FCSTD DOCUMENT  (FreeCAD 0.22R0.21.2)
Label: XL30AssemblyChamber01
License: All rights reserved
LicenseURL: http://en.wikipedia.org/wiki/All_rights_reserved
objects: Part::Feature×37, Part::Cylinder×30, Part::Compound×21, App::Link×18, Part::Cut×18, Part::MultiFuse×13, Part::Box×9, Part::FeaturePython×8, Spreadsheet::Sheet×1, Part::Sphere×1, App::Part×1
note: 137 computed .brp shape members not serialized (recipe doc carries the construction recipe); baked Part::Feature solids carry a one-line shape summary decoded from their .brp
EXTERNAL_REF file=XL30MainChamberModel.FCStd obj=Cut020
EXTERNAL_REF file=XL30ColumnOutline.FCStd obj=Cut001
EXTERNAL_REF file=XL30FinalAppertureHolder.FCStd obj=Cut001_solid
EXTERNAL_REF file=XL30ColumnAttachmentRing01.FCStd obj=Cut010
EXTERNAL_REF file=XL30ColumnAttachmentRing01.FCStd obj=Spreadsheet
EXTERNAL_REF file=XL30ColumnAttachmentRing_PCBKicker01.FCStd obj=Fusion001
EXTERNAL_REF file=XL30ColumnAttachmentRing_PCBKicker01.FCStd obj=Cut005
EXTERNAL_REF file=../QUAK/ESRCryoStage/Cryostage.FCStd obj=Compound001
EXTERNAL_REF file=XL30Frontdoor_Flanges01.FCStd obj=Cut005_solid
EXTERNAL_REF file=PhilippsXL30_FlangeToCF35_CF40_ZeroLengthAdapter_100.FCStd obj=Cut002
EXTERNAL_REF file=PhilippsXL30_FlangeToCF63_ZeroLengthAdapter_120.FCStd obj=Cut001
EXTERNAL_REF file=PhilipsXL30_FlangeToCF35_CF40_ZeroLengthAdapter.FCStd obj=Cut002
EXTERNAL_REF file=PhilipsXL30_Blindflange_100_TopBack.FCStd obj=Cut004
EXTERNAL_REF file=Quak_XL30_Modulator2.FCStd obj=Compound
EXTERNAL_REF file=PhilipsXL30_AligningRing.FCStd obj=Cut005_solid
EXTERNAL_REF file=PhilipsXL30_AligningRing.FCStd obj=Cut006_solid

FEATURE [App::Link] Link  label="MainChamberModel"
  LinkedObject = -> <external XL30MainChamberModel.FCStd>#Cut020
FEATURE [App::Link] Link001  label="BasicOutline_Part0and1"
  LinkPlacement = pos=(165,116,310) rot=(0,0,1;0rad)
  LinkedObject = -> <external XL30ColumnOutline.FCStd>#Cut001
  Placement = pos=(165,116,310) rot=(0,0,1;0rad)
FEATURE [App::Link] Link002  label="XL30FinalAppertureHolder"
  LinkPlacement = pos=(165,116,207.1) rot=(0,0,1;0rad)
  LinkedObject = -> <external XL30FinalAppertureHolder.FCStd>#Cut001_solid
  Placement = pos=(165,116,207.1) rot=(0,0,1;0rad)
FEATURE [App::Link] Link003  label="AttachmentRing_Column01"
  LinkPlacement = pos=(165,116,270) rot=(0,0,1;0rad)
  LinkedObject = -> <external XL30ColumnAttachmentRing01.FCStd>#Cut010
  Placement = pos=(165,116,270) rot=(0,0,1;0rad)
FEATURE [Part::FeaturePython] ScrewTap  label="M4x119.9-ScrewTap"  # Fasteners workbench fastener (typed FeaturePython)
  Placement = pos=(53.83,0,0) rot=(0,0,1;0rad)
  diameter = 6
  diameterCustom = 6
  invert = false
  leftHanded = false
  length = 119.9
  matchOuter = false
  offset = 0
  pitchCustom = 1
  thread = true
  type = 2
  expr: .Placement.Base.x = (<<XL30ColumnAttachmentRing01>>#<<AttachmentRing01>>.ring_od + <<XL30ColumnAttachmentRing01>>#<<AttachmentRing01>>.ring_id) / 4
  expr: length = <<XL30Assembly01>>.attachment_pcb_threadrod_lenmin
FEATURE [Spreadsheet::Sheet] Spreadsheet  label="XL30Assembly01"
  cells = A2='PCB Ring distance; B2(attachmentring_pcb_distance)==18 + 62.9; C2='Note: Include poleshoe height of 62.9mm; E2='Real threaded rod minimum length; F2(attachment_pcb_threadrod_lenmin)==attachmentring_pcb_distance + 2 * <<XL30ColumnAttachmentRing01>>#<<AttachmentRing01>>.ring_thickness + 7 + 22
FEATURE [Part::FeaturePython] ScrewTap001  label="M4x119.9-ScrewTap001"  # Fasteners workbench fastener (typed FeaturePython)
  Placement = pos=(53.83,0,0) rot=(0,0,1;0rad)
  diameter = 6
  diameterCustom = 6
  invert = false
  leftHanded = false
  length = 119.9
  matchOuter = false
  offset = 0
  pitchCustom = 1
  thread = true
  type = 2
  expr: .Placement.Base.x = (<<XL30ColumnAttachmentRing01>>#<<AttachmentRing01>>.ring_od + <<XL30ColumnAttachmentRing01>>#<<AttachmentRing01>>.ring_id) / 4
  expr: length = <<XL30Assembly01>>.attachment_pcb_threadrod_lenmin
FEATURE [Part::Compound] Compound
  Links = -> [ScrewTap001]
  Placement = pos=(0,0,0) rot=(0,0,1;0.785398rad)
FEATURE [Part::FeaturePython] ScrewTap002  label="M4x119.9-ScrewTap002"  # Fasteners workbench fastener (typed FeaturePython)
  Placement = pos=(53.83,0,0) rot=(0,0,1;0rad)
  diameter = 6
  diameterCustom = 6
  invert = false
  leftHanded = false
  length = 119.9
  matchOuter = false
  offset = 0
  pitchCustom = 1
  thread = true
  type = 2
  expr: .Placement.Base.x = (<<XL30ColumnAttachmentRing01>>#<<AttachmentRing01>>.ring_od + <<XL30ColumnAttachmentRing01>>#<<AttachmentRing01>>.ring_id) / 4
  expr: length = <<XL30Assembly01>>.attachment_pcb_threadrod_lenmin
FEATURE [Part::Compound] Compound001
  Links = -> [ScrewTap002]
  Placement = pos=(0,0,0) rot=(0,0,1;1.5708rad)
FEATURE [Part::FeaturePython] ScrewTap003  label="M4x119.9-ScrewTap003"  # Fasteners workbench fastener (typed FeaturePython)
  Placement = pos=(53.83,0,0) rot=(0,0,1;0rad)
  diameter = 6
  diameterCustom = 6
  invert = false
  leftHanded = false
  length = 119.9
  matchOuter = false
  offset = 0
  pitchCustom = 1
  thread = true
  type = 2
  expr: .Placement.Base.x = (<<XL30ColumnAttachmentRing01>>#<<AttachmentRing01>>.ring_od + <<XL30ColumnAttachmentRing01>>#<<AttachmentRing01>>.ring_id) / 4
  expr: length = <<XL30Assembly01>>.attachment_pcb_threadrod_lenmin
FEATURE [Part::Compound] Compound002
  Links = -> [ScrewTap003]
  Placement = pos=(0,0,0) rot=(0,0,1;2.35619rad)
FEATURE [Part::FeaturePython] ScrewTap004  label="M4x119.9-ScrewTap004"  # Fasteners workbench fastener (typed FeaturePython)
  Placement = pos=(53.83,0,0) rot=(0,0,1;0rad)
  diameter = 6
  diameterCustom = 6
  invert = false
  leftHanded = false
  length = 119.9
  matchOuter = false
  offset = 0
  pitchCustom = 1
  thread = true
  type = 2
  expr: .Placement.Base.x = (<<XL30ColumnAttachmentRing01>>#<<AttachmentRing01>>.ring_od + <<XL30ColumnAttachmentRing01>>#<<AttachmentRing01>>.ring_id) / 4
  expr: length = <<XL30Assembly01>>.attachment_pcb_threadrod_lenmin
FEATURE [Part::Compound] Compound003
  Links = -> [ScrewTap004]
  Placement = pos=(0,0,0) rot=(0,0,1;3.14159rad)
FEATURE [Part::FeaturePython] ScrewTap005  label="M4x119.9-ScrewTap005"  # Fasteners workbench fastener (typed FeaturePython)
  Placement = pos=(53.83,0,0) rot=(0,0,1;0rad)
  diameter = 6
  diameterCustom = 6
  invert = false
  leftHanded = false
  length = 119.9
  matchOuter = false
  offset = 0
  pitchCustom = 1
  thread = true
  type = 2
  expr: .Placement.Base.x = (<<XL30ColumnAttachmentRing01>>#<<AttachmentRing01>>.ring_od + <<XL30ColumnAttachmentRing01>>#<<AttachmentRing01>>.ring_id) / 4
  expr: length = <<XL30Assembly01>>.attachment_pcb_threadrod_lenmin
FEATURE [Part::Compound] Compound004
  Links = -> [ScrewTap005]
  Placement = pos=(0,0,0) rot=(0,0,1;3.92699rad)
FEATURE [Part::FeaturePython] ScrewTap006  label="M4x119.9-ScrewTap006"  # Fasteners workbench fastener (typed FeaturePython)
  Placement = pos=(53.83,0,0) rot=(0,0,1;0rad)
  diameter = 6
  diameterCustom = 6
  invert = false
  leftHanded = false
  length = 119.9
  matchOuter = false
  offset = 0
  pitchCustom = 1
  thread = true
  type = 2
  expr: .Placement.Base.x = (<<XL30ColumnAttachmentRing01>>#<<AttachmentRing01>>.ring_od + <<XL30ColumnAttachmentRing01>>#<<AttachmentRing01>>.ring_id) / 4
  expr: length = <<XL30Assembly01>>.attachment_pcb_threadrod_lenmin
FEATURE [Part::Compound] Compound005
  Links = -> [ScrewTap006]
  Placement = pos=(0,0,0) rot=(0,0,-1;1.5708rad)
FEATURE [Part::FeaturePython] ScrewTap007  label="M4x119.9-ScrewTap007"  # Fasteners workbench fastener (typed FeaturePython)
  Placement = pos=(53.83,0,0) rot=(0,0,1;0rad)
  diameter = 6
  diameterCustom = 6
  invert = false
  leftHanded = false
  length = 119.9
  matchOuter = false
  offset = 0
  pitchCustom = 1
  thread = true
  type = 2
  expr: .Placement.Base.x = (<<XL30ColumnAttachmentRing01>>#<<AttachmentRing01>>.ring_od + <<XL30ColumnAttachmentRing01>>#<<AttachmentRing01>>.ring_id) / 4
  expr: length = <<XL30Assembly01>>.attachment_pcb_threadrod_lenmin
FEATURE [Part::Compound] Compound006
  Links = -> [ScrewTap007]
  Placement = pos=(0,0,0) rot=(0,0,-1;0.785398rad)
FEATURE [Part::Compound] Compound007  label="ThreadedRodsAttachmentRing"
  Links = -> [Compound006,Compound,Compound001,Compound002,Compound003,Compound004,Compound005,ScrewTap]
  Placement = pos=(165,116,275) rot=(0,0,1;0rad)
  expr: .Placement.Base.z = 270 + <<XL30ColumnAttachmentRing01>>#<<AttachmentRing01>>.ring_thickness
FEATURE [App::Link] Link005  label="Stackmountring01"
  LinkPlacement = pos=(165,116,158) rot=(0,0,1;0rad)
  LinkedObject = -> <external XL30ColumnAttachmentRing_PCBKicker01.FCStd>#Fusion001
  Placement = pos=(165,116,158) rot=(0,0,1;0rad)
FEATURE [App::Link] Link006  label="PCBStackTemplate"
  LinkPlacement = pos=(155,95,185) rot=(0,0,1;0rad)
  LinkedObject = -> <external XL30ColumnAttachmentRing_PCBKicker01.FCStd>#Cut005
  Placement = pos=(155,95,185) rot=(0,0,1;0rad)
FEATURE [Part::Cylinder] Cylinder
  Angle = 360
  AttacherType = Attacher::AttachEngine3D
  FirstAngle = 0
  Height = 296.4
  Placement = pos=(0,0,-83.4) rot=(0,1,0;0rad)
  Radius = 21
  SecondAngle = 0
FEATURE [Part::Sphere] Sphere
  Angle1 = -90
  Angle2 = 90
  Angle3 = 360
  AttacherType = Attacher::AttachEngine3D
  Placement = pos=(0,0,-83.4) rot=(0,0,1;0rad)
  Radius = 21
FEATURE [Part::Compound] Compound008  label="SEDetectorTemplate"
  Links = -> [Cylinder,Sphere]
  Placement = pos=(18,116,275) rot=(0,-1,0;1.23046rad)
FEATURE [App::Link] Link007  label="StageAssembly"
  LinkPlacement = pos=(113.5,99,107) rot=(0,0,1;0rad)
  LinkedObject = -> <external ../QUAK/ESRCryoStage/Cryostage.FCStd>#Compound001
  Placement = pos=(113.5,99,107) rot=(0,0,1;0rad)
FEATURE [App::Link] Link008  label="XL30FrontdoorCF64Flanges (Solid)"
  LinkPlacement = pos=(0,-35,0) rot=(0,0,1;0rad)
  LinkedObject = -> <external XL30Frontdoor_Flanges01.FCStd>#Cut005_solid
  Placement = pos=(0,-35,0) rot=(0,0,1;0rad)
FEATURE [Part::Cylinder] Cylinder001
  Angle = 360
  AttacherType = Attacher::AttachEngine3D
  FirstAngle = 0
  Height = 112
  Placement = pos=(0,116,121.5) rot=(0,1,0;1.5708rad)
  Radius = 5
  SecondAngle = 0
FEATURE [Part::Cylinder] Cylinder002
  Angle = 360
  AttacherType = Attacher::AttachEngine3D
  FirstAngle = 0
  Height = 112
  Placement = pos=(0,116,142.5) rot=(0,1,0;1.5708rad)
  Radius = 5
  SecondAngle = 0
FEATURE [Part::MultiFuse] Fusion  label="NitrogenPipes10mm"
  Shapes = -> [Cylinder001,Cylinder002]
FEATURE [App::Link] Link009  label="StageAssembly001"
  LinkPlacement = pos=(181.5,64.5,88.5) rot=(0,0,1;1.5708rad)
  LinkedObject = -> <external ../QUAK/ESRCryoStage/Cryostage.FCStd>#Compound001
  Placement = pos=(181.5,64.5,88.5) rot=(0,0,1;1.5708rad)
FEATURE [Part::Cylinder] Cylinder003
  Angle = 360
  AttacherType = Attacher::AttachEngine3D
  FirstAngle = 0
  Height = 99.5
  Placement = pos=(0,0,121.5) rot=(0,1,0;1.5708rad)
  Radius = 5
  SecondAngle = 0
FEATURE [Part::Cylinder] Cylinder004
  Angle = 360
  AttacherType = Attacher::AttachEngine3D
  FirstAngle = 0
  Height = 99.5
  Placement = pos=(0,0,142.5) rot=(0,1,0;1.5708rad)
  Radius = 5
  SecondAngle = 0
FEATURE [Part::MultiFuse] Fusion001  label="NitrogenPipes10mm001"
  Shapes = -> [Cylinder003,Cylinder004]
FEATURE [Part::Compound] Compound009  label="NitrogenPipesConfig2"
  Links = -> [Fusion001]
  Placement = pos=(164.5,-35,-18.5) rot=(0,0,1;1.5708rad)
FEATURE [Part::Compound] Compound010  label="StageFromFrontdoor"
  Links = -> [Link009,Compound009]
FEATURE [Part::Compound] Compound011  label="StageFromSide"
  Links = -> [Link007,Fusion]
FEATURE [Part::Box] Box  label="Cube"
  AttacherType = Attacher::AttachEngine3D
  Height = 43
  Length = 50
  Width = 34
FEATURE [Part::Box] Box001  label="Cube001"
  AttacherType = Attacher::AttachEngine3D
  Height = 50
  Length = 100
  Placement = pos=(41,0,43) rot=(0,1,0;0.785398rad)
  Width = 34
FEATURE [Part::Box] Box002  label="Cube002"
  AttacherType = Attacher::AttachEngine3D
  Height = 50
  Length = 72
  Placement = pos=(0,34,34) rot=(1,0,0;0.925025rad)
  Width = 20
FEATURE [Part::Box] Box003  label="Cube003"
  AttacherType = Attacher::AttachEngine3D
  Height = 50
  Length = 72
  Placement = pos=(0,34,34) rot=(1,0,0;0.925025rad)
  Width = 20
FEATURE [Part::Box] Box004  label="Cube004"
  AttacherType = Attacher::AttachEngine3D
  Height = 26
  Length = 1.6
  Placement = pos=(49.9,7,0) rot=(0,0,1;0rad)
  Width = 20
FEATURE [Part::Box] Box005  label="Cube005"
  AttacherType = Attacher::AttachEngine3D
  Height = 2
  Length = 15
  Placement = pos=(15,0,0) rot=(0,0,1;0rad)
  Width = 34
FEATURE [Part::Box] Box006  label="Cube006"
  AttacherType = Attacher::AttachEngine3D
  Height = 2
  Length = 15
  Placement = pos=(15,0,0) rot=(0,0,1;0rad)
  Width = 34
FEATURE [Part::Box] Box007  label="Cube007"
  AttacherType = Attacher::AttachEngine3D
  Height = 26
  Length = 30
  Placement = pos=(53,16,0) rot=(0,0,1;0rad)
  Width = 2
FEATURE [Part::Box] Box008  label="Cube008"
  AttacherType = Attacher::AttachEngine3D
  Height = 10
  Length = 10
  Placement = pos=(-7,0,0) rot=(0,1,0;0.785398rad)
  Width = 34
FEATURE [Part::Compound] Compound012
  Links = -> [Box003]
  Placement = pos=(72,34,0) rot=(0,0,1;3.14159rad)
FEATURE [Part::Cylinder] Cylinder005
  Angle = 360
  AttacherType = Attacher::AttachEngine3D
  FirstAngle = 0
  Height = 26
  Radius = 30.5
  SecondAngle = 0
FEATURE [Part::Cylinder] Cylinder006
  Angle = 360
  AttacherType = Attacher::AttachEngine3D
  FirstAngle = 0
  Height = 26
  Radius = 9
  SecondAngle = 0
FEATURE [Part::Cut] Cut001
  Base = -> Cylinder005
  Placement = pos=(51.5,17,0) rot=(0,0,1;0rad)
  Tool = -> Cylinder006
FEATURE [Part::Cylinder] Cylinder007
  Angle = 360
  AttacherType = Attacher::AttachEngine3D
  FirstAngle = 0
  Height = 26
  Radius = 30.5
  SecondAngle = 0
FEATURE [Part::Cylinder] Cylinder008
  Angle = 360
  AttacherType = Attacher::AttachEngine3D
  FirstAngle = 0
  Height = 26
  Radius = 9
  SecondAngle = 0
FEATURE [Part::Cut] Cut002  label="CoilHolderBlank"
  Base = -> Cylinder007
  Placement = pos=(51.5,17,0) rot=(0,0,1;0rad)
  Tool = -> Cylinder008
FEATURE [Part::Cylinder] Cylinder009
  Angle = 360
  AttacherType = Attacher::AttachEngine3D
  FirstAngle = 0
  Height = 22
  Radius = 30.5
  SecondAngle = 0
FEATURE [Part::Cylinder] Cylinder010
  Angle = 360
  AttacherType = Attacher::AttachEngine3D
  FirstAngle = 0
  Height = 22
  Radius = 11
  SecondAngle = 0
FEATURE [Part::Cut] Cut004  label="CoilArea"
  Base = -> Cylinder009
  Placement = pos=(51.5,17,2) rot=(0,0,1;0rad)
  Tool = -> Cylinder010
FEATURE [Part::Cut] Cut005
  Base = -> Cut002
  Tool = -> Cut004
FEATURE [Part::Cut] Cut007
  Base = -> Cut005
  Tool = -> Box004
FEATURE [Part::Cylinder] Cylinder011
  Angle = 360
  AttacherType = Attacher::AttachEngine3D
  FirstAngle = 0
  Height = 34
  Placement = pos=(35,34,30) rot=(1,0,0;1.5708rad)
  Radius = 1.65
  SecondAngle = 0
FEATURE [Part::Cylinder] Cylinder012
  Angle = 360
  AttacherType = Attacher::AttachEngine3D
  FirstAngle = 0
  Height = 34
  Placement = pos=(35,20,27) rot=(1,0,0;0rad)
  Radius = 1.65
  SecondAngle = 0
FEATURE [Part::Cylinder] Cylinder013
  Angle = 360
  AttacherType = Attacher::AttachEngine3D
  FirstAngle = 0
  Height = 34
  Placement = pos=(35,14,27) rot=(1,0,0;0rad)
  Radius = 1.65
  SecondAngle = 0
FEATURE [Part::Cylinder] Cylinder014
  Angle = 360
  AttacherType = Attacher::AttachEngine3D
  FirstAngle = 0
  Height = 10
  Placement = pos=(20,5,0) rot=(0,0,1;0rad)
  Radius = 2.5
  SecondAngle = 0
FEATURE [Part::Cylinder] Cylinder015
  Angle = 360
  AttacherType = Attacher::AttachEngine3D
  FirstAngle = 0
  Height = 10
  Placement = pos=(20,29,0) rot=(0,0,1;0rad)
  Radius = 2.5
  SecondAngle = 0
FEATURE [Part::Cylinder] Cylinder016
  Angle = 360
  AttacherType = Attacher::AttachEngine3D
  FirstAngle = 0
  Height = 10
  Placement = pos=(20,5,0) rot=(0,0,1;0rad)
  Radius = 2.5
  SecondAngle = 0
FEATURE [Part::Cylinder] Cylinder017
  Angle = 360
  AttacherType = Attacher::AttachEngine3D
  FirstAngle = 0
  Height = 10
  Placement = pos=(20,29,0) rot=(0,0,1;0rad)
  Radius = 2.5
  SecondAngle = 0
FEATURE [Part::Cylinder] Cylinder018
  Angle = 360
  AttacherType = Attacher::AttachEngine3D
  FirstAngle = 0
  Height = 26
  Placement = pos=(39.5,17,0) rot=(0,0,1;0rad)
  Radius = 1
  SecondAngle = 0
FEATURE [Part::Cylinder] Cylinder019
  Angle = 360
  AttacherType = Attacher::AttachEngine3D
  FirstAngle = 0
  Height = 26
  Placement = pos=(23,17,0) rot=(0,0,1;0rad)
  Radius = 1
  SecondAngle = 0
FEATURE [Part::Cylinder] Cylinder020  label="NitrogenChamber01"
  Angle = 360
  AttacherType = Attacher::AttachEngine3D
  FirstAngle = 0
  Height = 38
  Placement = pos=(13,17,0) rot=(0,0,1;1.5708rad)
  Radius = 5
  SecondAngle = 0
FEATURE [Part::Cylinder] Cylinder021  label="NitrogenChamber002"
  Angle = 360
  AttacherType = Attacher::AttachEngine3D
  FirstAngle = 0
  Height = 20
  Placement = pos=(0,17,14.5) rot=(0,1,0;1.5708rad)
  Radius = 5
  SecondAngle = 0
FEATURE [Part::Cylinder] Cylinder022  label="NitrogenChamber003"
  Angle = 360
  AttacherType = Attacher::AttachEngine3D
  FirstAngle = 0
  Height = 20
  Placement = pos=(0,17,35.5) rot=(0,1,0;1.5708rad)
  Radius = 5
  SecondAngle = 0
FEATURE [Part::Cylinder] Cylinder023
  Angle = 360
  AttacherType = Attacher::AttachEngine3D
  FirstAngle = 0
  Height = 20
  Placement = pos=(0,4.5,0) rot=(0,1,0;0.785398rad)
  Radius = 1.65
  SecondAngle = 0
FEATURE [Part::Cylinder] Cylinder024
  Angle = 360
  AttacherType = Attacher::AttachEngine3D
  FirstAngle = 0
  Height = 20
  Placement = pos=(0,29.5,0) rot=(0,1,0;0.785398rad)
  Radius = 1.65
  SecondAngle = 0
FEATURE [Part::Cylinder] Cylinder025
  Angle = 360
  AttacherType = Attacher::AttachEngine3D
  FirstAngle = 0
  Height = 48
  Placement = pos=(0,5,26) rot=(0,1,0;1.5708rad)
  Radius = 1.5
  SecondAngle = 0
FEATURE [Part::Cylinder] Cylinder026
  Angle = 360
  AttacherType = Attacher::AttachEngine3D
  FirstAngle = 0
  Height = 48
  Placement = pos=(0,29,26) rot=(0,1,0;1.5708rad)
  Radius = 1.5
  SecondAngle = 0
FEATURE [Part::MultiFuse] Fusion002
  Shapes = -> [Box001,Box002,Compound012]
FEATURE [Part::Cut] Cut
  Base = -> Box
  Tool = -> Fusion002
FEATURE [Part::Cut] Cut003
  Base = -> Cut
  Tool = -> Cut001
FEATURE [Part::MultiFuse] Fusion003  label="M4Mountscrews01_Corehole"
  Shapes = -> [Cylinder011,Cylinder012,Cylinder013]
FEATURE [Part::Cut] Cut008
  Base = -> Cut003
  Tool = -> Fusion003
FEATURE [Part::MultiFuse] Fusion004  label="BoreholeM6Screws01"
  Shapes = -> [Cylinder015,Cylinder014]
FEATURE [Part::Cut] Cut009
  Base = -> Cut008
  Tool = -> Fusion004
FEATURE [Part::Cut] Cut011
  Base = -> Cut009
  Tool = -> Box006
FEATURE [Part::MultiFuse] Fusion005  label="BoreholeM6Screws002"
  Shapes = -> [Cylinder017,Cylinder016]
FEATURE [Part::Cut] Cut010
  Base = -> Box005
  Tool = -> Fusion005
FEATURE [Part::MultiFuse] Fusion006
  Shapes = -> [Cut007,Cut010]
FEATURE [Part::Cut] Cut012
  Base = -> Fusion006
  Tool = -> Box007
FEATURE [Part::MultiFuse] Fusion007  label="WireHoles"
  Shapes = -> [Cylinder019,Cylinder018]
FEATURE [Part::Cut] Cut013  label="Coilholder"
  Base = -> Cut012
  Tool = -> Fusion007
FEATURE [Part::MultiFuse] Fusion008  label="NitrogenChamber"
  Shapes = -> [Cylinder020,Cylinder021,Cylinder022]
FEATURE [Part::Cut] Cut014
  Base = -> Cut011
  Tool = -> Fusion008
FEATURE [Part::Cut] Cut015
  Base = -> Cut014
  Tool = -> Box008
FEATURE [Part::MultiFuse] Fusion009  label="M4Screws"
  Shapes = -> [Cylinder023,Cylinder024]
FEATURE [Part::Cut] Cut016
  Base = -> Cut015
  Tool = -> Fusion009
FEATURE [Part::MultiFuse] Fusion010  label="CableDrillHole"
  Shapes = -> [Cylinder025,Cylinder026]
FEATURE [Part::Cut] Cut017  label="Cryostage"
  Base = -> Cut016
  Tool = -> Fusion010
FEATURE [Part::Compound] Compound013  label="StageAssembly002"
  Links = -> [Cut013,Cut017]
  Placement = pos=(-51.5,-17,0) rot=(0,0,1;0rad)
FEATURE [Part::Cylinder] Cylinder027
  Angle = 360
  AttacherType = Attacher::AttachEngine3D
  FirstAngle = 0
  Height = 99.5
  Placement = pos=(0,0,121.5) rot=(0,1,0;1.5708rad)
  Radius = 5
  SecondAngle = 0
FEATURE [Part::Cylinder] Cylinder028
  Angle = 360
  AttacherType = Attacher::AttachEngine3D
  FirstAngle = 0
  Height = 99.5
  Placement = pos=(0,0,142.5) rot=(0,1,0;1.5708rad)
  Radius = 5
  SecondAngle = 0
FEATURE [Part::MultiFuse] Fusion011  label="NitrogenPipes10mm002"
  Shapes = -> [Cylinder027,Cylinder028]
FEATURE [Part::Compound] Compound014  label="NitrogenPipesConfig003"
  Links = -> [Fusion011]
  Placement = pos=(164.5,-35,-18.5) rot=(0,0,1;1.5708rad)
FEATURE [App::Link] Link010  label="StageAssembly003"
  LinkPlacement = pos=(181.5,64.5,88.5) rot=(0,0,1;1.5708rad)
  LinkedObject = -> Compound013
  Placement = pos=(181.5,64.5,88.5) rot=(0,0,1;1.5708rad)
FEATURE [Part::Compound] Compound015  label="StageFromFrontdoor_LowestPossiblePosition"
  Links = -> [Link010,Compound014]
  Placement = pos=(0,0,-55) rot=(0,0,1;0rad)
FEATURE [App::Link] Link011  label="Flange100mmToCF40_Right"
  LinkPlacement = pos=(330,107.5,199) rot=(0,1,0;1.5708rad)
  LinkedObject = -> <external PhilippsXL30_FlangeToCF35_CF40_ZeroLengthAdapter_100.FCStd>#Cut002
  Placement = pos=(330,107.5,199) rot=(0,1,0;1.5708rad)
FEATURE [App::Link] Link012  label="Cut017"
  LinkPlacement = pos=(0,0,0) rot=(0,1,0;-1.5708rad)
  LinkedObject = -> <external PhilippsXL30_FlangeToCF63_ZeroLengthAdapter_120.FCStd>#Cut001
  Placement = pos=(0,0,0) rot=(0,1,0;-1.5708rad)
FEATURE [Part::Compound] Compound016  label="Flange120mmToCF64_Left"
  Links = -> [Link012]
  Placement = pos=(0,115.5,140) rot=(1,0,0;1.0472rad)
FEATURE [App::Link] Link013  label="Flange85mmToCF40_BackBottom_001"
  LinkPlacement = pos=(0,0,0) rot=(0,1,0;-1.5708rad)
  LinkedObject = -> <external PhilipsXL30_FlangeToCF35_CF40_ZeroLengthAdapter.FCStd>#Cut002
  Placement = pos=(0,0,0) rot=(0,1,0;-1.5708rad)
FEATURE [App::Link] Link015  label="Flange85mmToCF40_BackBottom_002"
  LinkPlacement = pos=(0,0,0) rot=(0,1,0;-1.5708rad)
  Placement = pos=(0,0,0) rot=(0,1,0;-1.5708rad)
FEATURE [Part::Compound] Compound017
  Links = -> [Link013]
  Placement = pos=(0,0,0) rot=(1,0,0;1.0472rad)
FEATURE [Part::Compound] Compound018  label="Flange85mmToCF40_BackBottom"
  Links = -> [Compound017]
  Placement = pos=(45,240,97.5) rot=(0,0,-1;0.785398rad)
FEATURE [Part::Feature] Solid  label="CF35 Flange"
  Placement = pos=(0,0,4) rot=(-1,0,0;1.5708rad)
  shape: bbox 70 x 70 x 12.7 mm, 58 faces (baked)
FEATURE [App::Link] Link016  label="XL30TopBackFlange100"
  LinkedObject = -> <external PhilipsXL30_Blindflange_100_TopBack.FCStd>#Cut004
FEATURE [Part::MultiFuse] Fusion012
  Shapes = -> [Solid,Link016]
FEATURE [Part::Cylinder] Cylinder029
  Angle = 360
  AttacherType = Attacher::AttachEngine3D
  FirstAngle = 0
  Height = 30
  Placement = pos=(0,0,-10) rot=(0,0,1;0rad)
  Radius = 20
  SecondAngle = 0
FEATURE [Part::Cut] Cut018  label="PhilipsXL30_Flange_100_TopLeft_ToCF35_CF40"
  Base = -> Fusion012
  Placement = pos=(-12,0,0) rot=(0,1,0;1.5708rad)
  Tool = -> Cylinder029
FEATURE [Part::Compound] Compound019
  Links = -> [Cut018]
  Placement = pos=(0,0,0) rot=(1,0,0;1.5708rad)
FEATURE [Part::Compound] Compound020
  Links = -> [Compound019]
  Placement = pos=(45,240,286) rot=(0,0,-1;0.785398rad)
FEATURE [Part::Feature] Part__Feature  label="Bellow-AA-All_Bellow63-35025-1.3"
  shape: bbox 88.9 x 69.2 x 88.9 mm, 28 faces (baked)
FEATURE [Part::Feature] Part__Feature001  label="NW63CF-weld_Tube70"
  Placement = pos=(0,78.7,0) rot=(0,0,1;0rad)
  shape: bbox 113.5 x 17.5 x 113.5 mm, 80 faces (baked)
FEATURE [Part::Feature] Part__Feature002  label="NW63CF-weld_Tube071"
  Placement = pos=(0,-9.5,0) rot=(0.382683,0,0.92388;3.14159rad)
  shape: bbox 113.5 x 17.5 x 113.5 mm, 80 faces (baked)
FEATURE [Part::Feature] Part__Feature003  label="Bracket SEWB_CF63-D113.5"
  Placement = pos=(-63.0548,67.7,26.1181) rot=(0,1,0;0.392699rad)
  shape: bbox 26.73 x 6 x 25.71 mm, 14 faces (baked)
FEATURE [Part::Feature] Part__Feature004  label="Bracket SEWB_CF63-D113.006"
  Placement = pos=(8.90841,67.7,-67.6661) rot=(0,-1,0;1.7017rad)
  shape: bbox 22.29 x 6 x 23.92 mm, 14 faces (baked)
FEATURE [Part::Feature] Part__Feature005  label="Bracket SEWB_CF63-D113.007"
  Placement = pos=(54.1464,67.7,41.548) rot=(0,1,0;2.48709rad)
  shape: bbox 27.71 x 6 x 27.37 mm, 14 faces (baked)
FEATURE [Part::Feature] Part__Feature006  label="Bracket SEWB_CF63-D113.008"
  Placement = pos=(8.90841,-4.5,-67.6661) rot=(0,-1,0;1.7017rad)
  shape: bbox 22.29 x 6 x 23.92 mm, 14 faces (baked)
FEATURE [Part::Feature] Part__Feature007  label="Bracket SEWB_CF63-D113.009"
  Placement = pos=(54.1464,-4.5,41.548) rot=(0,1,0;2.48709rad)
  shape: bbox 27.71 x 6 x 27.37 mm, 14 faces (baked)
FEATURE [Part::Feature] Part__Feature008  label="Bracket SEWB_CF63-D113.010"
  Placement = pos=(-63.0548,-4.5,26.1181) rot=(0,1,0;0.392699rad)
  shape: bbox 26.73 x 6 x 25.71 mm, 14 faces (baked)
FEATURE [Part::Feature] Part__Feature009  label="StudM8-L130"
  Placement = pos=(-63.05,16.6,26.12) rot=(-0.427908,0.427908,-0.796109;1.79333rad)
  shape: bbox 8.701 x 131.4 x 9.485 mm, 203 faces (baked)
FEATURE [Part::Feature] Part__Feature010  label="StudM8-L131"
  Placement = pos=(8.91,16.6,-67.67) rot=(0,0,-1;1.5708rad)
  shape: bbox 8.06 x 131.5 x 9.307 mm, 203 faces (baked)
FEATURE [Part::Feature] Part__Feature011  label="StudM8-L132"
  Placement = pos=(54.15,16.6,41.55) rot=(0,0,-1;1.5708rad)
  shape: bbox 8.06 x 131.5 x 9.307 mm, 203 faces (baked)
FEATURE [Part::Feature] Part__Feature012  label="plain washer normal grade a_iso_Washer ISO 7089 - 8"
  Placement = pos=(54.1464,73.7,41.548) rot=(0,0,-1;1.5708rad)
  shape: bbox 16 x 1.6 x 16 mm, 6 faces (baked)
FEATURE [Part::Feature] Part__Feature013  label="plain washer normal grade a_iso_Washer ISO 7089 - 009"
  Placement = pos=(-63.0548,73.7,26.1181) rot=(0,0,-1;1.5708rad)
  shape: bbox 16 x 1.6 x 16 mm, 6 faces (baked)
FEATURE [Part::Feature] Part__Feature014  label="plain washer normal grade a_iso_Washer ISO 7089 - 010"
  Placement = pos=(8.90841,73.7,-67.6661) rot=(0,0,-1;1.5708rad)
  shape: bbox 16 x 1.6 x 16 mm, 6 faces (baked)
FEATURE [Part::Feature] Part__Feature015  label="plain washer normal grade a_iso_Washer ISO 7089 - 011"
  Placement = pos=(8.90841,67.7,-67.6661) rot=(0,0,1;1.5708rad)
  shape: bbox 16 x 1.6 x 16 mm, 6 faces (baked)
FEATURE [Part::Feature] Part__Feature016  label="plain washer normal grade a_iso_Washer ISO 7089 - 012"
  Placement = pos=(8.90841,-4.5,-67.6661) rot=(0,0,1;1.5708rad)
  shape: bbox 16 x 1.6 x 16 mm, 6 faces (baked)
FEATURE [Part::Feature] Part__Feature017  label="plain washer normal grade a_iso_Washer ISO 7089 - 013"
  Placement = pos=(54.1464,-4.5,41.548) rot=(0,0,1;1.5708rad)
  shape: bbox 16 x 1.6 x 16 mm, 6 faces (baked)
FEATURE [Part::Feature] Part__Feature018  label="plain washer normal grade a_iso_Washer ISO 7089 - 014"
  Placement = pos=(-63.0548,-4.5,26.1181) rot=(0,0,1;1.5708rad)
  shape: bbox 16 x 1.6 x 16 mm, 6 faces (baked)
FEATURE [Part::Feature] Part__Feature019  label="plain washer normal grade a_iso_Washer ISO 7089 - 015"
  Placement = pos=(-63.0548,67.7,26.1181) rot=(0,0,1;1.5708rad)
  shape: bbox 16 x 1.6 x 16 mm, 6 faces (baked)
FEATURE [Part::Feature] Part__Feature020  label="plain washer normal grade a_iso_Washer ISO 7089 - 016"
  Placement = pos=(54.1464,67.7,41.548) rot=(0,0,1;1.5708rad)
  shape: bbox 16 x 1.6 x 16 mm, 6 faces (baked)
FEATURE [Part::Feature] Part__Feature021  label="plain washer normal grade a_iso_Washer ISO 7089 - 017"
  Placement = pos=(54.1464,1.5,41.548) rot=(0,0,-1;1.5708rad)
  shape: bbox 16 x 1.6 x 16 mm, 6 faces (baked)
FEATURE [Part::Feature] Part__Feature022  label="plain washer normal grade a_iso_Washer ISO 7089 - 018"
  Placement = pos=(-63.0548,1.5,26.1181) rot=(0,0,-1;1.5708rad)
  shape: bbox 16 x 1.6 x 16 mm, 6 faces (baked)
FEATURE [Part::Feature] Part__Feature023  label="plain washer normal grade a_iso_Washer ISO 7089 - 019"
  Placement = pos=(8.90841,1.5,-67.6661) rot=(0,0,-1;1.5708rad)
  shape: bbox 16 x 1.6 x 16 mm, 6 faces (baked)
FEATURE [Part::Feature] Part__Feature024  label="hex nut style 1 gradeab_iso_ISO - 4032 - M8 - W - N"
  Placement = pos=(8.90841,-12.9,-67.6661) rot=(1,0,0;1.5708rad)
  shape: bbox 15.01 x 6.801 x 15.01 mm, 30 faces (baked)
FEATURE [Part::Feature] Part__Feature025  label="hex nut style 1 gradeab_iso_ISO - 4032 - M8 - W - N001"
  Placement = pos=(-63.0548,-12.9,26.1181) rot=(1,0,0;1.5708rad)
  shape: bbox 15.01 x 6.801 x 15.01 mm, 30 faces (baked)
FEATURE [Part::Feature] Part__Feature026  label="hex nut style 1 gradeab_iso_ISO - 4032 - M8 - W - N002"
  Placement = pos=(54.1464,-12.9,41.548) rot=(1,0,0;1.5708rad)
  shape: bbox 15.01 x 6.801 x 15.01 mm, 30 faces (baked)
FEATURE [Part::Feature] Part__Feature027  label="hex nut style 1 gradeab_iso_ISO - 4032 - M8 - W - N003"
  Placement = pos=(-63.0548,59.3,26.1181) rot=(1,0,0;1.5708rad)
  shape: bbox 15.01 x 6.801 x 15.01 mm, 30 faces (baked)
FEATURE [Part::Feature] Part__Feature028  label="hex nut style 1 gradeab_iso_ISO - 4032 - M8 - W - N004"
  Placement = pos=(8.90841,59.3,-67.6661) rot=(1,0,0;1.5708rad)
  shape: bbox 15.01 x 6.801 x 15.01 mm, 30 faces (baked)
FEATURE [Part::Feature] Part__Feature029  label="hex nut style 1 gradeab_iso_ISO - 4032 - M8 - W - N005"
  Placement = pos=(54.1464,59.3,41.548) rot=(1,0,0;1.5708rad)
  shape: bbox 15.01 x 6.801 x 15.01 mm, 30 faces (baked)
FEATURE [Part::Feature] Part__Feature030  label="hex nut style 1 gradeab_iso_ISO - 4032 - M8 - W - N006"
  Placement = pos=(-63.0548,82.1,26.1181) rot=(-1,0,0;1.5708rad)
  shape: bbox 15.01 x 6.801 x 15.01 mm, 30 faces (baked)
FEATURE [Part::Feature] Part__Feature031  label="hex nut style 1 gradeab_iso_ISO - 4032 - M8 - W - N007"
  Placement = pos=(8.90841,82.1,-67.6661) rot=(-1,0,0;1.5708rad)
  shape: bbox 15.01 x 6.801 x 15.01 mm, 30 faces (baked)
FEATURE [Part::Feature] Part__Feature032  label="hex nut style 1 gradeab_iso_ISO - 4032 - M8 - W - N008"
  Placement = pos=(54.1464,82.1,41.548) rot=(-1,0,0;1.5708rad)
  shape: bbox 15.01 x 6.801 x 15.01 mm, 30 faces (baked)
FEATURE [Part::Feature] Part__Feature033  label="hex nut style 1 gradeab_iso_ISO - 4032 - M8 - W - N009"
  Placement = pos=(54.1464,9.9,41.548) rot=(-1,0,0;1.5708rad)
  shape: bbox 15.01 x 6.801 x 15.01 mm, 30 faces (baked)
FEATURE [Part::Feature] Part__Feature034  label="hex nut style 1 gradeab_iso_ISO - 4032 - M8 - W - N010"
  Placement = pos=(8.90841,9.9,-67.6661) rot=(-1,0,0;1.5708rad)
  shape: bbox 15.01 x 6.801 x 15.01 mm, 30 faces (baked)
FEATURE [Part::Feature] Part__Feature035  label="hex nut style 1 gradeab_iso_ISO - 4032 - M8 - W - N011"
  Placement = pos=(-63.0548,9.9,26.1181) rot=(-1,0,0;1.5708rad)
  shape: bbox 15.01 x 6.801 x 15.01 mm, 30 faces (baked)
FEATURE [App::Part] Hositrad_CF63_SEWB  label="PortAligner_BoughtExternally"
  Group = -> [Part__Feature,Part__Feature001,Part__Feature002,Part__Feature003,Part__Feature004,Part__Feature005,Part__Feature006,Part__Feature007,Part__Feature008,Part__Feature009,Part__Feature010,Part__Feature011,Part__Feature012,Part__Feature013,Part__Feature014,Part__Feature015,Part__Feature016,Part__Feature017,Part__Feature018,Part__Feature019,Part__Feature020,Part__Feature021,Part__Feature022,+13 more]
  Origin = -> Origin
  Placement = pos=(167.95,-114,112.7) rot=(0,1,0;1.48353rad)
FEATURE [App::Link] Link017  label="KickerAssembly"
  LinkPlacement = pos=(165,116,158) rot=(0,0,1;0rad)
  LinkedObject = -> <external Quak_XL30_Modulator2.FCStd>#Compound
  Placement = pos=(165,116,158) rot=(0,0,1;0rad)
FEATURE [App::Link] Link018  label="AligningRing (Solid)"
  LinkPlacement = pos=(165,116,213) rot=(0,0,1;3.14159rad)
  LinkedObject = -> <external PhilipsXL30_AligningRing.FCStd>#Cut005_solid
  Placement = pos=(165,116,213) rot=(0,0,1;3.14159rad)
FEATURE [App::Link] Link021  label="Kickeraligner (Solid)"
  LinkPlacement = pos=(165,116,213) rot=(0,0,1;3.14159rad)
  LinkedObject = -> <external PhilipsXL30_AligningRing.FCStd>#Cut006_solid
  Placement = pos=(165,116,213) rot=(0,0,1;3.14159rad)

RESOLVED EXTERNAL PARTS (link-assembly join: the EXTERNAL_REF files above that resolve inside this repo's crawl, each included once):
---- part ../QUAK/ESRCryoStage/Cryostage.FCStd = doc fcstd_cd4b80d5eeee ----
FCSTD DOCUMENT  (FreeCAD 0.20R)
Label: Cryostage
License: All rights reserved
LicenseURL: http://en.wikipedia.org/wiki/All_rights_reserved
objects: Part::Cylinder×24, Part::Cut×18, Part::Box×9, Part::MultiFuse×9, Part::Compound×2
note: 62 computed .brp shape members not serialized (recipe doc carries the construction recipe); baked Part::Feature solids carry a one-line shape summary decoded from their .brp

FEATURE [Part::Box] Box  label="Cube"
  AttacherType = Attacher::AttachEngine3D
  Height = 43
  Length = 50
  Width = 34
FEATURE [Part::Box] Box001  label="Cube001"
  AttacherType = Attacher::AttachEngine3D
  Height = 50
  Length = 100
  Placement = pos=(41,0,43) rot=(0,1,0;0.785398rad)
  Width = 34
FEATURE [Part::Box] Box002  label="Cube002"
  AttacherType = Attacher::AttachEngine3D
  Height = 50
  Length = 72
  Placement = pos=(0,34,34) rot=(1,0,0;0.925025rad)
  Width = 20
FEATURE [Part::Box] Box003  label="Cube003"
  AttacherType = Attacher::AttachEngine3D
  Height = 50
  Length = 72
  Placement = pos=(0,34,34) rot=(1,0,0;0.925025rad)
  Width = 20
FEATURE [Part::Compound] Compound
  Links = -> [Box003]
  Placement = pos=(72,34,0) rot=(0,0,1;3.14159rad)
FEATURE [Part::MultiFuse] Fusion
  Shapes = -> [Box001,Box002,Compound]
FEATURE [Part::Cut] Cut
  Base = -> Box
  Tool = -> Fusion
FEATURE [Part::Cylinder] Cylinder
  Angle = 360
  AttacherType = Attacher::AttachEngine3D
  FirstAngle = 0
  Height = 26
  Radius = 30.5
  SecondAngle = 0
FEATURE [Part::Cylinder] Cylinder001
  Angle = 360
  AttacherType = Attacher::AttachEngine3D
  FirstAngle = 0
  Height = 26
  Radius = 9
  SecondAngle = 0
FEATURE [Part::Cut] Cut001
  Base = -> Cylinder
  Placement = pos=(51.5,17,0) rot=(0,0,1;0rad)
  Tool = -> Cylinder001
FEATURE [Part::Cylinder] Cylinder002
  Angle = 360
  AttacherType = Attacher::AttachEngine3D
  FirstAngle = 0
  Height = 26
  Radius = 30.5
  SecondAngle = 0
FEATURE [Part::Cylinder] Cylinder003
  Angle = 360
  AttacherType = Attacher::AttachEngine3D
  FirstAngle = 0
  Height = 26
  Radius = 9
  SecondAngle = 0
FEATURE [Part::Cut] Cut002  label="CoilHolderBlank"
  Base = -> Cylinder002
  Placement = pos=(51.5,17,0) rot=(0,0,1;0rad)
  Tool = -> Cylinder003
FEATURE [Part::Cut] Cut003
  Base = -> Cut
  Tool = -> Cut001
FEATURE [Part::Cylinder] Cylinder004
  Angle = 360
  AttacherType = Attacher::AttachEngine3D
  FirstAngle = 0
  Height = 22
  Radius = 30.5
  SecondAngle = 0
FEATURE [Part::Cylinder] Cylinder005
  Angle = 360
  AttacherType = Attacher::AttachEngine3D
  FirstAngle = 0
  Height = 22
  Radius = 11
  SecondAngle = 0
FEATURE [Part::Cut] Cut004  label="CoilArea"
  Base = -> Cylinder004
  Placement = pos=(51.5,17,2) rot=(0,0,1;0rad)
  Tool = -> Cylinder005
FEATURE [Part::Cut] Cut005
  Base = -> Cut002
  Tool = -> Cut004
FEATURE [Part::Cylinder] Cylinder006
  Angle = 360
  AttacherType = Attacher::AttachEngine3D
  FirstAngle = 0
  Height = 22
  Radius = 30.5
  SecondAngle = 0
FEATURE [Part::Cylinder] Cylinder007
  Angle = 360
  AttacherType = Attacher::AttachEngine3D
  FirstAngle = 0
  Height = 22
  Radius = 11
  SecondAngle = 0
FEATURE [Part::Cut] Cut006  label="CoilArea001Copper"
  Base = -> Cylinder006
  Placement = pos=(51.5,17,2) rot=(0,0,1;0rad)
  Tool = -> Cylinder007
FEATURE [Part::Box] Box004  label="Cube004"
  AttacherType = Attacher::AttachEngine3D
  Height = 26
  Length = 1.6
  Placement = pos=(49.9,7,0) rot=(0,0,1;0rad)
  Width = 20
FEATURE [Part::Cut] Cut007
  Base = -> Cut005
  Tool = -> Box004
FEATURE [Part::Cylinder] Cylinder008
  Angle = 360
  AttacherType = Attacher::AttachEngine3D
  FirstAngle = 0
  Height = 34
  Placement = pos=(35,34,30) rot=(1,0,0;1.5708rad)
  Radius = 1.65
  SecondAngle = 0
FEATURE [Part::Cylinder] Cylinder009
  Angle = 360
  AttacherType = Attacher::AttachEngine3D
  FirstAngle = 0
  Height = 34
  Placement = pos=(35,20,27) rot=(1,0,0;0rad)
  Radius = 1.65
  SecondAngle = 0
FEATURE [Part::Cylinder] Cylinder010
  Angle = 360
  AttacherType = Attacher::AttachEngine3D
  FirstAngle = 0
  Height = 34
  Placement = pos=(35,14,27) rot=(1,0,0;0rad)
  Radius = 1.65
  SecondAngle = 0
FEATURE [Part::MultiFuse] Fusion001  label="M4Mountscrews01_Corehole"
  Shapes = -> [Cylinder008,Cylinder009,Cylinder010]
FEATURE [Part::Cut] Cut008
  Base = -> Cut003
  Tool = -> Fusion001
FEATURE [Part::Cylinder] Cylinder011
  Angle = 360
  AttacherType = Attacher::AttachEngine3D
  FirstAngle = 0
  Height = 10
  Placement = pos=(20,5,0) rot=(0,0,1;0rad)
  Radius = 2.5
  SecondAngle = 0
FEATURE [Part::Cylinder] Cylinder012
  Angle = 360
  AttacherType = Attacher::AttachEngine3D
  FirstAngle = 0
  Height = 10
  Placement = pos=(20,29,0) rot=(0,0,1;0rad)
  Radius = 2.5
  SecondAngle = 0
FEATURE [Part::MultiFuse] Fusion002  label="BoreholeM6Screws01"
  Shapes = -> [Cylinder012,Cylinder011]
FEATURE [Part::Cut] Cut009
  Base = -> Cut008
  Tool = -> Fusion002
FEATURE [Part::Box] Box005  label="Cube005"
  AttacherType = Attacher::AttachEngine3D
  Height = 2
  Length = 15
  Placement = pos=(15,0,0) rot=(0,0,1;0rad)
  Width = 34
FEATURE [Part::Cylinder] Cylinder013
  Angle = 360
  AttacherType = Attacher::AttachEngine3D
  FirstAngle = 0
  Height = 10
  Placement = pos=(20,5,0) rot=(0,0,1;0rad)
  Radius = 2.5
  SecondAngle = 0
FEATURE [Part::Cylinder] Cylinder014
  Angle = 360
  AttacherType = Attacher::AttachEngine3D
  FirstAngle = 0
  Height = 10
  Placement = pos=(20,29,0) rot=(0,0,1;0rad)
  Radius = 2.5
  SecondAngle = 0
FEATURE [Part::MultiFuse] Fusion003  label="BoreholeM6Screws002"
  Shapes = -> [Cylinder014,Cylinder013]
FEATURE [Part::Cut] Cut010
  Base = -> Box005
  Tool = -> Fusion003
FEATURE [Part::MultiFuse] Fusion004
  Shapes = -> [Cut007,Cut010]
FEATURE [Part::Box] Box006  label="Cube006"
  AttacherType = Attacher::AttachEngine3D
  Height = 2
  Length = 15
  Placement = pos=(15,0,0) rot=(0,0,1;0rad)
  Width = 34
FEATURE [Part::Cut] Cut011
  Base = -> Cut009
  Tool = -> Box006
FEATURE [Part::Box] Box007  label="Cube007"
  AttacherType = Attacher::AttachEngine3D
  Height = 26
  Length = 30
  Placement = pos=(53,16,0) rot=(0,0,1;0rad)
  Width = 2
FEATURE [Part::Cut] Cut012
  Base = -> Fusion004
  Tool = -> Box007
FEATURE [Part::Cylinder] Cylinder015
  Angle = 360
  AttacherType = Attacher::AttachEngine3D
  FirstAngle = 0
  Height = 26
  Placement = pos=(39.5,17,0) rot=(0,0,1;0rad)
  Radius = 1
  SecondAngle = 0
FEATURE [Part::Cylinder] Cylinder016
  Angle = 360
  AttacherType = Attacher::AttachEngine3D
  FirstAngle = 0
  Height = 26
  Placement = pos=(23,17,0) rot=(0,0,1;0rad)
  Radius = 1
  SecondAngle = 0
FEATURE [Part::MultiFuse] Fusion005  label="WireHoles"
  Shapes = -> [Cylinder016,Cylinder015]
FEATURE [Part::Cut] Cut013  label="Coilholder"
  Base = -> Cut012
  Tool = -> Fusion005
FEATURE [Part::Cylinder] Cylinder017  label="NitrogenChamber01"
  Angle = 360
  AttacherType = Attacher::AttachEngine3D
  FirstAngle = 0
  Height = 38
  Placement = pos=(13,17,0) rot=(0,0,1;1.5708rad)
  Radius = 5
  SecondAngle = 0
FEATURE [Part::Cylinder] Cylinder018  label="NitrogenChamber002"
  Angle = 360
  AttacherType = Attacher::AttachEngine3D
  FirstAngle = 0
  Height = 20
  Placement = pos=(0,17,14.5) rot=(0,1,0;1.5708rad)
  Radius = 5
  SecondAngle = 0
FEATURE [Part::Cylinder] Cylinder019  label="NitrogenChamber003"
  Angle = 360
  AttacherType = Attacher::AttachEngine3D
  FirstAngle = 0
  Height = 20
  Placement = pos=(0,17,35.5) rot=(0,1,0;1.5708rad)
  Radius = 5
  SecondAngle = 0
FEATURE [Part::MultiFuse] Fusion006  label="NitrogenChamber"
  Shapes = -> [Cylinder017,Cylinder018,Cylinder019]
FEATURE [Part::Cut] Cut014
  Base = -> Cut011
  Tool = -> Fusion006
FEATURE [Part::Box] Box008  label="Cube008"
  AttacherType = Attacher::AttachEngine3D
  Height = 10
  Length = 10
  Placement = pos=(-7,0,0) rot=(0,1,0;0.785398rad)
  Width = 34
FEATURE [Part::Cut] Cut015
  Base = -> Cut014
  Tool = -> Box008
FEATURE [Part::Cylinder] Cylinder020
  Angle = 360
  AttacherType = Attacher::AttachEngine3D
  FirstAngle = 0
  Height = 20
  Placement = pos=(0,4.5,0) rot=(0,1,0;0.785398rad)
  Radius = 1.65
  SecondAngle = 0
FEATURE [Part::Cylinder] Cylinder021
  Angle = 360
  AttacherType = Attacher::AttachEngine3D
  FirstAngle = 0
  Height = 20
  Placement = pos=(0,29.5,0) rot=(0,1,0;0.785398rad)
  Radius = 1.65
  SecondAngle = 0
FEATURE [Part::MultiFuse] Fusion007  label="M4Screws"
  Shapes = -> [Cylinder020,Cylinder021]
FEATURE [Part::Cut] Cut016
  Base = -> Cut015
  Tool = -> Fusion007
FEATURE [Part::Cylinder] Cylinder022
  Angle = 360
  AttacherType = Attacher::AttachEngine3D
  FirstAngle = 0
  Height = 48
  Placement = pos=(0,5,26) rot=(0,1,0;1.5708rad)
  Radius = 1.5
  SecondAngle = 0
FEATURE [Part::Cylinder] Cylinder023
  Angle = 360
  AttacherType = Attacher::AttachEngine3D
  FirstAngle = 0
  Height = 48
  Placement = pos=(0,29,26) rot=(0,1,0;1.5708rad)
  Radius = 1.5
  SecondAngle = 0
FEATURE [Part::MultiFuse] Fusion008  label="CableDrillHole"
  Shapes = -> [Cylinder022,Cylinder023]
FEATURE [Part::Cut] Cut017  label="Cryostage"
  Base = -> Cut016
  Tool = -> Fusion008
FEATURE [Part::Compound] Compound001  label="StageAssembly"
  Links = -> [Cut013,Cut017]
  Placement = pos=(-51.5,-17,0) rot=(0,0,1;0rad)
---- part PhilippsXL30_FlangeToCF35_CF40_ZeroLengthAdapter_100.FCStd = doc fcstd_4c3f1db17545 ----
FCSTD DOCUMENT  (FreeCAD 0.20R29603 (Git))
Label: PhilippsXL30_FlangeToCF35_CF40_ZeroLengthAdapter_100
License: All rights reserved
LicenseURL: http://en.wikipedia.org/wiki/All_rights_reserved
objects: TechDraw::DrawViewDimension×26, Part::Cylinder×5, TechDraw::DrawProjGroupItem×4, Part::Compound×3, Part::Cut×3, TechDraw::DrawSVGTemplate×2, TechDraw::DrawProjGroup×2, TechDraw::DrawPage×2, Part::Feature×1, App::Link×1, Part::MultiFuse×1, TechDraw::DrawViewSection×1
note: 13 computed .brp shape members not serialized (recipe doc carries the construction recipe); baked Part::Feature solids carry a one-line shape summary decoded from their .brp
EXTERNAL_REF file=PhilippsXL30_Blindflange_100.FCStd obj=Cut001_solid001

FEATURE [Part::Feature] Solid  label="CF35 Flange"
  Placement = pos=(0,0,4.6) rot=(1,0,0;1.5708rad)
  shape: bbox 70 x 70 x 12.7 mm, 58 faces (baked)
FEATURE [Part::Cylinder] Cylinder004  label="Zylinder004"
  Angle = 360
  AttacherType = Attacher::AttachEngine3D
  FirstAngle = 0
  Height = 12
  Placement = pos=(42.5,0,7) rot=(0,0,1;0rad)
  Radius = 5
  SecondAngle = 0
FEATURE [Part::Cylinder] Cylinder005  label="Zylinder005"
  Angle = 360
  AttacherType = Attacher::AttachEngine3D
  FirstAngle = 0
  Height = 12
  Placement = pos=(42.5,0,7) rot=(0,0,1;0rad)
  Radius = 5
  SecondAngle = 0
FEATURE [Part::Compound] Compound
  Links = -> [Cylinder005]
  Placement = pos=(0,0,0) rot=(0,0,1;2.0944rad)
FEATURE [Part::Cylinder] Cylinder006  label="Zylinder006"
  Angle = 360
  AttacherType = Attacher::AttachEngine3D
  FirstAngle = 0
  Height = 12
  Placement = pos=(42.5,0,7) rot=(0,0,1;0rad)
  Radius = 5
  SecondAngle = 0
FEATURE [Part::Compound] Compound001
  Links = -> [Cylinder006]
  Placement = pos=(0,0,0) rot=(0,0,1;4.18879rad)
FEATURE [Part::Compound] Compound002
  Links = -> [Compound001,Cylinder004,Compound]
FEATURE [Part::Cut] Cut
  Base = -> Solid
  Tool = -> Compound002
FEATURE [Part::Cylinder] Cylinder  label="Zylinder"
  Angle = 360
  AttacherType = Attacher::AttachEngine3D
  FirstAngle = 0
  Height = 50
  Placement = pos=(0,0,-1) rot=(0,0,1;0rad)
  Radius = 20
  SecondAngle = 0
FEATURE [App::Link] Link001  label="Cut001 (Solid)001"
  LinkedObject = -> <external PhilippsXL30_Blindflange_100.FCStd>#Cut001_solid001
FEATURE [Part::Cylinder] Cylinder008  label="Zylinder008"
  Angle = 360
  AttacherType = Attacher::AttachEngine3D
  FirstAngle = 0
  Height = 12.5
  Placement = pos=(0,0,5) rot=(0,0,1;0rad)
  Radius = 34.95
  SecondAngle = 0
FEATURE [Part::Cut] Cut003
  Base = -> Link001
  Tool = -> Cylinder008
FEATURE [Part::MultiFuse] Fusion
  Shapes = -> [Cut,Cut003]
FEATURE [Part::Cut] Cut002
  Base = -> Fusion
  Tool = -> Cylinder
FEATURE [TechDraw::DrawSVGTemplate] Template
  EditableTexts = Designed_by_Name=Thomas Spielauer; FC-Date=2023-07-05; FC-SC=mm; FC-SH=01; FC-Title=Philips XL30 CF40 Adapter; Subtitle=100mm flange variant
  Height = 210
  Orientation = 1
  Width = 297
FEATURE [TechDraw::DrawProjGroupItem] ProjItem  label="Front"
  CoarseView = false
  Direction = (0,0,1)
  Focus = 100
  HardHidden = false
  IsoCount = 0
  IsoHidden = false
  IsoVisible = false
  LockPosition = true
  Perspective = false
  Rotation = 0
  RotationVector = (0,1,0)
  ScaleType = 2
  SeamHidden = false
  SeamVisible = true
  SmoothHidden = false
  SmoothVisible = true
  Source = -> [Cut002]
  Type = 0
  X = 0
  XDirection = (0,1,0)
  Y = 0
FEATURE [TechDraw::DrawProjGroupItem] ProjItem003  label="Top"
  CoarseView = false
  Direction = (-1,0,0)
  Focus = 100
  HardHidden = false
  IsoCount = 0
  IsoHidden = false
  IsoVisible = false
  LockPosition = false
  Perspective = false
  Rotation = 0
  RotationVector = (1,0,0)
  ScaleType = 2
  SeamHidden = false
  SeamVisible = true
  SmoothHidden = false
  SmoothVisible = true
  Source = -> [Cut002]
  Type = 4
  X = 0
  XDirection = (0,1,0)
  Y = -115
FEATURE [TechDraw::DrawViewDimension] Dimension007
  AngleOverride = false
  Arbitrary = false
  ArbitraryTolerances = false
  EqualTolerance = true
  ExtensionAngle = 0
  FormatSpec = R%.2w
  FormatSpecOverTolerance = %+.2w
  FormatSpecUnderTolerance = %+.2w
  Inverted = false
  LineAngle = 0
  LockPosition = false
  MeasureType = 1
  OverTolerance = 0
  References2D = -> [ProjItem]
  Rotation = 0
  ScaleType = 0
  TheoreticalExact = false
  Type = 4
  UnderTolerance = 0
  X = -1.26969
  Y = 60.8859
FEATURE [TechDraw::DrawViewDimension] Dimension012
  AngleOverride = false
  Arbitrary = false
  ArbitraryTolerances = false
  EqualTolerance = true
  ExtensionAngle = 0
  FormatSpec = ⌀%.2w
  FormatSpecOverTolerance = %+.2w
  FormatSpecUnderTolerance = %+.2w
  Inverted = false
  LineAngle = 0
  LockPosition = false
  MeasureType = 1
  OverTolerance = 0
  References2D = -> [ProjItem]
  Rotation = 0
  ScaleType = 0
  TheoreticalExact = false
  Type = 5
  UnderTolerance = 0
  X = 40.6138
  Y = 54.0598
FEATURE [TechDraw::DrawViewDimension] Dimension015
  AngleOverride = false
  Arbitrary = false
  ArbitraryTolerances = false
  EqualTolerance = true
  ExtensionAngle = 0
  FormatSpec = %.2w
  FormatSpecOverTolerance = %+.2w
  FormatSpecUnderTolerance = %+.2w
  Inverted = false
  LineAngle = 0
  LockPosition = false
  MeasureType = 1
  OverTolerance = 0
  References2D = -> [ProjItem]
  Rotation = 0
  ScaleType = 0
  TheoreticalExact = false
  Type = 0
  UnderTolerance = 0
  X = 58.2576
  Y = 40.308
FEATURE [TechDraw::DrawViewDimension] Dimension016
  AngleOverride = false
  Arbitrary = false
  ArbitraryTolerances = false
  EqualTolerance = true
  ExtensionAngle = 0
  FormatSpec = ⌀%.2w
  FormatSpecOverTolerance = %+.2w
  FormatSpecUnderTolerance = %+.2w
  Inverted = false
  LineAngle = 0
  LockPosition = false
  MeasureType = 1
  OverTolerance = 0
  References2D = -> [ProjItem]
  Rotation = 0
  ScaleType = 0
  TheoreticalExact = false
  Type = 5
  UnderTolerance = 0
  X = -52.3492
  Y = 45.3065
FEATURE [TechDraw::DrawViewDimension] Dimension017
  AngleOverride = false
  Arbitrary = false
  ArbitraryTolerances = false
  EqualTolerance = true
  ExtensionAngle = 0
  FormatSpec = ⌀%.2w (6x M6)
  FormatSpecOverTolerance = %+.2w
  FormatSpecUnderTolerance = %+.2w
  Inverted = false
  LineAngle = 0
  LockPosition = false
  MeasureType = 1
  OverTolerance = 0
  References2D = -> [ProjItem]
  Rotation = 0
  ScaleType = 0
  TheoreticalExact = false
  Type = 5
  UnderTolerance = 0
  X = -40.9728
  Y = 56.0349
FEATURE [TechDraw::DrawViewDimension] Dimension018
  AngleOverride = false
  Arbitrary = false
  ArbitraryTolerances = false
  EqualTolerance = true
  ExtensionAngle = 0
  FormatSpec = %.2w
  FormatSpecOverTolerance = %+.2w
  FormatSpecUnderTolerance = %+.2w
  Inverted = false
  LineAngle = 0
  LockPosition = false
  MeasureType = 1
  OverTolerance = 0
  References2D = -> [ProjItem003]
  Rotation = 0
  ScaleType = 0
  TheoreticalExact = false
  Type = 0
  UnderTolerance = 0
  X = -0.313919
  Y = -18.7458
FEATURE [TechDraw::DrawViewDimension] Dimension019
  AngleOverride = false
  Arbitrary = false
  ArbitraryTolerances = false
  EqualTolerance = true
  ExtensionAngle = 0
  FormatSpec = %.2w
  FormatSpecOverTolerance = %+.2w
  FormatSpecUnderTolerance = %+.2w
  Inverted = false
  LineAngle = 0
  LockPosition = false
  MeasureType = 1
  OverTolerance = 0
  References2D = -> [ProjItem003]
  Rotation = 0
  ScaleType = 0
  TheoreticalExact = false
  Type = 0
  UnderTolerance = 0
  X = 52.4225
  Y = -14.6035
FEATURE [TechDraw::DrawSVGTemplate] Template001
  EditableTexts = Designed_by_Name=Thomas Spielauer; FC-Date=2023-07-05; FC-SC=mm; FC-SH=02; FC-Title=Philips XL30 CF40 Adapter; Subtitle=100mm flange variant
  Height = 210
  Orientation = 1
  Width = 297
FEATURE [TechDraw::DrawProjGroupItem] ProjItem004  label="Front001"
  CoarseView = false
  Direction = (0,0,1)
  Focus = 100
  HardHidden = false
  IsoCount = 0
  IsoHidden = false
  IsoVisible = false
  LockPosition = true
  Perspective = false
  Rotation = 0
  RotationVector = (0,1,0)
  ScaleType = 2
  SeamHidden = false
  SeamVisible = true
  SmoothHidden = false
  SmoothVisible = true
  Source = -> [Cut002]
  Type = 0
  X = 0
  XDirection = (0,1,0)
  Y = 0
FEATURE [TechDraw::DrawProjGroup] ProjGroup001
  Anchor = -> ProjItem004
  AutoDistribute = true
  LockPosition = false
  ProjectionType = 0
  Rotation = 0
  ScaleType = 0
  Source = -> [Cut002]
  Views = -> [ProjItem004]
  X = 80.4015
  Y = 138.514
  spacingX = 15
  spacingY = 15
FEATURE [TechDraw::DrawViewSection] SectionView  label="Section  - "
  BaseView = -> ProjItem004
  CoarseView = false
  CutSurfaceDisplay = 2
  Direction = (0,-1,0)
  FileGeomPattern = <path>
  FileHatchPattern = <path>
  Focus = 100
  FuseBeforeCut = false
  HardHidden = false
  HatchScale = 1
  IsoCount = 0
  IsoHidden = false
  IsoVisible = false
  LockPosition = false
  NameGeomPattern = Diamond
  Perspective = false
  Rotation = 0
  ScaleType = 2
  SeamHidden = false
  SeamVisible = true
  SectionDirection = 0
  SectionNormal = (0,-1,0)
  SectionOrigin = (0,0,8.65)
  SmoothHidden = false
  SmoothVisible = true
  Source = -> [Cut002]
  X = 193.115
  XDirection = (0,0,1)
  Y = 128.608
FEATURE [TechDraw::DrawViewDimension] Dimension020
  AngleOverride = false
  Arbitrary = false
  ArbitraryTolerances = false
  EqualTolerance = true
  ExtensionAngle = 0
  FormatSpec = %.2w
  FormatSpecOverTolerance = %+.2w
  FormatSpecUnderTolerance = %+.2w
  Inverted = false
  LineAngle = 0
  LockPosition = false
  MeasureType = 1
  OverTolerance = 0
  References2D = -> [SectionView]
  Rotation = 0
  ScaleType = 0
  TheoreticalExact = false
  Type = 0
  UnderTolerance = 0
  X = -3.19245
  Y = 66.0613
FEATURE [TechDraw::DrawViewDimension] Dimension021
  AngleOverride = false
  Arbitrary = false
  ArbitraryTolerances = false
  EqualTolerance = true
  ExtensionAngle = 0
  FormatSpec = %.2w
  FormatSpecOverTolerance = %+.2w
  FormatSpecUnderTolerance = %+.2w
  Inverted = false
  LineAngle = 0
  LockPosition = false
  MeasureType = 1
  OverTolerance = 0
  References2D = -> [SectionView]
  Rotation = 0
  ScaleType = 0
  TheoreticalExact = false
  Type = 0
  UnderTolerance = 0
  X = 14.208
  Y = 60.5542
FEATURE [TechDraw::DrawViewDimension] Dimension022
  AngleOverride = false
  Arbitrary = false
  ArbitraryTolerances = false
  EqualTolerance = true
  ExtensionAngle = 0
  FormatSpec = %.2w
  FormatSpecOverTolerance = %+.2w
  FormatSpecUnderTolerance = %+.2w
  Inverted = false
  LineAngle = 0
  LockPosition = false
  MeasureType = 1
  OverTolerance = 0
  References2D = -> [SectionView]
  Rotation = 0
  ScaleType = 0
  TheoreticalExact = false
  Type = 0
  UnderTolerance = 0
  X = -20.8291
  Y = 47.7164
FEATURE [TechDraw::DrawViewDimension] Dimension023
  AngleOverride = false
  Arbitrary = false
  ArbitraryTolerances = false
  EqualTolerance = true
  ExtensionAngle = 0
  FormatSpec = %.2w
  FormatSpecOverTolerance = %+.2w
  FormatSpecUnderTolerance = %+.2w
  Inverted = false
  LineAngle = 0
  LockPosition = false
  MeasureType = 1
  OverTolerance = 0
  References2D = -> [SectionView]
  Rotation = 0
  ScaleType = 0
  TheoreticalExact = false
  Type = 0
  UnderTolerance = 0
  X = -36.0172
  Y = 38.6403
FEATURE [TechDraw::DrawViewDimension] Dimension024
  AngleOverride = false
  Arbitrary = false
  ArbitraryTolerances = false
  EqualTolerance = true
  ExtensionAngle = 0
  FormatSpec = %.2w
  FormatSpecOverTolerance = %+.2w
  FormatSpecUnderTolerance = %+.2w
  Inverted = false
  LineAngle = 0
  LockPosition = false
  MeasureType = 1
  OverTolerance = 0
  References2D = -> [SectionView]
  Rotation = 0
  ScaleType = 0
  TheoreticalExact = false
  Type = 0
  UnderTolerance = 0
  X = -21.915
  Y = 18.1567
FEATURE [TechDraw::DrawViewDimension] Dimension025
  AngleOverride = false
  Arbitrary = false
  ArbitraryTolerances = false
  EqualTolerance = true
  ExtensionAngle = 0
  FormatSpec = %.2w
  FormatSpecOverTolerance = %+.2w
  FormatSpecUnderTolerance = %+.2w
  Inverted = false
  LineAngle = 0
  LockPosition = false
  MeasureType = 1
  OverTolerance = 0
  References2D = -> [SectionView]
  Rotation = 0
  ScaleType = 0
  TheoreticalExact = false
  Type = 0
  UnderTolerance = 0
  X = -13.979
  Y = -60.471
FEATURE [TechDraw::DrawViewDimension] Dimension026
  AngleOverride = false
  Arbitrary = false
  ArbitraryTolerances = false
  EqualTolerance = true
  ExtensionAngle = 0
  FormatSpec = %.2w
  FormatSpecOverTolerance = %+.2w
  FormatSpecUnderTolerance = %+.2w
  Inverted = false
  LineAngle = 0
  LockPosition = false
  MeasureType = 1
  OverTolerance = 0
  References2D = -> [SectionView]
  Rotation = 0
  ScaleType = 0
  TheoreticalExact = false
  Type = 0
  UnderTolerance = 0
  X = 14.3909
  Y = -57.6165
FEATURE [TechDraw::DrawViewDimension] Dimension027
  AngleOverride = false
  Arbitrary = false
  ArbitraryTolerances = false
  EqualTolerance = true
  ExtensionAngle = 0
  FormatSpec = %.2w (CF40 knife edge)
  FormatSpecOverTolerance = %+.2w
  FormatSpecUnderTolerance = %+.2w
  Inverted = false
  LineAngle = 0
  LockPosition = false
  MeasureType = 1
  OverTolerance = 0
  References2D = -> [SectionView]
  Rotation = 0
  ScaleType = 0
  TheoreticalExact = false
  Type = 0
  UnderTolerance = 0
  X = 51.4939
  Y = 1.25347
FEATURE [TechDraw::DrawViewDimension] Dimension028
  AngleOverride = false
  Arbitrary = false
  ArbitraryTolerances = false
  EqualTolerance = true
  ExtensionAngle = 0
  FormatSpec = %.2w
  FormatSpecOverTolerance = %+.2w
  FormatSpecUnderTolerance = %+.2w
  Inverted = false
  LineAngle = 0
  LockPosition = false
  MeasureType = 1
  OverTolerance = 0
  References2D = -> [SectionView]
  Rotation = 0
  ScaleType = 0
  TheoreticalExact = false
  Type = 0
  UnderTolerance = 0
  X = 35.1516
  Y = 5.12687
FEATURE [TechDraw::DrawPage] Page001
  KeepUpdated = true
  NextBalloonIndex = 1
  ProjectionType = 0
  Template = -> Template001
  Views = -> [ProjGroup001,SectionView,Dimension020,Dimension021,Dimension022,Dimension023,Dimension024,Dimension025,Dimension026,Dimension027,Dimension028]
FEATURE [TechDraw::DrawViewDimension] Dimension031
  AngleOverride = false
  Arbitrary = false
  ArbitraryTolerances = false
  EqualTolerance = true
  ExtensionAngle = 0
  FormatSpec = R%.2w
  FormatSpecOverTolerance = %+.2w
  FormatSpecUnderTolerance = %+.2w
  Inverted = false
  LineAngle = 0
  LockPosition = false
  MeasureType = 1
  OverTolerance = 0
  References2D = -> [ProjItem]
  Rotation = 0
  ScaleType = 0
  TheoreticalExact = false
  Type = 4
  UnderTolerance = 0
  X = -57.2589
  Y = -22.9275
FEATURE [TechDraw::DrawViewDimension] Dimension
  AngleOverride = false
  Arbitrary = false
  ArbitraryTolerances = false
  EqualTolerance = true
  ExtensionAngle = 0
  FormatSpec = %.2w
  FormatSpecOverTolerance = %+.2w
  FormatSpecUnderTolerance = %+.2w
  Inverted = false
  LineAngle = 0
  LockPosition = false
  MeasureType = 1
  OverTolerance = 0
  References2D = -> [ProjItem003]
  Rotation = 0
  ScaleType = 0
  TheoreticalExact = false
  Type = 0
  UnderTolerance = 0
  X = -0.678066
  Y = 30.3595
FEATURE [TechDraw::DrawViewDimension] Dimension032
  AngleOverride = false
  Arbitrary = false
  ArbitraryTolerances = false
  EqualTolerance = true
  ExtensionAngle = 0
  FormatSpec = %.2w
  FormatSpecOverTolerance = %+.2w
  FormatSpecUnderTolerance = %+.2w
  Inverted = false
  LineAngle = 0
  LockPosition = false
  MeasureType = 1
  OverTolerance = 0
  References2D = -> [ProjItem003]
  Rotation = 0
  ScaleType = 0
  TheoreticalExact = false
  Type = 0
  UnderTolerance = 0
  X = -61.7531
  Y = 5.37362
FEATURE [TechDraw::DrawProjGroupItem] ProjItem001  label="Rear"
  CoarseView = false
  Direction = (0,0,-1)
  Focus = 100
  HardHidden = false
  IsoCount = 0
  IsoHidden = false
  IsoVisible = false
  LockPosition = false
  Perspective = false
  Rotation = 0
  RotationVector = (1,0,0)
  ScaleType = 2
  SeamHidden = false
  SeamVisible = true
  SmoothHidden = false
  SmoothVisible = true
  Source = -> [Cut002]
  Type = 3
  X = 115
  XDirection = (0,-1,0)
  Y = 0
FEATURE [TechDraw::DrawProjGroup] ProjGroup
  Anchor = -> ProjItem
  AutoDistribute = true
  LockPosition = false
  ProjectionType = 0
  Rotation = 0
  ScaleType = 0
  Source = -> [Cut002]
  Views = -> [ProjItem,ProjItem001,ProjItem003]
  X = 76.1231
  Y = 135.662
  spacingX = 15
  spacingY = 15
FEATURE [TechDraw::DrawViewDimension] Dimension003
  AngleOverride = false
  Arbitrary = false
  ArbitraryTolerances = false
  EqualTolerance = true
  ExtensionAngle = 0
  FormatSpec = ⌀%.2w
  FormatSpecOverTolerance = %+.2w
  FormatSpecUnderTolerance = %+.2w
  Inverted = false
  LineAngle = 0
  LockPosition = false
  MeasureType = 1
  OverTolerance = 0
  References2D = -> [ProjItem001]
  Rotation = 0
  ScaleType = 0
  TheoreticalExact = false
  Type = 5
  UnderTolerance = 0
  X = 37.3868
  Y = 50.5334
FEATURE [TechDraw::DrawViewDimension] Dimension004
  AngleOverride = false
  Arbitrary = false
  ArbitraryTolerances = false
  EqualTolerance = true
  ExtensionAngle = 0
  FormatSpec = ⌀%.2w
  FormatSpecOverTolerance = %+.2w
  FormatSpecUnderTolerance = %+.2w
  Inverted = false
  LineAngle = 0
  LockPosition = false
  MeasureType = 1
  OverTolerance = 0
  References2D = -> [ProjItem001]
  Rotation = 0
  ScaleType = 0
  TheoreticalExact = false
  Type = 5
  UnderTolerance = 0
  X = 44.0719
  Y = 46.338
FEATURE [TechDraw::DrawViewDimension] Dimension005
  AngleOverride = false
  Arbitrary = false
  ArbitraryTolerances = false
  EqualTolerance = true
  ExtensionAngle = 0
  FormatSpec = ⌀%.2w
  FormatSpecOverTolerance = %+.2w
  FormatSpecUnderTolerance = %+.2w
  Inverted = false
  LineAngle = 0
  LockPosition = false
  MeasureType = 1
  OverTolerance = 0
  References2D = -> [ProjItem001]
  Rotation = 0
  ScaleType = 0
  TheoreticalExact = false
  Type = 5
  UnderTolerance = 0
  X = 48.9256
  Y = 41.6983
FEATURE [TechDraw::DrawViewDimension] Dimension008
  AngleOverride = false
  Arbitrary = false
  ArbitraryTolerances = false
  EqualTolerance = true
  ExtensionAngle = 0
  FormatSpec = %.2w
  FormatSpecOverTolerance = %+.2w
  FormatSpecUnderTolerance = %+.2w
  Inverted = false
  LineAngle = 0
  LockPosition = false
  MeasureType = 1
  OverTolerance = 0
  References2D = -> [ProjItem001]
  Rotation = 0
  ScaleType = 0
  TheoreticalExact = false
  Type = 6
  UnderTolerance = 0
  X = 57.7233
  Y = -33.2236
FEATURE [TechDraw::DrawViewDimension] Dimension010
  AngleOverride = false
  Arbitrary = false
  ArbitraryTolerances = false
  EqualTolerance = true
  ExtensionAngle = 0
  FormatSpec = ⌀%.2w (3x)
  FormatSpecOverTolerance = %+.2w
  FormatSpecUnderTolerance = %+.2w
  Inverted = false
  LineAngle = 0
  LockPosition = false
  MeasureType = 1
  OverTolerance = 0
  References2D = -> [ProjItem001]
  Rotation = 0
  ScaleType = 0
  TheoreticalExact = false
  Type = 5
  UnderTolerance = 0
  X = -39.5129
  Y = 51.575
FEATURE [TechDraw::DrawViewDimension] Dimension011
  AngleOverride = false
  Arbitrary = false
  ArbitraryTolerances = false
  EqualTolerance = true
  ExtensionAngle = 0
  FormatSpec = ⌀%.2w
  FormatSpecOverTolerance = %+.2w
  FormatSpecUnderTolerance = %+.2w
  Inverted = false
  LineAngle = 0
  LockPosition = false
  MeasureType = 1
  OverTolerance = 0
  References2D = -> [ProjItem001]
  Rotation = 0
  ScaleType = 0
  TheoreticalExact = false
  Type = 5
  UnderTolerance = 0
  X = -20.9799
  Y = -22.9677
FEATURE [TechDraw::DrawViewDimension] Dimension033
  AngleOverride = false
  Arbitrary = false
  ArbitraryTolerances = false
  EqualTolerance = true
  ExtensionAngle = 0
  FormatSpec = R%.2w
  FormatSpecOverTolerance = %+.2w
  FormatSpecUnderTolerance = %+.2w
  Inverted = false
  LineAngle = 0
  LockPosition = false
  MeasureType = 1
  OverTolerance = 0
  References2D = -> [ProjItem001]
  Rotation = 0
  ScaleType = 0
  TheoreticalExact = false
  Type = 4
  UnderTolerance = 0
  X = 19.2921
  Y = -12.3401
FEATURE [TechDraw::DrawPage] Page
  KeepUpdated = true
  NextBalloonIndex = 1
  ProjectionType = 0
  Template = -> Template
  Views = -> [ProjGroup,Dimension003,Dimension004,Dimension005,Dimension007,Dimension008,Dimension010,Dimension011,Dimension012,Dimension015,Dimension016,Dimension017,Dimension018,Dimension019,Dimension031,Dimension,Dimension032,Dimension033]
note: 2 file-system paths scrubbed to <path> (originals preserved in the JSON sidecar)
---- part PhilippsXL30_FlangeToCF63_ZeroLengthAdapter_120.FCStd = doc fcstd_f7e8bb032a80 ----
FCSTD DOCUMENT  (FreeCAD 0.21R33675 (Git))
Label: PhilippsXL30_FlangeToCF63_ZeroLengthAdapter_100
License: All rights reserved
LicenseURL: http://en.wikipedia.org/wiki/All_rights_reserved
objects: TechDraw::DrawViewDimension×32, Part::Cylinder×5, Part::MultiFuse×5, Part::Box×3, Part::Feature×3, Part::Compound×3, TechDraw::DrawProjGroupItem×3, TechDraw::DrawSVGTemplate×2, Part::Cut×2, TechDraw::DrawPage×2, App::Link×1, TechDraw::DrawProjGroup×1, TechDraw::DrawViewPart×1, TechDraw::DrawViewSection×1
note: 65 computed .brp shape members not serialized (recipe doc carries the construction recipe); baked Part::Feature solids carry a one-line shape summary decoded from their .brp
EXTERNAL_REF file=PhilippsXL30_Blindflange_120.FCStd obj=Cut003

FEATURE [App::Link] Link  label="Cut003"
  LinkedObject = -> <external PhilippsXL30_Blindflange_120.FCStd>#Cut003
FEATURE [Part::Box] Box  label="Würfel"
  AttacherType = Attacher::AttachEngine3D
  Height = 24
  Length = 10
  Placement = pos=(54.5,-6,5) rot=(0,0,1;0rad)
  Width = 12
FEATURE [Part::Cylinder] Cylinder  label="Zylinder"
  Angle = 360
  AttacherType = Attacher::AttachEngine3D
  FirstAngle = 0
  Height = 24
  Placement = pos=(54.5,0,5) rot=(0,0,1;0rad)
  Radius = 6
  SecondAngle = 0
FEATURE [Part::Box] Box001  label="Würfel001"
  AttacherType = Attacher::AttachEngine3D
  Height = 24
  Length = 10
  Placement = pos=(54.5,-6,5) rot=(0,0,1;0rad)
  Width = 12
FEATURE [Part::Cylinder] Cylinder001  label="Zylinder001"
  Angle = 360
  AttacherType = Attacher::AttachEngine3D
  FirstAngle = 0
  Height = 24
  Placement = pos=(54.5,0,5) rot=(0,0,1;0rad)
  Radius = 6
  SecondAngle = 0
FEATURE [Part::Box] Box002  label="Würfel002"
  AttacherType = Attacher::AttachEngine3D
  Height = 24
  Length = 10
  Placement = pos=(54.5,-6,5) rot=(0,0,1;0rad)
  Width = 12
FEATURE [Part::Cylinder] Cylinder002  label="Zylinder002"
  Angle = 360
  AttacherType = Attacher::AttachEngine3D
  FirstAngle = 0
  Height = 24
  Placement = pos=(54.5,0,5) rot=(0,0,1;0rad)
  Radius = 6
  SecondAngle = 0
FEATURE [Part::Feature] Link_solid  label="Cut003 (Solid)"
  shape: bbox 120 x 120 x 11 mm, 31 faces (baked)
FEATURE [Part::MultiFuse] Fusion001
  Shapes = -> [Box,Cylinder]
FEATURE [Part::MultiFuse] Fusion002
  Placement = pos=(0,0,0) rot=(0,0,1;2.0944rad)
  Shapes = -> [Box001,Cylinder001]
FEATURE [Part::MultiFuse] Fusion003
  Placement = pos=(0,0,0) rot=(0,0,1;4.18879rad)
  Shapes = -> [Box002,Cylinder002]
FEATURE [Part::Compound] Compound001
  Links = -> [Fusion001,Fusion002,Fusion003]
FEATURE [Part::Cylinder] Cylinder003  label="Zylinder003"
  Angle = 360
  AttacherType = Attacher::AttachEngine3D
  FirstAngle = 0
  Height = 23.5
  Placement = pos=(46.1,0,5) rot=(0,0,1;0rad)
  Radius = 4.8
  SecondAngle = 0
FEATURE [Part::Compound] Compound002
  Links = -> [Cylinder003]
  Placement = pos=(0,0,0) rot=(0,0,1;4.18879rad)
FEATURE [Part::Cylinder] Cylinder004  label="Zylinder004"
  Angle = 360
  AttacherType = Attacher::AttachEngine3D
  FirstAngle = 0
  Height = 50
  Radius = 35
  SecondAngle = 0
FEATURE [TechDraw::DrawSVGTemplate] Template
  EditableTexts = Designed_by_Name=Thomas Spielauer; FC-Date=2023-11-08; FC-SC=mm; FC-SH=1/2; FC-Title=120mm to CF63 adapter; Subtitle=XL30 ESEM compatible
  Height = 210
  Orientation = 1
  Template = <path>
  Width = 297
FEATURE [Part::Feature] Part__Feature001  label="Hositrad_CF63-BT"
  Placement = pos=(0,0,28.5) rot=(1,0,0;1.5708rad)
  shape: bbox 113.5 x 113.5 x 17.5 mm, 71 faces (baked)
FEATURE [Part::Compound] Compound
  Links = -> [Part__Feature001]
  Placement = pos=(0,0,0) rot=(0,0,1;0.261799rad)
FEATURE [Part::MultiFuse] Fusion
  Shapes = -> [Link_solid,Compound]
FEATURE [Part::Feature] Fusion_solid001  label="Fusion (Solid)001"
  shape: bbox 120 x 120 x 28.5 mm, 114 faces (baked)
FEATURE [Part::MultiFuse] Fusion004
  Shapes = -> [Compound002,Fusion_solid001]
FEATURE [Part::Cut] Cut
  Base = -> Fusion004
  Tool = -> Compound001
FEATURE [Part::Cut] Cut001
  Base = -> Cut
  Tool = -> Cylinder004
FEATURE [TechDraw::DrawProjGroupItem] ProjItem  label="Front"
  CoarseView = false
  Direction = (0,0,-1)
  Focus = 100
  HardHidden = false
  IsoCount = 0
  IsoHidden = false
  IsoVisible = false
  LockPosition = true
  Perspective = false
  Rotation = 0
  RotationVector = (0,1,0)
  Scale = 0.666667
  ScaleType = 2
  ScrubCount = 0
  SeamHidden = false
  SeamVisible = false
  SmoothHidden = false
  SmoothVisible = true
  Source = -> [Cut001]
  Type = 0
  X = 0
  XDirection = (0,1,0)
  Y = 0
FEATURE [TechDraw::DrawProjGroupItem] ProjItem001  label="Rear"
  CoarseView = false
  Direction = (0,0,1)
  Focus = 100
  HardHidden = false
  IsoCount = 0
  IsoHidden = false
  IsoVisible = false
  LockPosition = false
  Perspective = false
  Rotation = 0
  RotationVector = (1,0,0)
  Scale = 0.666667
  ScaleType = 2
  ScrubCount = 0
  SeamHidden = false
  SeamVisible = false
  SmoothHidden = false
  SmoothVisible = true
  Source = -> [Cut001]
  Type = 3
  X = 103.585
  XDirection = (0,-1,0)
  Y = 0
FEATURE [TechDraw::DrawProjGroupItem] ProjItem002  label="Top"
  CoarseView = false
  Direction = (1,0,0)
  Focus = 100
  HardHidden = false
  IsoCount = 0
  IsoHidden = false
  IsoVisible = false
  LockPosition = false
  Perspective = false
  Rotation = 0
  RotationVector = (1,0,0)
  Scale = 0.666667
  ScaleType = 2
  ScrubCount = 0
  SeamHidden = false
  SeamVisible = false
  SmoothHidden = false
  SmoothVisible = true
  Source = -> [Cut001]
  Type = 4
  X = 0
  XDirection = (0,1,0)
  Y = -91.1591
FEATURE [TechDraw::DrawProjGroup] ProjGroup
  Anchor = -> ProjItem
  AutoDistribute = false
  LockPosition = false
  ProjectionType = 0
  Rotation = 0
  Scale = 0.666667
  ScaleType = 2
  Source = -> [Cut001]
  Views = -> [ProjItem,ProjItem001,ProjItem002]
  X = 86.4871
  Y = 141.809
  spacingX = 15
  spacingY = 15
FEATURE [TechDraw::DrawViewDimension] Dimension
  AngleOverride = false
  Arbitrary = false
  ArbitraryTolerances = false
  EqualTolerance = true
  ExtensionAngle = 0
  FormatSpec = ⌀%.2w
  FormatSpecOverTolerance = %+.2w
  FormatSpecUnderTolerance = %+.2w
  Inverted = false
  LineAngle = 0
  LockPosition = false
  MeasureType = 1
  OverTolerance = 0
  References2D = -> [ProjItem]
  Rotation = 0
  ScaleType = 0
  TheoreticalExact = false
  Type = 5
  UnderTolerance = 0
  X = 13.273
  Y = 49.9319
FEATURE [TechDraw::DrawViewDimension] Dimension001
  AngleOverride = false
  Arbitrary = false
  ArbitraryTolerances = false
  EqualTolerance = true
  ExtensionAngle = 0
  FormatSpec = ⌀%.2w
  FormatSpecOverTolerance = %+.2w
  FormatSpecUnderTolerance = %+.2w
  Inverted = false
  LineAngle = 0
  LockPosition = false
  MeasureType = 1
  OverTolerance = 0
  References2D = -> [ProjItem]
  Rotation = 0
  ScaleType = 0
  TheoreticalExact = false
  Type = 5
  UnderTolerance = 0
  X = 24.0179
  Y = 47.193
FEATURE [TechDraw::DrawViewDimension] Dimension002
  AngleOverride = false
  Arbitrary = false
  ArbitraryTolerances = false
  EqualTolerance = true
  ExtensionAngle = 0
  FormatSpec = ⌀%.2w
  FormatSpecOverTolerance = %+.2w
  FormatSpecUnderTolerance = %+.2w
  Inverted = false
  LineAngle = 0
  LockPosition = false
  MeasureType = 1
  OverTolerance = 0
  References2D = -> [ProjItem]
  Rotation = 0
  ScaleType = 0
  TheoreticalExact = false
  Type = 5
  UnderTolerance = 0
  X = 30.1277
  Y = 42.7687
FEATURE [TechDraw::DrawViewDimension] Dimension003
  AngleOverride = false
  Arbitrary = false
  ArbitraryTolerances = false
  EqualTolerance = true
  ExtensionAngle = 0
  FormatSpec = ⌀%.2w
  FormatSpecOverTolerance = %+.2w
  FormatSpecUnderTolerance = %+.2w
  Inverted = false
  LineAngle = 0
  LockPosition = false
  MeasureType = 1
  OverTolerance = 0
  References2D = -> [ProjItem]
  Rotation = 0
  ScaleType = 0
  TheoreticalExact = false
  Type = 5
  UnderTolerance = 0
  X = 35.1841
  Y = 34.552
FEATURE [TechDraw::DrawViewDimension] Dimension004
  AngleOverride = false
  Arbitrary = false
  ArbitraryTolerances = false
  EqualTolerance = true
  ExtensionAngle = 0
  FormatSpec = ⌀%.2w
  FormatSpecOverTolerance = %+.2w
  FormatSpecUnderTolerance = %+.2w
  Inverted = false
  LineAngle = 0
  LockPosition = false
  MeasureType = 1
  OverTolerance = 0
  References2D = -> [ProjItem]
  Rotation = 0
  ScaleType = 0
  TheoreticalExact = false
  Type = 5
  UnderTolerance = 0
  X = 47.761
  Y = 10.7853
FEATURE [TechDraw::DrawViewDimension] Dimension005
  AngleOverride = false
  Arbitrary = false
  ArbitraryTolerances = false
  EqualTolerance = true
  ExtensionAngle = 0
  FormatSpec = %.2w
  FormatSpecOverTolerance = %+.2w
  FormatSpecUnderTolerance = %+.2w
  Inverted = false
  LineAngle = 0
  LockPosition = false
  MeasureType = 1
  OverTolerance = 0
  References2D = -> [ProjItem]
  Rotation = 0
  ScaleType = 0
  TheoreticalExact = false
  Type = 6
  UnderTolerance = 0
  X = 30.5032
  Y = -36.3658
FEATURE [TechDraw::DrawViewDimension] Dimension006
  AngleOverride = false
  Arbitrary = false
  ArbitraryTolerances = false
  EqualTolerance = true
  ExtensionAngle = 0
  FormatSpec = ⌀%.2w (3x)
  FormatSpecOverTolerance = %+.2w
  FormatSpecUnderTolerance = %+.2w
  Inverted = false
  LineAngle = 0
  LockPosition = false
  MeasureType = 1
  OverTolerance = 0
  References2D = -> [ProjItem]
  Rotation = 0
  ScaleType = 0
  TheoreticalExact = false
  Type = 5
  UnderTolerance = 0
  X = -27.3798
  Y = 53.7456
FEATURE [TechDraw::DrawViewDimension] Dimension007
  AngleOverride = false
  Arbitrary = false
  ArbitraryTolerances = false
  EqualTolerance = true
  ExtensionAngle = 0
  FormatSpec = ⌀%.2w
  FormatSpecOverTolerance = %+.2w
  FormatSpecUnderTolerance = %+.2w
  Inverted = false
  LineAngle = 0
  LockPosition = false
  MeasureType = 1
  OverTolerance = 0
  References2D = -> [ProjItem001]
  Rotation = 0
  ScaleType = 0
  TheoreticalExact = false
  Type = 5
  UnderTolerance = 0
  X = 51.25
  Y = 21.5576
FEATURE [TechDraw::DrawViewDimension] Dimension008
  AngleOverride = false
  Arbitrary = false
  ArbitraryTolerances = false
  EqualTolerance = true
  ExtensionAngle = 0
  FormatSpec = ⌀%.2w (CF63 knife)
  FormatSpecOverTolerance = %+.2w
  FormatSpecUnderTolerance = %+.2w
  Inverted = false
  LineAngle = 0
  LockPosition = false
  MeasureType = 1
  OverTolerance = 0
  References2D = -> [ProjItem001]
  Rotation = 0
  ScaleType = 0
  TheoreticalExact = false
  Type = 5
  UnderTolerance = 0
  X = 68.2486
  Y = 15.1076
FEATURE [TechDraw::DrawViewDimension] Dimension010
  AngleOverride = false
  Arbitrary = false
  ArbitraryTolerances = false
  EqualTolerance = true
  ExtensionAngle = 0
  FormatSpec = ⌀%.2w
  FormatSpecOverTolerance = %+.2w
  FormatSpecUnderTolerance = %+.2w
  Inverted = false
  LineAngle = 0
  LockPosition = false
  MeasureType = 1
  OverTolerance = 0
  References2D = -> [ProjItem001]
  Rotation = 0
  ScaleType = 0
  TheoreticalExact = false
  Type = 5
  UnderTolerance = 0
  X = 50.7383
  Y = -4.01857
FEATURE [TechDraw::DrawViewDimension] Dimension011
  AngleOverride = false
  Arbitrary = false
  ArbitraryTolerances = false
  EqualTolerance = true
  ExtensionAngle = 0
  FormatSpec = ⌀%+2w (7x M8)
  FormatSpecOverTolerance = %+.2w
  FormatSpecUnderTolerance = %+.2w
  Inverted = false
  LineAngle = 0
  LockPosition = false
  MeasureType = 1
  OverTolerance = 0
  References2D = -> [ProjItem001]
  Rotation = 0
  ScaleType = 0
  TheoreticalExact = false
  Type = 5
  UnderTolerance = 0
  X = 44.1386
  Y = 45.7398
FEATURE [TechDraw::DrawViewDimension] Dimension012
  AngleOverride = false
  Arbitrary = false
  ArbitraryTolerances = false
  EqualTolerance = true
  ExtensionAngle = 0
  FormatSpec = ⌀%.2w (ignore)
  FormatSpecOverTolerance = %+.2w
  FormatSpecUnderTolerance = %+.2w
  Inverted = false
  LineAngle = 0
  LockPosition = false
  MeasureType = 1
  OverTolerance = 0
  References2D = -> [ProjItem001]
  Rotation = 0
  ScaleType = 0
  TheoreticalExact = false
  Type = 5
  UnderTolerance = 0
  X = 56.2438
  Y = -18.0288
FEATURE [TechDraw::DrawViewDimension] Dimension013
  AngleOverride = false
  Arbitrary = false
  ArbitraryTolerances = false
  EqualTolerance = true
  ExtensionAngle = 0
  FormatSpec = ⌀%.2w (CF63 knife)
  FormatSpecOverTolerance = %+.2w
  FormatSpecUnderTolerance = %+.2w
  Inverted = false
  LineAngle = 0
  LockPosition = false
  MeasureType = 1
  OverTolerance = 0
  References2D = -> [ProjItem001]
  Rotation = 0
  ScaleType = 0
  TheoreticalExact = false
  Type = 5
  UnderTolerance = 0
  X = 69.1563
  Y = 3.81479
FEATURE [TechDraw::DrawViewDimension] Dimension014
  AngleOverride = false
  Arbitrary = false
  ArbitraryTolerances = false
  EqualTolerance = true
  ExtensionAngle = 0
  FormatSpec = ⌀%.2w
  FormatSpecOverTolerance = %+.2w
  FormatSpecUnderTolerance = %+.2w
  Inverted = false
  LineAngle = 0
  LockPosition = false
  MeasureType = 1
  OverTolerance = 0
  References2D = -> [ProjItem001]
  Rotation = 0
  ScaleType = 0
  TheoreticalExact = false
  Type = 5
  UnderTolerance = 0
  X = -46.1176
  Y = -23.6426
FEATURE [TechDraw::DrawViewDimension] Dimension015
  AngleOverride = false
  Arbitrary = false
  ArbitraryTolerances = false
  EqualTolerance = true
  ExtensionAngle = 0
  FormatSpec = ⌀%.2w
  FormatSpecOverTolerance = %+.2w
  FormatSpecUnderTolerance = %+.2w
  Inverted = false
  LineAngle = 0
  LockPosition = false
  MeasureType = 1
  OverTolerance = 0
  References2D = -> [ProjItem001]
  Rotation = 0
  ScaleType = 0
  TheoreticalExact = false
  Type = 5
  UnderTolerance = 0
  X = 58.2576
  Y = 40.308
FEATURE [TechDraw::DrawViewDimension] Dimension016
  AngleOverride = false
  Arbitrary = false
  ArbitraryTolerances = false
  EqualTolerance = true
  ExtensionAngle = 0
  FormatSpec = %.2w
  FormatSpecOverTolerance = %+.2w
  FormatSpecUnderTolerance = %+.2w
  Inverted = false
  LineAngle = 0
  LockPosition = false
  MeasureType = 1
  OverTolerance = 0
  References2D = -> [ProjItem001]
  Rotation = 0
  ScaleType = 0
  TheoreticalExact = false
  Type = 1
  UnderTolerance = 0
  X = 8.90961
  Y = 48.6597
FEATURE [TechDraw::DrawViewDimension] Dimension017
  AngleOverride = false
  Arbitrary = false
  ArbitraryTolerances = false
  EqualTolerance = true
  ExtensionAngle = 0
  FormatSpec = %.2w
  FormatSpecOverTolerance = %+.2w
  FormatSpecUnderTolerance = %+.2w
  Inverted = false
  LineAngle = 0
  LockPosition = false
  MeasureType = 1
  OverTolerance = 0
  References2D = -> [ProjItem002]
  Rotation = 0
  ScaleType = 0
  TheoreticalExact = false
  Type = 2
  UnderTolerance = 0
  X = -47.0367
  Y = -10.6679
FEATURE [TechDraw::DrawViewDimension] Dimension018
  AngleOverride = false
  Arbitrary = false
  ArbitraryTolerances = false
  EqualTolerance = true
  ExtensionAngle = 0
  FormatSpec = %.2w
  FormatSpecOverTolerance = %+.2w
  FormatSpecUnderTolerance = %+.2w
  Inverted = false
  LineAngle = 0
  LockPosition = false
  MeasureType = 1
  OverTolerance = 0
  References2D = -> [ProjItem002]
  Rotation = 0
  ScaleType = 0
  TheoreticalExact = false
  Type = 2
  UnderTolerance = 0
  X = -56.6562
  Y = 19.2142
FEATURE [TechDraw::DrawViewDimension] Dimension019
  AngleOverride = false
  Arbitrary = false
  ArbitraryTolerances = false
  EqualTolerance = true
  ExtensionAngle = 0
  FormatSpec = %.2w
  FormatSpecOverTolerance = %+.2w
  FormatSpecUnderTolerance = %+.2w
  Inverted = false
  LineAngle = 0
  LockPosition = false
  MeasureType = 1
  OverTolerance = 0
  References2D = -> [ProjItem002]
  Rotation = 0
  ScaleType = 0
  TheoreticalExact = false
  Type = 1
  UnderTolerance = 0
  X = 52.4225
  Y = -14.6035
FEATURE [TechDraw::DrawViewDimension] Dimension020
  AngleOverride = false
  Arbitrary = false
  ArbitraryTolerances = false
  EqualTolerance = true
  ExtensionAngle = 0
  FormatSpec = %.2w
  FormatSpecOverTolerance = %+.2w
  FormatSpecUnderTolerance = %+.2w
  Inverted = false
  LineAngle = 0
  LockPosition = false
  MeasureType = 1
  OverTolerance = 0
  References2D = -> [ProjItem002]
  Rotation = 0
  ScaleType = 0
  TheoreticalExact = false
  Type = 1
  UnderTolerance = 0
  X = 52.1421
  Y = 23.3431
FEATURE [TechDraw::DrawSVGTemplate] Template001
  EditableTexts = Designed_by_Name=Thomas Spielauer; FC-Date=2023-11-08; FC-SC=mm; FC-SH=2/2; FC-Title=120mm to CF63 adapter; Subtitle=XL30 ESEM compatible
  Height = 210
  Orientation = 1
  Template = <path>
  Width = 297
FEATURE [TechDraw::DrawViewPart] View
  CoarseView = false
  Direction = (0,0,1)
  Focus = 100
  HardHidden = false
  IsoCount = 0
  IsoHidden = false
  IsoVisible = false
  LockPosition = false
  Perspective = false
  Rotation = 90
  Scale = 0.5
  ScaleType = 2
  ScrubCount = 0
  SeamHidden = false
  SeamVisible = false
  SmoothHidden = false
  SmoothVisible = true
  Source = -> [Cut001]
  X = 66.9566
  XDirection = (0,1,0)
  Y = 53.8152
FEATURE [TechDraw::DrawViewSection] SectionView  label="Section  - "
  BaseView = -> View
  CoarseView = false
  CutSurfaceDisplay = 2
  Direction = (1e-16,-1,0)
  FileGeomPattern = <path>
  FileHatchPattern = <path>
  Focus = 100
  FuseBeforeCut = false
  HardHidden = false
  HatchOffset = (0,0,0)
  HatchRotation = 0
  HatchScale = 1
  IsoCount = 0
  IsoHidden = false
  IsoVisible = false
  LockPosition = false
  NameGeomPattern = Diamant
  Perspective = false
  Rotation = 0
  Scale = 1.8
  ScaleType = 2
  ScrubCount = 0
  SeamHidden = false
  SeamVisible = false
  SectionDirection = 4
  SectionNormal = (1e-16,-1,0)
  SectionOrigin = (0,0,14.25)
  SmoothHidden = false
  SmoothVisible = true
  Source = -> [Cut001]
  TrimAfterCut = false
  X = 151.069
  XDirection = (1,1e-16,0)
  Y = 145.819
FEATURE [TechDraw::DrawViewDimension] Dimension021
  AngleOverride = false
  Arbitrary = false
  ArbitraryTolerances = false
  EqualTolerance = true
  ExtensionAngle = 0
  FormatSpec = %.2w
  FormatSpecOverTolerance = %+.2w
  FormatSpecUnderTolerance = %+.2w
  Inverted = false
  LineAngle = 0
  LockPosition = false
  MeasureType = 1
  OverTolerance = 0
  References2D = -> [SectionView]
  Rotation = 0
  ScaleType = 0
  TheoreticalExact = false
  Type = 2
  UnderTolerance = 0
  X = -125.279
  Y = -30.3858
FEATURE [TechDraw::DrawViewDimension] Dimension022
  AngleOverride = false
  Arbitrary = false
  ArbitraryTolerances = false
  EqualTolerance = true
  ExtensionAngle = 0
  FormatSpec = %.2w
  FormatSpecOverTolerance = %+.2w
  FormatSpecUnderTolerance = %+.2w
  Inverted = false
  LineAngle = 0
  LockPosition = false
  MeasureType = 1
  OverTolerance = 0
  References2D = -> [SectionView]
  Rotation = 0
  ScaleType = 0
  TheoreticalExact = false
  Type = 1
  UnderTolerance = 0
  X = -77.5041
  Y = -37.296
FEATURE [TechDraw::DrawViewDimension] Dimension023
  AngleOverride = false
  Arbitrary = false
  ArbitraryTolerances = false
  EqualTolerance = true
  ExtensionAngle = 0
  FormatSpec = %.2w
  FormatSpecOverTolerance = %+.2w
  FormatSpecUnderTolerance = %+.2w
  Inverted = false
  LineAngle = 0
  LockPosition = false
  MeasureType = 1
  OverTolerance = 0
  References2D = -> [SectionView]
  Rotation = 0
  ScaleType = 0
  TheoreticalExact = false
  Type = 1
  UnderTolerance = 0
  X = -2.28943
  Y = 2.72866
FEATURE [TechDraw::DrawViewDimension] Dimension024
  AngleOverride = false
  Arbitrary = false
  ArbitraryTolerances = false
  EqualTolerance = true
  ExtensionAngle = 0
  FormatSpec = %.2w
  FormatSpecOverTolerance = %+.2w
  FormatSpecUnderTolerance = %+.2w
  Inverted = false
  LineAngle = 0
  LockPosition = false
  MeasureType = 1
  OverTolerance = 0
  References2D = -> [SectionView]
  Rotation = 0
  ScaleType = 0
  TheoreticalExact = false
  Type = 2
  UnderTolerance = 0
  X = 118.505
  Y = -8.38277
FEATURE [TechDraw::DrawViewDimension] Dimension025
  AngleOverride = false
  Arbitrary = false
  ArbitraryTolerances = false
  EqualTolerance = true
  ExtensionAngle = 0
  FormatSpec = %.2w
  FormatSpecOverTolerance = %+.2w
  FormatSpecUnderTolerance = %+.2w
  Inverted = false
  LineAngle = 0
  LockPosition = false
  MeasureType = 1
  OverTolerance = 0
  References2D = -> [SectionView]
  Rotation = 0
  ScaleType = 0
  TheoreticalExact = false
  Type = 1
  UnderTolerance = 0
  X = 122.168
  Y = -36.6638
FEATURE [TechDraw::DrawViewDimension] Dimension026
  AngleOverride = false
  Arbitrary = false
  ArbitraryTolerances = false
  EqualTolerance = true
  ExtensionAngle = 0
  FormatSpec = %.2w
  FormatSpecOverTolerance = %+.2w
  FormatSpecUnderTolerance = %+.2w
  Inverted = false
  LineAngle = 0
  LockPosition = false
  MeasureType = 1
  OverTolerance = 0
  References2D = -> [SectionView]
  Rotation = 0
  ScaleType = 0
  TheoreticalExact = false
  Type = 1
  UnderTolerance = 0
  X = 72.6138
  Y = -29.6388
FEATURE [TechDraw::DrawViewDimension] Dimension027
  AngleOverride = false
  Arbitrary = false
  ArbitraryTolerances = false
  EqualTolerance = true
  ExtensionAngle = 0
  FormatSpec = %.2w
  FormatSpecOverTolerance = %+.2w
  FormatSpecUnderTolerance = %+.2w
  Inverted = false
  LineAngle = 0
  LockPosition = false
  MeasureType = 1
  OverTolerance = 0
  References2D = -> [SectionView]
  Rotation = 0
  ScaleType = 0
  TheoreticalExact = false
  Type = 2
  UnderTolerance = 0
  X = -128.741
  Y = 38.2747
FEATURE [TechDraw::DrawViewDimension] Dimension028
  AngleOverride = false
  Arbitrary = false
  ArbitraryTolerances = false
  EqualTolerance = true
  ExtensionAngle = 0
  FormatSpec = %.2w
  FormatSpecOverTolerance = %+.2w
  FormatSpecUnderTolerance = %+.2w
  Inverted = false
  LineAngle = 0
  LockPosition = false
  MeasureType = 1
  OverTolerance = 0
  References2D = -> [SectionView]
  Rotation = 0
  ScaleType = 0
  TheoreticalExact = false
  Type = 2
  UnderTolerance = 0
  X = 0
  Y = 2.5
FEATURE [TechDraw::DrawViewDimension] Dimension029
  AngleOverride = false
  Arbitrary = false
  ArbitraryTolerances = false
  EqualTolerance = true
  ExtensionAngle = 0
  FormatSpec = %.2w
  FormatSpecOverTolerance = %+.2w
  FormatSpecUnderTolerance = %+.2w
  Inverted = false
  LineAngle = 0
  LockPosition = false
  MeasureType = 1
  OverTolerance = 0
  References2D = -> [SectionView]
  Rotation = 0
  ScaleType = 0
  TheoreticalExact = false
  Type = 2
  UnderTolerance = 0
  X = -120.766
  Y = 38.8741
FEATURE [TechDraw::DrawViewDimension] Dimension030
  AngleOverride = false
  Arbitrary = false
  ArbitraryTolerances = false
  EqualTolerance = true
  ExtensionAngle = 0
  FormatSpec = %.2w
  FormatSpecOverTolerance = %+.2w
  FormatSpecUnderTolerance = %+.2w
  Inverted = false
  LineAngle = 0
  LockPosition = false
  MeasureType = 1
  OverTolerance = 0
  References2D = -> [SectionView]
  Rotation = 0
  ScaleType = 0
  TheoreticalExact = false
  Type = 2
  UnderTolerance = 0
  X = -112.47
  Y = 38.1217
FEATURE [TechDraw::DrawViewDimension] Dimension031
  AngleOverride = false
  Arbitrary = false
  ArbitraryTolerances = false
  EqualTolerance = true
  ExtensionAngle = 0
  FormatSpec = %.2w (1mm deep leak checking groove)
  FormatSpecOverTolerance = %+.2w
  FormatSpecUnderTolerance = %+.2w
  Inverted = false
  LineAngle = 0
  LockPosition = false
  MeasureType = 1
  OverTolerance = 0
  References2D = -> [View]
  Rotation = 0
  ScaleType = 0
  TheoreticalExact = false
  Type = 0
  UnderTolerance = 0
  X = 63.3767
  Y = 6.5867
FEATURE [TechDraw::DrawPage] Page001
  KeepUpdated = true
  NextBalloonIndex = 1
  ProjectionType = 0
  Template = -> Template001
  Views = -> [View,SectionView,Dimension021,Dimension022,Dimension023,Dimension024,Dimension025,Dimension026,Dimension027,Dimension028,Dimension029,Dimension030,Dimension031]
FEATURE [TechDraw::DrawViewDimension] Dimension032
  AngleOverride = false
  Arbitrary = false
  ArbitraryTolerances = false
  EqualTolerance = true
  ExtensionAngle = 0
  FormatSpec = ⌀%.2w
  FormatSpecOverTolerance = %+.2w
  FormatSpecUnderTolerance = %+.2w
  Inverted = false
  LineAngle = 0
  LockPosition = false
  MeasureType = 1
  OverTolerance = 0
  References2D = -> [ProjItem001]
  Rotation = 0
  ScaleType = 0
  TheoreticalExact = false
  Type = 5
  UnderTolerance = 0
  X = 37.5059
  Y = -33.9713
FEATURE [TechDraw::DrawPage] Page
  KeepUpdated = true
  NextBalloonIndex = 1
  ProjectionType = 0
  Template = -> Template
  Views = -> [ProjGroup,Dimension,Dimension001,Dimension002,Dimension003,Dimension004,Dimension005,Dimension006,Dimension007,Dimension008,Dimension010,Dimension011,Dimension012,Dimension013,Dimension014,Dimension015,Dimension016,Dimension017,Dimension018,Dimension019,Dimension020,Dimension032]
note: 4 file-system paths scrubbed to <path> (originals preserved in the JSON sidecar)
---- part PhilipsXL30_AligningRing.FCStd = doc fcstd_97deb94a6a46 ----
FCSTD DOCUMENT  (FreeCAD 0.22R0.21.2)
Label: PhilipsXL30_AligningRing
License: All rights reserved
LicenseURL: http://en.wikipedia.org/wiki/All_rights_reserved
objects: TechDraw::DrawViewDimension×43, Part::Cylinder×18, Part::MultiFuse×9, TechDraw::DrawProjGroupItem×8, Part::Cut×7, Part::Box×5, Part::FeaturePython×3, TechDraw::DrawSVGTemplate×3, TechDraw::DrawViewSection×3, TechDraw::DrawPage×3, Part::Feature×2, TechDraw::DrawProjGroup×2, TechDraw::DrawViewPart×2, Part::Cone×1
note: 107 computed .brp shape members not serialized (recipe doc carries the construction recipe); baked Part::Feature solids carry a one-line shape summary decoded from their .brp

FEATURE [Part::Cone] Cone001
  Angle = 360
  AttacherType = Attacher::AttachEngine3D
  Height = 20
  Placement = pos=(0,0,-5) rot=(0,0,1;0rad)
  Radius1 = 6.5
  Radius2 = 26.5
FEATURE [Part::Cylinder] Cylinder
  Angle = 360
  AttacherType = Attacher::AttachEngine3D
  FirstAngle = 0
  Height = 5
  Radius = 24
  SecondAngle = 0
FEATURE [Part::Cut] Cut
  Base = -> Cylinder
  Tool = -> Cone001
FEATURE [Part::Box] Box  label="Cube"
  AttacherType = Attacher::AttachEngine3D
  Height = 25
  Length = 5
  Placement = pos=(3.5,-22,-25) rot=(0,0,1;0rad)
  Width = 44
FEATURE [Part::Cylinder] Cylinder001
  Angle = 360
  AttacherType = Attacher::AttachEngine3D
  FirstAngle = 0
  Height = 10
  Radius = 1.2
  SecondAngle = 0
FEATURE [Part::Cylinder] Cylinder002
  Angle = 360
  AttacherType = Attacher::AttachEngine3D
  FirstAngle = 0
  Height = 10
  Placement = pos=(12.6,0,0) rot=(0,0,1;0rad)
  Radius = 1.2
  SecondAngle = 0
FEATURE [Part::Box] Box001  label="Cube001"
  AttacherType = Attacher::AttachEngine3D
  Height = 10
  Length = 12.5
  Placement = pos=(0,-1.2,0) rot=(0,0,1;0rad)
  Width = 2.4
FEATURE [Part::MultiFuse] Fusion  label="Langloch"
  Placement = pos=(0,5.75,-7.7) rot=(0,1,0;1.5708rad)
  Shapes = -> [Box001,Cylinder001,Cylinder002]
FEATURE [Part::Box] Box002  label="Cube002"
  AttacherType = Attacher::AttachEngine3D
  Height = 10
  Length = 12.5
  Placement = pos=(0,-1.2,0) rot=(0,0,1;0rad)
  Width = 2.4
FEATURE [Part::Cylinder] Cylinder003
  Angle = 360
  AttacherType = Attacher::AttachEngine3D
  FirstAngle = 0
  Height = 10
  Radius = 1.2
  SecondAngle = 0
FEATURE [Part::Cylinder] Cylinder004
  Angle = 360
  AttacherType = Attacher::AttachEngine3D
  FirstAngle = 0
  Height = 10
  Placement = pos=(12.6,0,0) rot=(0,0,1;0rad)
  Radius = 1.2
  SecondAngle = 0
FEATURE [Part::MultiFuse] Fusion001  label="Langloch001"
  Placement = pos=(0,-5.75,-7.7) rot=(0,1,0;1.5708rad)
  Shapes = -> [Box002,Cylinder003,Cylinder004]
FEATURE [Part::MultiFuse] Fusion002
  Shapes = -> [Fusion001,Fusion]
FEATURE [Part::Cut] Cut001
  Base = -> Box
  Tool = -> Fusion002
FEATURE [Part::Cylinder] Cylinder005
  Angle = 360
  AttacherType = Attacher::AttachEngine3D
  FirstAngle = 0
  Height = 17
  Placement = pos=(0,0,-6) rot=(0,0,1;0rad)
  Radius = 12
  SecondAngle = 0
FEATURE [Part::Cut] Cut002
  Base = -> Cut001
  Tool = -> Cylinder005
FEATURE [Part::FeaturePython] Screw  label="M3x8-Screw"  # Fasteners workbench fastener (typed FeaturePython)
  Placement = pos=(6,19,3) rot=(0,0,1;0rad)
  diameter = 4
  invert = false
  leftHanded = false
  length = 2
  lengthCustom = 8
  matchOuter = false
  offset = 0
  thread = false
  type = 48
FEATURE [Part::FeaturePython] Screw001  label="M3x8-Screw001"  # Fasteners workbench fastener (typed FeaturePython)
  Placement = pos=(6,-19,3) rot=(0,0,1;0rad)
  diameter = 4
  invert = false
  leftHanded = false
  length = 2
  lengthCustom = 8
  matchOuter = false
  offset = 0
  thread = false
  type = 48
FEATURE [Part::Cylinder] Cylinder006
  Angle = 360
  AttacherType = Attacher::AttachEngine3D
  FirstAngle = 0
  Height = 10
  Placement = pos=(6,19,-8) rot=(0,0,1;0rad)
  Radius = 1.195
  SecondAngle = 0
FEATURE [Part::Cylinder] Cylinder007
  Angle = 360
  AttacherType = Attacher::AttachEngine3D
  FirstAngle = 0
  Height = 10
  Placement = pos=(6,-19,-8) rot=(0,0,1;0rad)
  Radius = 1.195
  SecondAngle = 0
FEATURE [Part::MultiFuse] Fusion003
  Shapes = -> [Cylinder006,Cylinder007]
FEATURE [Part::Cut] Cut003  label="Kickeraligner_01"
  Base = -> Cut002
  Tool = -> Fusion003
FEATURE [Part::Cylinder] Cylinder008
  Angle = 360
  AttacherType = Attacher::AttachEngine3D
  FirstAngle = 0
  Height = 10
  Placement = pos=(6,19,0) rot=(0,0,1;0rad)
  Radius = 1.7
  SecondAngle = 0
FEATURE [Part::Cylinder] Cylinder009
  Angle = 360
  AttacherType = Attacher::AttachEngine3D
  FirstAngle = 0
  Height = 10
  Placement = pos=(6,-19,0) rot=(0,0,1;0rad)
  Radius = 1.7
  SecondAngle = 0
FEATURE [Part::Cylinder] Cylinder010
  Angle = 360
  AttacherType = Attacher::AttachEngine3D
  FirstAngle = 0
  Height = 2
  Placement = pos=(6,19,3) rot=(0,0,1;0rad)
  Radius = 2.8
  SecondAngle = 0
FEATURE [Part::Cylinder] Cylinder011
  Angle = 360
  AttacherType = Attacher::AttachEngine3D
  FirstAngle = 0
  Height = 2
  Placement = pos=(6,-19,3) rot=(0,0,1;0rad)
  Radius = 2.8
  SecondAngle = 0
FEATURE [Part::MultiFuse] Fusion004
  Shapes = -> [Cylinder008,Cylinder009,Cylinder010,Cylinder011]
FEATURE [Part::Cut] Cut004
  Base = -> Cut
  Tool = -> Fusion004
FEATURE [Part::Cylinder] Cylinder012
  Angle = 360
  AttacherType = Attacher::AttachEngine3D
  FirstAngle = 0
  Height = 2
  Placement = pos=(0,0,3) rot=(0,0,1;0rad)
  Radius = 2.8
  SecondAngle = 0
FEATURE [Part::Cylinder] Cylinder013
  Angle = 360
  AttacherType = Attacher::AttachEngine3D
  FirstAngle = 0
  Height = 10
  Radius = 1.7
  SecondAngle = 0
FEATURE [Part::MultiFuse] Fusion005
  Shapes = -> [Cylinder013,Cylinder012]
FEATURE [Part::FeaturePython] Array  # Draft array (typed FeaturePython)
  AlwaysSyncPlacement = false
  Angle = 360
  ArrayType = 2
  Axis = (0,0,1)
  Base = -> Fusion005
  Center = (0,0,0)
  Count = 9
  ExpandArray = false
  Fuse = false
  IntervalAxis = (0,0,0)
  IntervalX = (100,0,0)
  IntervalY = (0,100,0)
  IntervalZ = (0,0,100)
  NumberCircles = 2
  NumberPolar = 5
  NumberX = 2
  NumberY = 2
  NumberZ = 1
  PlacementList = 9 placements: [(0,0,0),(-20,0,0),(-14.1421,-14.1421,0),(-4.44089e-15,-20,0),(14.1421,-14.1421,0),(20,-2.44929e-15,0),(14.1421,14.1421,0),(4.44089e-15,20,0),(-14.1421,14.1421,0)]
  RadialDistance = 20
  ScaleList = (9) [(1,1,1),(1,1,1),(1,1,1),(1,1,1),(1,1,1),(1,1,1),(1,1,1),(1,1,1),(1,1,1)]
  Symmetry = 1
  TangentialDistance = 15
FEATURE [Part::Cut] Cut005  label="AligningRing"
  Base = -> Cut004
  Tool = -> Array
FEATURE [Part::Feature] Cut005_solid  label="AligningRing (Solid)"
  shape: bbox 48 x 48 x 5 mm, 34 faces (baked)
FEATURE [TechDraw::DrawSVGTemplate] Template
  EditableTexts = Designed_by_Name=Thomas Spielauer; FC-Date=2024-06-04; FC-SC=mm; FC-Title=XL30 Column Alignment Ring; Subtitle=Subtitle
  Height = 210
  Orientation = 1
  Template = <path>
  Width = 297
FEATURE [TechDraw::DrawProjGroupItem] ProjItem  label="Front"
  CoarseView = false
  Direction = (0,0,1)
  Focus = 100
  HardHidden = false
  IsoCount = 0
  IsoHidden = false
  IsoVisible = false
  LockPosition = true
  Perspective = false
  Rotation = 0
  RotationVector = (0,1,0)
  Scale = 2
  ScaleType = 2
  ScrubCount = 0
  SeamHidden = false
  SeamVisible = false
  SmoothHidden = false
  SmoothVisible = true
  Source = -> [Cut005]
  Type = 0
  X = 0
  XDirection = (0,1,0)
  Y = 0
FEATURE [TechDraw::DrawProjGroupItem] ProjItem001  label="Rear"
  CoarseView = false
  Direction = (0,0,-1)
  Focus = 100
  HardHidden = false
  IsoCount = 0
  IsoHidden = false
  IsoVisible = false
  LockPosition = false
  Perspective = false
  Rotation = 0
  RotationVector = (1,0,0)
  Scale = 2
  ScaleType = 2
  ScrubCount = 0
  SeamHidden = false
  SeamVisible = false
  SmoothHidden = false
  SmoothVisible = true
  Source = -> [Cut005]
  Type = 3
  X = 136
  XDirection = (0,-1,0)
  Y = 0
FEATURE [TechDraw::DrawProjGroupItem] ProjItem002  label="Left"
  CoarseView = false
  Direction = (0,-1,1e-16)
  Focus = 100
  HardHidden = false
  IsoCount = 0
  IsoHidden = false
  IsoVisible = false
  LockPosition = false
  Perspective = false
  Rotation = 0
  RotationVector = (1,0,0)
  Scale = 2
  ScaleType = 2
  ScrubCount = 0
  SeamHidden = false
  SeamVisible = false
  SmoothHidden = false
  SmoothVisible = true
  Source = -> [Cut005]
  Type = 1
  X = 68
  XDirection = (0,1e-16,1)
  Y = 0
FEATURE [TechDraw::DrawProjGroup] ProjGroup
  Anchor = -> ProjItem
  AutoDistribute = true
  LockPosition = false
  ProjectionType = 0
  Rotation = 0
  Scale = 2
  ScaleType = 1
  Source = -> [Cut005]
  Views = -> [ProjItem,ProjItem001,ProjItem002]
  X = 75.1959
  Y = 130.904
  spacingX = 15
  spacingY = 15
FEATURE [TechDraw::DrawViewDimension] Dimension
  AngleOverride = false
  Arbitrary = false
  ArbitraryTolerances = false
  EqualTolerance = true
  ExtensionAngle = 0
  FormatSpec = %.2w
  FormatSpecOverTolerance = %+.2w
  FormatSpecUnderTolerance = %+.2w
  Inverted = false
  LineAngle = 0
  LockPosition = false
  MeasureType = 1
  OverTolerance = 0
  References2D = -> [ProjItem002]
  Rotation = 0
  ScaleType = 0
  TheoreticalExact = false
  Type = 1
  UnderTolerance = 0
  X = 14.6766
  Y = 64.1241
FEATURE [TechDraw::DrawViewDimension] Dimension001
  AngleOverride = false
  Arbitrary = false
  ArbitraryTolerances = false
  EqualTolerance = true
  ExtensionAngle = 0
  FormatSpec = ⌀%.2w
  FormatSpecOverTolerance = %+.2w
  FormatSpecUnderTolerance = %+.2w
  Inverted = false
  LineAngle = 0
  LockPosition = false
  MeasureType = 1
  OverTolerance = 0
  References2D = -> [ProjItem001]
  Rotation = 0
  ScaleType = 0
  TheoreticalExact = false
  Type = 5
  UnderTolerance = 0
  X = 14.4966
  Y = 59.5959
FEATURE [TechDraw::DrawViewDimension] Dimension002
  AngleOverride = false
  Arbitrary = false
  ArbitraryTolerances = false
  EqualTolerance = true
  ExtensionAngle = 0
  FormatSpec = ⌀%.2w
  FormatSpecOverTolerance = %+.2w
  FormatSpecUnderTolerance = %+.2w
  Inverted = false
  LineAngle = 0
  LockPosition = false
  MeasureType = 1
  OverTolerance = 0
  References2D = -> [ProjItem001]
  Rotation = 0
  ScaleType = 0
  TheoreticalExact = false
  Type = 5
  UnderTolerance = 0
  X = 30.1939
  Y = 53.0714
FEATURE [TechDraw::DrawViewDimension] Dimension003
  AngleOverride = false
  Arbitrary = false
  ArbitraryTolerances = false
  EqualTolerance = true
  ExtensionAngle = 0
  FormatSpec = ⌀%.2w (10x)
  FormatSpecOverTolerance = %+.2w
  FormatSpecUnderTolerance = %+.2w
  Inverted = false
  LineAngle = 0
  LockPosition = false
  MeasureType = 1
  OverTolerance = 0
  References2D = -> [ProjItem001]
  Rotation = 0
  ScaleType = 0
  TheoreticalExact = false
  Type = 5
  UnderTolerance = 0
  X = 49.7609
  Y = 51.7571
FEATURE [TechDraw::DrawViewDimension] Dimension004
  AngleOverride = false
  Arbitrary = false
  ArbitraryTolerances = false
  EqualTolerance = true
  ExtensionAngle = 0
  FormatSpec = ⌀%.2w
  FormatSpecOverTolerance = %+.2w
  FormatSpecUnderTolerance = %+.2w
  Inverted = false
  LineAngle = 0
  LockPosition = false
  MeasureType = 1
  OverTolerance = 0
  References2D = -> [ProjItem]
  Rotation = 0
  ScaleType = 0
  TheoreticalExact = false
  Type = 5
  UnderTolerance = 0
  X = 33.9204
  Y = 57.7895
FEATURE [TechDraw::DrawViewDimension] Dimension005
  AngleOverride = false
  Arbitrary = false
  ArbitraryTolerances = false
  EqualTolerance = true
  ExtensionAngle = 0
  FormatSpec = ⌀%.2w
  FormatSpecOverTolerance = %+.2w
  FormatSpecUnderTolerance = %+.2w
  Inverted = false
  LineAngle = 0
  LockPosition = false
  MeasureType = 1
  OverTolerance = 0
  References2D = -> [ProjItem]
  Rotation = 0
  ScaleType = 0
  TheoreticalExact = false
  Type = 5
  UnderTolerance = 0
  X = 26.899
  Y = 61.6719
FEATURE [TechDraw::DrawViewDimension] Dimension006
  AngleOverride = false
  Arbitrary = false
  ArbitraryTolerances = false
  EqualTolerance = true
  ExtensionAngle = 0
  FormatSpec = ⌀%.2w
  FormatSpecOverTolerance = %+.2w
  FormatSpecUnderTolerance = %+.2w
  Inverted = false
  LineAngle = 0
  LockPosition = false
  MeasureType = 1
  OverTolerance = 0
  References2D = -> [ProjItem]
  Rotation = 0
  ScaleType = 0
  TheoreticalExact = false
  Type = 5
  UnderTolerance = 0
  X = 17.5465
  Y = 63.697
FEATURE [TechDraw::DrawViewDimension] Dimension007
  AngleOverride = false
  Arbitrary = false
  ArbitraryTolerances = false
  EqualTolerance = true
  ExtensionAngle = 0
  FormatSpec = ⌀%.2w (10x)
  FormatSpecOverTolerance = %+.2w
  FormatSpecUnderTolerance = %+.2w
  Inverted = false
  LineAngle = 0
  LockPosition = false
  MeasureType = 1
  OverTolerance = 0
  References2D = -> [ProjItem]
  Rotation = 0
  ScaleType = 0
  TheoreticalExact = false
  Type = 5
  UnderTolerance = 0
  X = 45.3319
  Y = 51.7849
FEATURE [TechDraw::DrawViewDimension] Dimension008
  AngleOverride = false
  Arbitrary = false
  ArbitraryTolerances = false
  EqualTolerance = true
  ExtensionAngle = 0
  FormatSpec = ⌀%.2w
  FormatSpecOverTolerance = %+.2w
  FormatSpecUnderTolerance = %+.2w
  Inverted = false
  LineAngle = 0
  LockPosition = false
  MeasureType = 1
  OverTolerance = 0
  References2D = -> [ProjItem]
  Rotation = 0
  ScaleType = 0
  TheoreticalExact = false
  Type = 5
  UnderTolerance = 0
  X = -16.0753
  Y = 61.592
FEATURE [TechDraw::DrawViewDimension] Dimension009
  AngleOverride = false
  Arbitrary = false
  ArbitraryTolerances = false
  EqualTolerance = true
  ExtensionAngle = 0
  FormatSpec = %.2w (8x)
  FormatSpecOverTolerance = %+.2w
  FormatSpecUnderTolerance = %+.2w
  Inverted = false
  LineAngle = 0
  LockPosition = false
  MeasureType = 1
  OverTolerance = 0
  References2D = -> [ProjItem]
  Rotation = 0
  ScaleType = 0
  TheoreticalExact = false
  Type = 6
  UnderTolerance = 0
  X = -52.7672
  Y = 29.4701
FEATURE [TechDraw::DrawViewDimension] Dimension010
  AngleOverride = false
  Arbitrary = false
  ArbitraryTolerances = false
  EqualTolerance = true
  ExtensionAngle = 0
  FormatSpec = %.2w (2x)
  FormatSpecOverTolerance = %+.2w
  FormatSpecUnderTolerance = %+.2w
  Inverted = false
  LineAngle = 0
  LockPosition = false
  MeasureType = 1
  OverTolerance = 0
  References2D = -> [ProjItem]
  Rotation = 0
  ScaleType = 0
  TheoreticalExact = false
  Type = 6
  UnderTolerance = 0
  X = -41.0402
  Y = -30.1439
FEATURE [TechDraw::DrawViewSection] SectionView  label="Section  - "
  BaseView = -> ProjItem
  CoarseView = false
  CutSurfaceDisplay = 2
  Direction = (1e-16,-1,0)
  FileGeomPattern = <path>
  FileHatchPattern = <path>
  Focus = 100
  FuseBeforeCut = false
  HardHidden = false
  HatchOffset = (0,0,0)
  HatchRotation = 0
  HatchScale = 1
  IsoCount = 0
  IsoHidden = false
  IsoVisible = false
  LockPosition = false
  NameGeomPattern = Diamond
  Perspective = false
  Rotation = 0
  Scale = 2
  ScaleType = 2
  ScrubCount = 0
  SeamHidden = false
  SeamVisible = false
  SectionDirection = 4
  SectionLineStretch = 1
  SectionNormal = (1e-16,-1,0)
  SectionOrigin = (0,0,2.5)
  SmoothHidden = false
  SmoothVisible = true
  Source = -> [Cut005]
  TrimAfterCut = false
  UsePreviousCut = false
  X = 78.0601
  XDirection = (1,1e-16,0)
  Y = 34.3268
FEATURE [TechDraw::DrawViewDimension] Dimension011
  AngleOverride = false
  Arbitrary = false
  ArbitraryTolerances = false
  EqualTolerance = true
  ExtensionAngle = 0
  FormatSpec = %.2w
  FormatSpecOverTolerance = %+.2w
  FormatSpecUnderTolerance = %+.2w
  Inverted = false
  LineAngle = 0
  LockPosition = false
  MeasureType = 1
  OverTolerance = 0
  References2D = -> [SectionView]
  Rotation = 0
  ScaleType = 0
  TheoreticalExact = false
  Type = 2
  UnderTolerance = 0
  X = -56.9152
  Y = 17.9756
FEATURE [TechDraw::DrawViewDimension] Dimension012
  AngleOverride = false
  Arbitrary = false
  ArbitraryTolerances = false
  EqualTolerance = true
  ExtensionAngle = 0
  FormatSpec = %.2w
  FormatSpecOverTolerance = %+.2w
  FormatSpecUnderTolerance = %+.2w
  Inverted = false
  LineAngle = 0
  LockPosition = false
  MeasureType = 1
  OverTolerance = 0
  References2D = -> [SectionView]
  Rotation = 0
  ScaleType = 0
  TheoreticalExact = false
  Type = 2
  UnderTolerance = 0
  X = 51.4914
  Y = 16.9401
FEATURE [TechDraw::DrawViewDimension] Dimension013
  AngleOverride = false
  Arbitrary = false
  ArbitraryTolerances = false
  EqualTolerance = true
  ExtensionAngle = 0
  FormatSpec = %.2w
  FormatSpecOverTolerance = %+.2w
  FormatSpecUnderTolerance = %+.2w
  Inverted = false
  LineAngle = 0
  LockPosition = false
  MeasureType = 1
  OverTolerance = 0
  References2D = -> [SectionView]
  Rotation = 0
  ScaleType = 0
  TheoreticalExact = false
  Type = 1
  UnderTolerance = 0
  X = -1.79985
  Y = 16.369
FEATURE [TechDraw::DrawViewDimension] Dimension014
  AngleOverride = false
  Arbitrary = false
  ArbitraryTolerances = false
  EqualTolerance = true
  ExtensionAngle = 0
  FormatSpec = %.2w
  FormatSpecOverTolerance = %+.2w
  FormatSpecUnderTolerance = %+.2w
  Inverted = false
  LineAngle = 0
  LockPosition = false
  MeasureType = 1
  OverTolerance = 0
  References2D = -> [SectionView]
  Rotation = 0
  ScaleType = 0
  TheoreticalExact = false
  Type = 1
  UnderTolerance = 0
  X = -1.61231
  Y = -11.4713
FEATURE [TechDraw::DrawViewDimension] Dimension016
  AngleOverride = false
  Arbitrary = false
  ArbitraryTolerances = false
  EqualTolerance = true
  ExtensionAngle = 0
  FormatSpec = %.2w
  FormatSpecOverTolerance = %+.2w
  FormatSpecUnderTolerance = %+.2w
  Inverted = false
  LineAngle = 0
  LockPosition = false
  MeasureType = 1
  OverTolerance = 0
  References2D = -> [SectionView]
  Rotation = 0
  ScaleType = 0
  TheoreticalExact = false
  Type = 1
  UnderTolerance = 0
  X = -50.6255
  Y = -9.92308
FEATURE [TechDraw::DrawViewDimension] Dimension017
  AngleOverride = false
  Arbitrary = false
  ArbitraryTolerances = false
  EqualTolerance = true
  ExtensionAngle = 0
  FormatSpec = %.2w
  FormatSpecOverTolerance = %+.2w
  FormatSpecUnderTolerance = %+.2w
  Inverted = false
  LineAngle = 0
  LockPosition = false
  MeasureType = 1
  OverTolerance = 0
  References2D = -> [SectionView]
  Rotation = 0
  ScaleType = 0
  TheoreticalExact = false
  Type = 1
  UnderTolerance = 0
  X = -39.3802
  Y = 21.6146
FEATURE [TechDraw::DrawViewDimension] Dimension018
  AngleOverride = false
  Arbitrary = false
  ArbitraryTolerances = false
  EqualTolerance = true
  ExtensionAngle = 0
  FormatSpec = %.2w
  FormatSpecOverTolerance = %+.2w
  FormatSpecUnderTolerance = %+.2w
  Inverted = false
  LineAngle = 0
  LockPosition = false
  MeasureType = 1
  OverTolerance = 0
  References2D = -> [SectionView]
  Rotation = 0
  ScaleType = 0
  TheoreticalExact = false
  Type = 6
  UnderTolerance = 0
  X = 23.2977
  Y = -7.15191
FEATURE [TechDraw::DrawPage] Page
  KeepUpdated = true
  NextBalloonIndex = 1
  ProjectionType = 0
  Template = -> Template
  Views = -> [ProjGroup,Dimension,Dimension001,Dimension002,Dimension003,Dimension004,Dimension005,Dimension006,Dimension007,Dimension008,Dimension009,Dimension010,SectionView,Dimension011,Dimension012,Dimension013,Dimension014,Dimension016,Dimension017,Dimension018]
FEATURE [TechDraw::DrawSVGTemplate] Template001
  EditableTexts = Designed_by_Name=Thomas Spielauer; FC-Date=2024-06-04; FC-SC=mm; FC-Title=XL30 Kicker v3 Aligner; Subtitle=for Column aligning ring
  Height = 210
  Orientation = 1
  Template = <path>
  Width = 297
FEATURE [Part::Box] Box003  label="Cube003"
  AttacherType = Attacher::AttachEngine3D
  Height = 1.6
  Length = 12.5
  Placement = pos=(0,-2,0) rot=(0,0,1;0rad)
  Width = 4
FEATURE [Part::Cylinder] Cylinder014
  Angle = 360
  AttacherType = Attacher::AttachEngine3D
  FirstAngle = 0
  Height = 1.6
  Radius = 2
  SecondAngle = 0
FEATURE [Part::Cylinder] Cylinder015
  Angle = 360
  AttacherType = Attacher::AttachEngine3D
  FirstAngle = 0
  Height = 1.6
  Placement = pos=(12.6,0,0) rot=(0,0,1;0rad)
  Radius = 2
  SecondAngle = 0
FEATURE [Part::MultiFuse] Fusion006  label="Langloch002"
  Placement = pos=(7,-5.75,-7.7) rot=(0,1,0;1.5708rad)
  Shapes = -> [Box003,Cylinder014,Cylinder015]
FEATURE [Part::Box] Box004  label="Cube004"
  AttacherType = Attacher::AttachEngine3D
  Height = 1.6
  Length = 12.5
  Placement = pos=(0,-2,0) rot=(0,0,1;0rad)
  Width = 4
FEATURE [Part::Cylinder] Cylinder016
  Angle = 360
  AttacherType = Attacher::AttachEngine3D
  FirstAngle = 0
  Height = 1.6
  Radius = 2
  SecondAngle = 0
FEATURE [Part::Cylinder] Cylinder017
  Angle = 360
  AttacherType = Attacher::AttachEngine3D
  FirstAngle = 0
  Height = 1.6
  Placement = pos=(12.6,0,0) rot=(0,0,1;0rad)
  Radius = 2
  SecondAngle = 0
FEATURE [Part::MultiFuse] Fusion007  label="Langloch003"
  Placement = pos=(7,5.75,-7.7) rot=(0,1,0;1.5708rad)
  Shapes = -> [Box004,Cylinder016,Cylinder017]
FEATURE [Part::MultiFuse] Fusion008
  Shapes = -> [Fusion007,Fusion006]
FEATURE [Part::Cut] Cut006  label="Kickeraligner"
  Base = -> Cut003
  Tool = -> Fusion008
FEATURE [Part::Feature] Cut006_solid  label="Kickeraligner (Solid)"
  shape: bbox 5 x 44 x 25 mm, 60 faces (baked)
FEATURE [TechDraw::DrawProjGroupItem] ProjItem003  label="Front001"
  CoarseView = false
  Direction = (1,0,0)
  Focus = 100
  HardHidden = false
  IsoCount = 0
  IsoHidden = false
  IsoVisible = false
  LockPosition = true
  Perspective = false
  Rotation = 0
  RotationVector = (0,-1,0)
  Scale = 1.5
  ScaleType = 2
  ScrubCount = 0
  SeamHidden = false
  SeamVisible = false
  SmoothHidden = false
  SmoothVisible = true
  Source = -> [Cut006_solid]
  Type = 0
  X = 0
  XDirection = (0,-1,0)
  Y = 0
FEATURE [TechDraw::DrawProjGroupItem] ProjItem004  label="Bottom"
  CoarseView = false
  Direction = (0,0,1)
  Focus = 100
  HardHidden = false
  IsoCount = 0
  IsoHidden = false
  IsoVisible = false
  LockPosition = false
  Perspective = false
  Rotation = 0
  RotationVector = (1,0,0)
  Scale = 1.5
  ScaleType = 2
  ScrubCount = 0
  SeamHidden = false
  SeamVisible = false
  SmoothHidden = false
  SmoothVisible = true
  Source = -> [Cut006_solid]
  Type = 5
  X = 0
  XDirection = (0,-1,0)
  Y = 59.7197
FEATURE [TechDraw::DrawProjGroupItem] ProjItem005  label="Top"
  CoarseView = false
  Direction = (0,0,-1)
  Focus = 100
  HardHidden = false
  IsoCount = 0
  IsoHidden = false
  IsoVisible = false
  LockPosition = false
  Perspective = false
  Rotation = 0
  RotationVector = (1,0,0)
  Scale = 1.5
  ScaleType = 2
  ScrubCount = 0
  SeamHidden = false
  SeamVisible = false
  SmoothHidden = false
  SmoothVisible = true
  Source = -> [Cut006_solid]
  Type = 4
  X = 0
  XDirection = (0,-1,0)
  Y = -66.6557
FEATURE [TechDraw::DrawProjGroupItem] ProjItem006  label="Left001"
  CoarseView = false
  Direction = (1e-16,1,0)
  Focus = 100
  HardHidden = false
  IsoCount = 0
  IsoHidden = false
  IsoVisible = false
  LockPosition = false
  Perspective = false
  Rotation = 0
  RotationVector = (1,0,0)
  Scale = 1.5
  ScaleType = 2
  ScrubCount = 0
  SeamHidden = false
  SeamVisible = false
  SmoothHidden = false
  SmoothVisible = true
  Source = -> [Cut006_solid]
  Type = 1
  X = 84.3121
  XDirection = (1,-1e-16,0)
  Y = 0
FEATURE [TechDraw::DrawProjGroupItem] ProjItem007  label="Rear001"
  CoarseView = false
  Direction = (-1,0,0)
  Focus = 100
  HardHidden = false
  IsoCount = 0
  IsoHidden = false
  IsoVisible = false
  LockPosition = false
  Perspective = false
  Rotation = 0
  RotationVector = (1,0,0)
  Scale = 1.5
  ScaleType = 2
  ScrubCount = 0
  SeamHidden = false
  SeamVisible = false
  SmoothHidden = false
  SmoothVisible = true
  Source = -> [Cut006_solid]
  Type = 3
  X = 151.913
  XDirection = (0,1,0)
  Y = 0
FEATURE [TechDraw::DrawProjGroup] ProjGroup001
  Anchor = -> ProjItem003
  AutoDistribute = false
  LockPosition = false
  ProjectionType = 0
  Rotation = 0
  Scale = 1.5
  ScaleType = 1
  Source = -> [Cut006_solid]
  Views = -> [ProjItem003,ProjItem004,ProjItem005,ProjItem006,ProjItem007]
  X = 71.7176
  Y = 109.819
  spacingX = 15
  spacingY = 15
FEATURE [TechDraw::DrawViewDimension] Dimension019
  AngleOverride = false
  Arbitrary = false
  ArbitraryTolerances = false
  EqualTolerance = true
  ExtensionAngle = 0
  FormatSpec = %.2w
  FormatSpecOverTolerance = %+.2w
  FormatSpecUnderTolerance = %+.2w
  Inverted = false
  LineAngle = 0
  LockPosition = false
  MeasureType = 1
  OverTolerance = 0
  References2D = -> [ProjItem005]
  Rotation = 0
  ScaleType = 0
  TheoreticalExact = false
  Type = 0
  UnderTolerance = 0
  X = -2.74227
  Y = 17.7496
FEATURE [TechDraw::DrawViewDimension] Dimension020
  AngleOverride = false
  Arbitrary = false
  ArbitraryTolerances = false
  EqualTolerance = true
  ExtensionAngle = 0
  FormatSpec = %.2w
  FormatSpecOverTolerance = %+.2w
  FormatSpecUnderTolerance = %+.2w
  Inverted = false
  LineAngle = 0
  LockPosition = false
  MeasureType = 1
  OverTolerance = 0
  References2D = -> [ProjItem005]
  Rotation = 0
  ScaleType = 0
  TheoreticalExact = false
  Type = 0
  UnderTolerance = 0
  X = -42.4052
  Y = 17.6073
FEATURE [TechDraw::DrawViewDimension] Dimension021
  AngleOverride = false
  Arbitrary = false
  ArbitraryTolerances = false
  EqualTolerance = true
  ExtensionAngle = 0
  FormatSpec = %.2w
  FormatSpecOverTolerance = %+.2w
  FormatSpecUnderTolerance = %+.2w
  Inverted = false
  LineAngle = 0
  LockPosition = false
  MeasureType = 1
  OverTolerance = 0
  References2D = -> [ProjItem004]
  Rotation = 0
  ScaleType = 0
  TheoreticalExact = false
  Type = 0
  UnderTolerance = 0
  X = 38.6315
  Y = 21.9645
FEATURE [TechDraw::DrawViewDimension] Dimension022
  AngleOverride = false
  Arbitrary = false
  ArbitraryTolerances = false
  EqualTolerance = true
  ExtensionAngle = 0
  FormatSpec = %.2w
  FormatSpecOverTolerance = %+.2w
  FormatSpecUnderTolerance = %+.2w
  Inverted = false
  LineAngle = 0
  LockPosition = false
  MeasureType = 1
  OverTolerance = 0
  References2D = -> [ProjItem004]
  Rotation = 0
  ScaleType = 0
  TheoreticalExact = false
  Type = 0
  UnderTolerance = 0
  X = 44.0976
  Y = 10.1057
FEATURE [TechDraw::DrawViewDimension] Dimension023
  AngleOverride = false
  Arbitrary = false
  ArbitraryTolerances = false
  EqualTolerance = true
  ExtensionAngle = 0
  FormatSpec = ⌀%.2w (2x M3)
  FormatSpecOverTolerance = %+.2w
  FormatSpecUnderTolerance = %+.2w
  Inverted = false
  LineAngle = 0
  LockPosition = false
  MeasureType = 1
  OverTolerance = 0
  References2D = -> [ProjItem004]
  Rotation = 0
  ScaleType = 0
  TheoreticalExact = false
  Type = 5
  UnderTolerance = 0
  X = -49.8518
  Y = -22.963
FEATURE [TechDraw::DrawViewDimension] Dimension024
  AngleOverride = false
  Arbitrary = false
  ArbitraryTolerances = false
  EqualTolerance = true
  ExtensionAngle = 0
  FormatSpec = %.2w
  FormatSpecOverTolerance = %+.2w
  FormatSpecUnderTolerance = %+.2w
  Inverted = false
  LineAngle = 0
  LockPosition = false
  MeasureType = 1
  OverTolerance = 0
  References2D = -> [ProjItem003]
  Rotation = 0
  ScaleType = 0
  TheoreticalExact = false
  Type = 0
  UnderTolerance = 0
  X = 26.1719
  Y = 34.0957
FEATURE [TechDraw::DrawViewDimension] Dimension025
  AngleOverride = false
  Arbitrary = false
  ArbitraryTolerances = false
  EqualTolerance = true
  ExtensionAngle = 0
  FormatSpec = %.2w
  FormatSpecOverTolerance = %+.2w
  FormatSpecUnderTolerance = %+.2w
  Inverted = false
  LineAngle = 0
  LockPosition = false
  MeasureType = 1
  OverTolerance = 0
  References2D = -> [ProjItem003]
  Rotation = 0
  ScaleType = 0
  TheoreticalExact = false
  Type = 0
  UnderTolerance = 0
  X = 29.3359
  Y = 42.2976
FEATURE [TechDraw::DrawViewDimension] Dimension026
  AngleOverride = false
  Arbitrary = false
  ArbitraryTolerances = false
  EqualTolerance = true
  ExtensionAngle = 0
  FormatSpec = %.2w
  FormatSpecOverTolerance = %+.2w
  FormatSpecUnderTolerance = %+.2w
  Inverted = false
  LineAngle = 0
  LockPosition = false
  MeasureType = 1
  OverTolerance = 0
  References2D = -> [ProjItem003]
  Rotation = 0
  ScaleType = 0
  TheoreticalExact = false
  Type = 0
  UnderTolerance = 0
  X = 46.3655
  Y = 25.9377
FEATURE [TechDraw::DrawViewDimension] Dimension027
  AngleOverride = false
  Arbitrary = false
  ArbitraryTolerances = false
  EqualTolerance = true
  ExtensionAngle = 0
  FormatSpec = %.2w
  FormatSpecOverTolerance = %+.2w
  FormatSpecUnderTolerance = %+.2w
  Inverted = false
  LineAngle = 0
  LockPosition = false
  MeasureType = 1
  OverTolerance = 0
  References2D = -> [ProjItem003]
  Rotation = 0
  ScaleType = 0
  TheoreticalExact = false
  Type = 0
  UnderTolerance = 0
  X = 40.1856
  Y = 3.86506
FEATURE [TechDraw::DrawViewDimension] Dimension028
  AngleOverride = false
  Arbitrary = false
  ArbitraryTolerances = false
  EqualTolerance = true
  ExtensionAngle = 0
  FormatSpec = %.2w
  FormatSpecOverTolerance = %+.2w
  FormatSpecUnderTolerance = %+.2w
  Inverted = false
  LineAngle = 0
  LockPosition = false
  MeasureType = 1
  OverTolerance = 0
  References2D = -> [ProjItem003]
  Rotation = 0
  ScaleType = 0
  TheoreticalExact = false
  Type = 0
  UnderTolerance = 0
  X = -21.0897
  Y = 32.0725
FEATURE [TechDraw::DrawViewDimension] Dimension029
  AngleOverride = false
  Arbitrary = false
  ArbitraryTolerances = false
  EqualTolerance = true
  ExtensionAngle = 0
  FormatSpec = %.2w
  FormatSpecOverTolerance = %+.2w
  FormatSpecUnderTolerance = %+.2w
  Inverted = false
  LineAngle = 0
  LockPosition = false
  MeasureType = 1
  OverTolerance = 0
  References2D = -> [ProjItem007]
  Rotation = 0
  ScaleType = 0
  TheoreticalExact = false
  Type = 0
  UnderTolerance = 0
  X = 0.798609
  Y = 37.539
FEATURE [TechDraw::DrawViewDimension] Dimension030
  AngleOverride = false
  Arbitrary = false
  ArbitraryTolerances = false
  EqualTolerance = true
  ExtensionAngle = 0
  FormatSpec = %.2w
  FormatSpecOverTolerance = %+.2w
  FormatSpecUnderTolerance = %+.2w
  Inverted = false
  LineAngle = 0
  LockPosition = false
  MeasureType = 1
  OverTolerance = 0
  References2D = -> [ProjItem007]
  Rotation = 0
  ScaleType = 0
  TheoreticalExact = false
  Type = 0
  UnderTolerance = 0
  X = -2.99683
  Y = -30.5721
FEATURE [TechDraw::DrawViewDimension] Dimension031
  AngleOverride = false
  Arbitrary = false
  ArbitraryTolerances = false
  EqualTolerance = true
  ExtensionAngle = 0
  FormatSpec = %.2w
  FormatSpecOverTolerance = %+.2w
  FormatSpecUnderTolerance = %+.2w
  Inverted = false
  LineAngle = 0
  LockPosition = false
  MeasureType = 1
  OverTolerance = 0
  References2D = -> [ProjItem004]
  Rotation = 0
  ScaleType = 0
  TheoreticalExact = false
  Type = 0
  UnderTolerance = 0
  X = -28.8881
  Y = -11.5813
FEATURE [TechDraw::DrawViewDimension] Dimension032
  AngleOverride = false
  Arbitrary = false
  ArbitraryTolerances = false
  EqualTolerance = true
  ExtensionAngle = 0
  FormatSpec = %.2w
  FormatSpecOverTolerance = %+.2w
  FormatSpecUnderTolerance = %+.2w
  Inverted = false
  LineAngle = 0
  LockPosition = false
  MeasureType = 1
  OverTolerance = 0
  References2D = -> [ProjItem004]
  Rotation = 0
  ScaleType = 0
  TheoreticalExact = false
  Type = 0
  UnderTolerance = 0
  X = -1.50669
  Y = 20.5059
FEATURE [TechDraw::DrawPage] Page001
  KeepUpdated = true
  NextBalloonIndex = 1
  ProjectionType = 0
  Template = -> Template001
  Views = -> [ProjGroup001,Dimension019,Dimension020,Dimension021,Dimension022,Dimension023,Dimension024,Dimension025,Dimension026,Dimension027,Dimension028,Dimension029,Dimension030,Dimension031,Dimension032]
FEATURE [TechDraw::DrawSVGTemplate] Template002
  EditableTexts = Designed_by_Name=Designed by Name; Drawing_number=Drawing number; FC-Date=Date; FC-SC=Scale; FC-SH=Sheet; FC-Title=Title; Subtitle=Subtitle; Weight=Weight
  Height = 210
  Orientation = 1
  Template = <path>
  Width = 297
FEATURE [TechDraw::DrawViewPart] View
  CoarseView = false
  Direction = (1,0,0)
  Focus = 100
  HardHidden = false
  IsoCount = 0
  IsoHidden = false
  IsoVisible = false
  LockPosition = false
  Perspective = false
  Rotation = 0
  ScaleType = 0
  ScrubCount = 0
  SeamHidden = false
  SeamVisible = false
  SmoothHidden = false
  SmoothVisible = true
  Source = -> [Cut006_solid]
  X = 213.863
  XDirection = (0,-1,0)
  Y = 154.674
FEATURE [TechDraw::DrawViewPart] View001
  CoarseView = false
  Direction = (1,0,0)
  Focus = 100
  HardHidden = false
  IsoCount = 0
  IsoHidden = false
  IsoVisible = false
  LockPosition = false
  Perspective = false
  Rotation = 0
  ScaleType = 0
  ScrubCount = 0
  SeamHidden = false
  SeamVisible = false
  SmoothHidden = false
  SmoothVisible = true
  Source = -> [Cut006_solid]
  X = 76.3703
  XDirection = (0,-1,0)
  Y = 177.393
FEATURE [TechDraw::DrawViewSection] SectionView001  label="Section001  - "
  BaseView = -> View
  CoarseView = false
  CutSurfaceDisplay = 2
  Direction = (0,-1e-16,-1)
  FileGeomPattern = <path>
  FileHatchPattern = <path>
  Focus = 100
  FuseBeforeCut = false
  HardHidden = false
  HatchOffset = (0,0,0)
  HatchRotation = 0
  HatchScale = 1
  IsoCount = 0
  IsoHidden = false
  IsoVisible = false
  LockPosition = false
  NameGeomPattern = Diamond
  Perspective = false
  Rotation = 0
  Scale = 3
  ScaleType = 2
  ScrubCount = 0
  SeamHidden = false
  SeamVisible = false
  SectionDirection = 4
  SectionLineStretch = 1
  SectionNormal = (0,-1e-16,-1)
  SectionOrigin = (6,0,-12.5)
  SmoothHidden = false
  SmoothVisible = true
  Source = -> [Cut006_solid]
  TrimAfterCut = false
  UsePreviousCut = false
  X = 212.652
  XDirection = (0,-1,1e-16)
  Y = 93.0024
FEATURE [TechDraw::DrawViewDimension] Dimension033
  AngleOverride = false
  Arbitrary = false
  ArbitraryTolerances = false
  EqualTolerance = true
  ExtensionAngle = 0
  FormatSpec = %.2w
  FormatSpecOverTolerance = %+.2w
  FormatSpecUnderTolerance = %+.2w
  Inverted = false
  LineAngle = 0
  LockPosition = false
  MeasureType = 1
  OverTolerance = 0
  References2D = -> [SectionView001]
  Rotation = 0
  ScaleType = 0
  TheoreticalExact = false
  Type = 0
  UnderTolerance = 0
  X = 64.9192
  Y = -25.9707
FEATURE [TechDraw::DrawViewDimension] Dimension034
  AngleOverride = false
  Arbitrary = false
  ArbitraryTolerances = false
  EqualTolerance = true
  ExtensionAngle = 0
  FormatSpec = %.2w
  FormatSpecOverTolerance = %+.2w
  FormatSpecUnderTolerance = %+.2w
  Inverted = false
  LineAngle = 0
  LockPosition = false
  MeasureType = 1
  OverTolerance = 0
  References2D = -> [SectionView001]
  Rotation = 0
  ScaleType = 0
  TheoreticalExact = false
  Type = 0
  UnderTolerance = 0
  X = 66.5714
  Y = 28.6268
FEATURE [TechDraw::DrawViewDimension] Dimension035
  AngleOverride = false
  Arbitrary = false
  ArbitraryTolerances = false
  EqualTolerance = true
  ExtensionAngle = 0
  FormatSpec = %.2w
  FormatSpecOverTolerance = %+.2w
  FormatSpecUnderTolerance = %+.2w
  Inverted = false
  LineAngle = 0
  LockPosition = false
  MeasureType = 1
  OverTolerance = 0
  References2D = -> [SectionView001]
  Rotation = 0
  ScaleType = 0
  TheoreticalExact = false
  Type = 0
  UnderTolerance = 0
  X = 8.62255
  Y = -13.8392
FEATURE [TechDraw::DrawViewDimension] Dimension036
  AngleOverride = false
  Arbitrary = false
  ArbitraryTolerances = false
  EqualTolerance = true
  ExtensionAngle = 0
  FormatSpec = %.2w
  FormatSpecOverTolerance = %+.2w
  FormatSpecUnderTolerance = %+.2w
  Inverted = false
  LineAngle = 0
  LockPosition = false
  MeasureType = 1
  OverTolerance = 0
  References2D = -> [SectionView001]
  Rotation = 0
  ScaleType = 0
  TheoreticalExact = false
  Type = 0
  UnderTolerance = 0
  X = 47.3332
  Y = -18.2954
FEATURE [TechDraw::DrawViewSection] SectionView002  label="Section002  - "
  BaseView = -> View001
  CoarseView = false
  CutSurfaceDisplay = 2
  Direction = (0,-1e-16,-1)
  FileGeomPattern = <path>
  FileHatchPattern = <path>
  Focus = 100
  FuseBeforeCut = false
  HardHidden = false
  HatchOffset = (0,0,0)
  HatchRotation = 0
  HatchScale = 1
  IsoCount = 0
  IsoHidden = false
  IsoVisible = false
  LockPosition = false
  NameGeomPattern = Diamond
  Perspective = false
  Rotation = 0
  Scale = 3
  ScaleType = 2
  ScrubCount = 0
  SeamHidden = false
  SeamVisible = false
  SectionDirection = 4
  SectionLineStretch = 1
  SectionNormal = (0,-1e-16,-1)
  SectionOrigin = (6,0,-2.5)
  SmoothHidden = false
  SmoothVisible = true
  Source = -> [Cut006_solid]
  TrimAfterCut = false
  UsePreviousCut = false
  X = 79.6226
  XDirection = (0,-1,1e-16)
  Y = 118.575
FEATURE [TechDraw::DrawViewDimension] Dimension037
  AngleOverride = false
  Arbitrary = false
  ArbitraryTolerances = false
  EqualTolerance = true
  ExtensionAngle = 0
  FormatSpec = %.2w
  FormatSpecOverTolerance = %+.2w
  FormatSpecUnderTolerance = %+.2w
  Inverted = false
  LineAngle = 0
  LockPosition = false
  MeasureType = 1
  OverTolerance = 0
  References2D = -> [SectionView002]
  Rotation = 0
  ScaleType = 0
  TheoreticalExact = false
  Type = 0
  UnderTolerance = 0
  X = 0.325776
  Y = -3.69577
FEATURE [TechDraw::DrawViewDimension] Dimension038
  AngleOverride = false
  Arbitrary = false
  ArbitraryTolerances = false
  EqualTolerance = true
  ExtensionAngle = 0
  FormatSpec = %.2w
  FormatSpecOverTolerance = %+.2w
  FormatSpecUnderTolerance = %+.2w
  Inverted = false
  LineAngle = 0
  LockPosition = false
  MeasureType = 1
  OverTolerance = 0
  References2D = -> [SectionView002]
  Rotation = 0
  ScaleType = 0
  TheoreticalExact = false
  Type = 0
  UnderTolerance = 0
  X = 0.255463
  Y = 4.6556
FEATURE [TechDraw::DrawViewDimension] Dimension039
  AngleOverride = false
  Arbitrary = false
  ArbitraryTolerances = false
  EqualTolerance = true
  ExtensionAngle = 0
  FormatSpec = %.2w
  FormatSpecOverTolerance = %+.2w
  FormatSpecUnderTolerance = %+.2w
  Inverted = false
  LineAngle = 0
  LockPosition = false
  MeasureType = 1
  OverTolerance = 0
  References2D = -> [SectionView002]
  Rotation = 0
  ScaleType = 0
  TheoreticalExact = false
  Type = 0
  UnderTolerance = 0
  X = 79.5736
  Y = 0.671184
FEATURE [TechDraw::DrawViewDimension] Dimension040
  AngleOverride = false
  Arbitrary = false
  ArbitraryTolerances = false
  EqualTolerance = true
  ExtensionAngle = 0
  FormatSpec = ⌀%.2w (2x M3)
  FormatSpecOverTolerance = %+.2w
  FormatSpecUnderTolerance = %+.2w
  Inverted = false
  LineAngle = 0
  LockPosition = false
  MeasureType = 1
  OverTolerance = 0
  References2D = -> [SectionView002]
  Rotation = 0
  ScaleType = 0
  TheoreticalExact = false
  Type = 5
  UnderTolerance = 0
  X = 64.4898
  Y = 40.7105
FEATURE [TechDraw::DrawViewDimension] Dimension041
  AngleOverride = false
  Arbitrary = false
  ArbitraryTolerances = false
  EqualTolerance = true
  ExtensionAngle = 0
  FormatSpec = %.2w
  FormatSpecOverTolerance = %+.2w
  FormatSpecUnderTolerance = %+.2w
  Inverted = false
  LineAngle = 0
  LockPosition = false
  MeasureType = 1
  OverTolerance = 0
  References2D = -> [SectionView002]
  Rotation = 0
  ScaleType = 0
  TheoreticalExact = false
  Type = 0
  UnderTolerance = 0
  X = 78.1881
  Y = 8.43953
FEATURE [TechDraw::DrawViewDimension] Dimension042
  AngleOverride = false
  Arbitrary = false
  ArbitraryTolerances = false
  EqualTolerance = true
  ExtensionAngle = 0
  FormatSpec = R%.2w
  FormatSpecOverTolerance = %+.2w
  FormatSpecUnderTolerance = %+.2w
  Inverted = false
  LineAngle = 0
  LockPosition = false
  MeasureType = 1
  OverTolerance = 0
  References2D = -> [SectionView002]
  Rotation = 0
  ScaleType = 0
  TheoreticalExact = false
  Type = 4
  UnderTolerance = 0
  X = -21.5107
  Y = 13.7302
FEATURE [TechDraw::DrawViewDimension] Dimension043
  AngleOverride = false
  Arbitrary = false
  ArbitraryTolerances = false
  EqualTolerance = true
  ExtensionAngle = 0
  FormatSpec = %.2w
  FormatSpecOverTolerance = %+.2w
  FormatSpecUnderTolerance = %+.2w
  Inverted = false
  LineAngle = 0
  LockPosition = false
  MeasureType = 1
  OverTolerance = 0
  References2D = -> [SectionView002]
  Rotation = 0
  ScaleType = 0
  TheoreticalExact = false
  Type = 0
  UnderTolerance = 0
  X = 45.5158
  Y = 34.0796
FEATURE [TechDraw::DrawPage] Page002
  KeepUpdated = true
  NextBalloonIndex = 1
  ProjectionType = 0
  Template = -> Template002
  Views = -> [View,View001,SectionView001,Dimension033,Dimension034,Dimension035,Dimension036,SectionView002,Dimension037,Dimension038,Dimension039,Dimension040,Dimension041,Dimension042,Dimension043]
note: 9 file-system paths scrubbed to <path> (originals preserved in the JSON sidecar)
---- part PhilipsXL30_Blindflange_100_TopBack.FCStd = doc fcstd_c43266b599bf ----
FCSTD DOCUMENT  (FreeCAD 0.20R)
Label: PhilipsXL30_Blindflange_100_TopBack
License: All rights reserved
LicenseURL: http://en.wikipedia.org/wiki/All_rights_reserved
objects: TechDraw::DrawViewDimension×18, Part::Cylinder×9, Part::Compound×6, Part::Cut×5, TechDraw::DrawProjGroupItem×3, Part::Box×1, TechDraw::DrawSVGTemplate×1, TechDraw::DrawProjGroup×1, TechDraw::DrawViewSection×1, TechDraw::DrawPage×1
note: 21 computed .brp shape members not serialized (recipe doc carries the construction recipe); baked Part::Feature solids carry a one-line shape summary decoded from their .brp

FEATURE [Part::Cylinder] Cylinder
  Angle = 360
  AttacherType = Attacher::AttachEngine3D
  FirstAngle = 0
  Height = 12
  Radius = 50
  SecondAngle = 0
FEATURE [Part::Cylinder] Cylinder001
  Angle = 360
  AttacherType = Attacher::AttachEngine3D
  FirstAngle = 0
  Height = 3
  Radius = 37.5
  SecondAngle = 0
FEATURE [Part::Cylinder] Cylinder002
  Angle = 360
  AttacherType = Attacher::AttachEngine3D
  FirstAngle = 0
  Height = 3
  Radius = 41
  SecondAngle = 0
FEATURE [Part::Cut] Cut
  Base = -> Cylinder002
  Placement = pos=(0,0,9) rot=(0,0,1;0rad)
  Tool = -> Cylinder001
FEATURE [Part::Cut] Cut001
  Base = -> Cylinder
  Tool = -> Cut
FEATURE [Part::Box] Box  label="Cube"
  AttacherType = Attacher::AttachEngine3D
  Height = 12
  Length = 200
  Placement = pos=(-100,44,0) rot=(0,0,1;0rad)
  Width = 100
FEATURE [Part::Cut] Cut002
  Base = -> Cut001
  Tool = -> Box
FEATURE [Part::Cylinder] Cylinder003
  Angle = 360
  AttacherType = Attacher::AttachEngine3D
  FirstAngle = 0
  Height = 12
  Placement = pos=(0,-43.5,0) rot=(0,0,1;0rad)
  Radius = 2.5
  SecondAngle = 0
FEATURE [Part::Cylinder] Cylinder004
  Angle = 360
  AttacherType = Attacher::AttachEngine3D
  FirstAngle = 0
  Height = 12
  Placement = pos=(0,-43.5,0) rot=(0,0,1;0rad)
  Radius = 2.5
  SecondAngle = 0
FEATURE [Part::Cylinder] Cylinder005
  Angle = 360
  AttacherType = Attacher::AttachEngine3D
  FirstAngle = 0
  Height = 12
  Placement = pos=(0,-43.5,0) rot=(0,0,1;0rad)
  Radius = 2.5
  SecondAngle = 0
FEATURE [Part::Compound] Compound
  Links = -> [Cylinder004]
  Placement = pos=(0,0,0) rot=(0,0,1;2.07694rad)
FEATURE [Part::Compound] Compound001
  Links = -> [Cylinder005]
  Placement = pos=(0,0,0) rot=(0,0,1;-2.07694rad)
FEATURE [Part::Compound] Compound002
  Links = -> [Cylinder003,Compound,Compound001]
FEATURE [Part::Cut] Cut003
  Base = -> Cut002
  Tool = -> Compound002
FEATURE [Part::Cylinder] Cylinder006
  Angle = 360
  AttacherType = Attacher::AttachEngine3D
  FirstAngle = 0
  Height = 6
  Placement = pos=(0,-43.5,0) rot=(0,0,1;0rad)
  Radius = 5
  SecondAngle = 0
FEATURE [Part::Cylinder] Cylinder007
  Angle = 360
  AttacherType = Attacher::AttachEngine3D
  FirstAngle = 0
  Height = 5
  Placement = pos=(0,-43.5,0) rot=(0,0,1;0rad)
  Radius = 5
  SecondAngle = 0
FEATURE [Part::Compound] Compound003
  Links = -> [Cylinder007]
  Placement = pos=(0,0,0) rot=(0,0,1;2.07694rad)
FEATURE [Part::Cylinder] Cylinder008
  Angle = 360
  AttacherType = Attacher::AttachEngine3D
  FirstAngle = 0
  Height = 6
  Placement = pos=(0,-43.5,0) rot=(0,0,1;0rad)
  Radius = 5
  SecondAngle = 0
FEATURE [Part::Compound] Compound004
  Links = -> [Cylinder008]
  Placement = pos=(0,0,0) rot=(0,0,-1;2.07694rad)
FEATURE [Part::Compound] Compound005
  Links = -> [Cylinder006,Compound003,Compound004]
FEATURE [Part::Cut] Cut004  label="XL30TopBackFlange100"
  Base = -> Cut003
  Tool = -> Compound005
FEATURE [TechDraw::DrawSVGTemplate] Template
  EditableTexts = Designed_by_Name=Thomas Spielauer; Drawing_number=1; FC-Date=2023-12-18; FC-SC=mm; FC-Title=XL30 compatible 100m flange; Subtitle=Back side top left
  Height = 210
  Orientation = 1
  Width = 297
FEATURE [TechDraw::DrawProjGroupItem] ProjItem  label="Front"
  CoarseView = false
  Direction = (0,0,1)
  Focus = 100
  HardHidden = false
  IsoCount = 0
  IsoHidden = false
  IsoVisible = false
  LockPosition = true
  Perspective = false
  Rotation = 0
  RotationVector = (-1,0,0)
  ScaleType = 2
  SeamHidden = false
  SeamVisible = true
  SmoothHidden = false
  SmoothVisible = true
  Source = -> [Cut004]
  Type = 0
  X = 0
  XDirection = (-1,0,0)
  Y = 0
FEATURE [TechDraw::DrawProjGroupItem] ProjItem002  label="Rear"
  CoarseView = false
  Direction = (0,0,-1)
  Focus = 100
  HardHidden = false
  IsoCount = 0
  IsoHidden = false
  IsoVisible = false
  LockPosition = false
  Perspective = false
  Rotation = 0
  RotationVector = (1,0,0)
  ScaleType = 2
  SeamHidden = false
  SeamVisible = true
  SmoothHidden = false
  SmoothVisible = true
  Source = -> [Cut004]
  Type = 3
  X = 112.613
  XDirection = (1,0,0)
  Y = 0
FEATURE [TechDraw::DrawProjGroupItem] ProjItem003  label="Top"
  CoarseView = false
  Direction = (0,-1,0)
  Focus = 100
  HardHidden = false
  IsoCount = 0
  IsoHidden = false
  IsoVisible = false
  LockPosition = false
  Perspective = false
  Rotation = 0
  RotationVector = (1,0,0)
  ScaleType = 2
  SeamHidden = false
  SeamVisible = true
  SmoothHidden = false
  SmoothVisible = true
  Source = -> [Cut004]
  Type = 4
  X = 0
  XDirection = (-1,0,0)
  Y = -112.049
FEATURE [TechDraw::DrawProjGroup] ProjGroup
  Anchor = -> ProjItem
  AutoDistribute = false
  LockPosition = false
  ProjectionType = 0
  Rotation = 0
  ScaleType = 0
  Source = -> [Cut004]
  Views = -> [ProjItem,ProjItem002,ProjItem003]
  X = 71.1104
  Y = 147.781
  spacingX = 15
  spacingY = 15
FEATURE [TechDraw::DrawViewDimension] Dimension
  AngleOverride = false
  Arbitrary = false
  ArbitraryTolerances = false
  EqualTolerance = true
  ExtensionAngle = 0
  FormatSpec = ⌀%.2w
  FormatSpecOverTolerance = %+.2w
  FormatSpecUnderTolerance = %+.2w
  Inverted = false
  LineAngle = 0
  LockPosition = false
  MeasureType = 1
  OverTolerance = 0
  References2D = -> [ProjItem]
  Rotation = 0
  ScaleType = 0
  TheoreticalExact = false
  Type = 5
  UnderTolerance = 0
  X = 32.6688
  Y = 47.2408
FEATURE [TechDraw::DrawViewDimension] Dimension001
  AngleOverride = false
  Arbitrary = false
  ArbitraryTolerances = false
  EqualTolerance = true
  ExtensionAngle = 0
  FormatSpec = ⌀%.2w
  FormatSpecOverTolerance = %+.2w
  FormatSpecUnderTolerance = %+.2w
  Inverted = false
  LineAngle = 0
  LockPosition = false
  MeasureType = 1
  OverTolerance = 0
  References2D = -> [ProjItem]
  Rotation = 0
  ScaleType = 0
  TheoreticalExact = false
  Type = 5
  UnderTolerance = 0
  X = 51.305
  Y = 16.9487
FEATURE [TechDraw::DrawViewDimension] Dimension002
  AngleOverride = false
  Arbitrary = false
  ArbitraryTolerances = false
  EqualTolerance = true
  ExtensionAngle = 0
  FormatSpec = ⌀%.2w
  FormatSpecOverTolerance = %+.2w
  FormatSpecUnderTolerance = %+.2w
  Inverted = false
  LineAngle = 0
  LockPosition = false
  MeasureType = 1
  OverTolerance = 0
  References2D = -> [ProjItem]
  Rotation = 0
  ScaleType = 0
  TheoreticalExact = false
  Type = 5
  UnderTolerance = 0
  X = 54.375
  Y = 11.2918
FEATURE [TechDraw::DrawViewDimension] Dimension003
  AngleOverride = false
  Arbitrary = false
  ArbitraryTolerances = false
  EqualTolerance = true
  ExtensionAngle = 0
  FormatSpec = ⌀%.2w
  FormatSpecOverTolerance = %+.2w
  FormatSpecUnderTolerance = %+.2w
  Inverted = false
  LineAngle = 0
  LockPosition = false
  MeasureType = 1
  OverTolerance = 0
  References2D = -> [ProjItem]
  Rotation = 0
  ScaleType = 0
  TheoreticalExact = false
  Type = 5
  UnderTolerance = 0
  X = 40.665
  Y = 45.6731
FEATURE [TechDraw::DrawViewDimension] Dimension004
  AngleOverride = false
  Arbitrary = false
  ArbitraryTolerances = false
  EqualTolerance = true
  ExtensionAngle = 0
  FormatSpec = ⌀%.2w (3x)
  FormatSpecOverTolerance = %+.2w
  FormatSpecUnderTolerance = %+.2w
  Inverted = false
  LineAngle = 0
  LockPosition = false
  MeasureType = 1
  OverTolerance = 0
  References2D = -> [ProjItem]
  Rotation = 0
  ScaleType = 0
  TheoreticalExact = false
  Type = 5
  UnderTolerance = 0
  X = -41.9055
  Y = 45.1875
FEATURE [TechDraw::DrawViewDimension] Dimension005
  AngleOverride = false
  Arbitrary = false
  ArbitraryTolerances = false
  EqualTolerance = true
  ExtensionAngle = 0
  FormatSpec = %.2w
  FormatSpecOverTolerance = %+.2w
  FormatSpecUnderTolerance = %+.2w
  Inverted = false
  LineAngle = 0
  LockPosition = false
  MeasureType = 1
  OverTolerance = 0
  References2D = -> [ProjItem]
  Rotation = 0
  ScaleType = 0
  TheoreticalExact = false
  Type = 6
  UnderTolerance = 0
  X = -13.992
  Y = -14.5232
FEATURE [TechDraw::DrawViewDimension] Dimension006
  AngleOverride = false
  Arbitrary = false
  ArbitraryTolerances = false
  EqualTolerance = true
  ExtensionAngle = 0
  FormatSpec = %.2w
  FormatSpecOverTolerance = %+.2w
  FormatSpecUnderTolerance = %+.2w
  Inverted = false
  LineAngle = 0
  LockPosition = false
  MeasureType = 1
  OverTolerance = 0
  References2D = -> [ProjItem]
  Rotation = 0
  ScaleType = 0
  TheoreticalExact = false
  Type = 6
  UnderTolerance = 0
  X = 15.1619
  Y = -18.6647
FEATURE [TechDraw::DrawViewDimension] Dimension007
  AngleOverride = false
  Arbitrary = false
  ArbitraryTolerances = false
  EqualTolerance = true
  ExtensionAngle = 0
  FormatSpec = ⌀%.2w
  FormatSpecOverTolerance = %+.2w
  FormatSpecUnderTolerance = %+.2w
  Inverted = false
  LineAngle = 0
  LockPosition = false
  MeasureType = 1
  OverTolerance = 0
  References2D = -> [ProjItem002]
  Rotation = 0
  ScaleType = 0
  TheoreticalExact = false
  Type = 5
  UnderTolerance = 0
  X = 30.2276
  Y = 46.2839
FEATURE [TechDraw::DrawViewDimension] Dimension008
  AngleOverride = false
  Arbitrary = false
  ArbitraryTolerances = false
  EqualTolerance = true
  ExtensionAngle = 0
  FormatSpec = %.2w
  FormatSpecOverTolerance = %+.2w
  FormatSpecUnderTolerance = %+.2w
  Inverted = false
  LineAngle = 0
  LockPosition = false
  MeasureType = 1
  OverTolerance = 0
  References2D = -> [ProjItem002]
  Rotation = 0
  ScaleType = 0
  TheoreticalExact = false
  Type = 1
  UnderTolerance = 0
  X = 1.73891
  Y = -33.3071
FEATURE [TechDraw::DrawViewDimension] Dimension009
  AngleOverride = false
  Arbitrary = false
  ArbitraryTolerances = false
  EqualTolerance = true
  ExtensionAngle = 0
  FormatSpec = %.2w
  FormatSpecOverTolerance = %+.2w
  FormatSpecUnderTolerance = %+.2w
  Inverted = false
  LineAngle = 0
  LockPosition = false
  MeasureType = 1
  OverTolerance = 0
  References2D = -> [ProjItem002]
  Rotation = 0
  ScaleType = 0
  TheoreticalExact = false
  Type = 2
  UnderTolerance = 0
  X = -7.34944
  Y = -21.677
FEATURE [TechDraw::DrawViewDimension] Dimension010
  AngleOverride = false
  Arbitrary = false
  ArbitraryTolerances = false
  EqualTolerance = true
  ExtensionAngle = 0
  FormatSpec = %.2w
  FormatSpecOverTolerance = %+.2w
  FormatSpecUnderTolerance = %+.2w
  Inverted = false
  LineAngle = 0
  LockPosition = false
  MeasureType = 1
  OverTolerance = 0
  References2D = -> [ProjItem003]
  Rotation = 0
  ScaleType = 0
  TheoreticalExact = false
  Type = 2
  UnderTolerance = 0
  X = 58.602
  Y = 14.0619
FEATURE [TechDraw::DrawViewSection] SectionView  label="Section  - "
  BaseView = -> ProjItem002
  CoarseView = false
  CutSurfaceDisplay = 2
  Direction = (-1,0,0)
  FileGeomPattern = <path>
  FileHatchPattern = <path>
  Focus = 100
  FuseBeforeCut = false
  HardHidden = false
  HatchScale = 1
  IsoCount = 0
  IsoHidden = false
  IsoVisible = false
  LockPosition = false
  NameGeomPattern = Diamond
  Perspective = false
  Rotation = 0
  ScaleType = 2
  SeamHidden = false
  SeamVisible = true
  SectionDirection = 0
  SectionNormal = (-1,0,0)
  SectionOrigin = (0.044,-2.97,6)
  SmoothHidden = false
  SmoothVisible = true
  Source = -> [Cut004]
  X = 264.208
  XDirection = (0,0,-1)
  Y = 135.168
FEATURE [TechDraw::DrawViewDimension] Dimension011
  AngleOverride = false
  Arbitrary = false
  ArbitraryTolerances = false
  EqualTolerance = true
  ExtensionAngle = 0
  FormatSpec = %.2w
  FormatSpecOverTolerance = %+.2w
  FormatSpecUnderTolerance = %+.2w
  Inverted = false
  LineAngle = 0
  LockPosition = false
  MeasureType = 1
  OverTolerance = 0
  References2D = -> [SectionView]
  Rotation = 0
  ScaleType = 0
  TheoreticalExact = false
  Type = 2
  UnderTolerance = 0
  X = 15.2511
  Y = 31.7095
FEATURE [TechDraw::DrawViewDimension] Dimension012
  AngleOverride = false
  Arbitrary = false
  ArbitraryTolerances = false
  EqualTolerance = true
  ExtensionAngle = 0
  FormatSpec = %.2w
  FormatSpecOverTolerance = %+.2w
  FormatSpecUnderTolerance = %+.2w
  Inverted = false
  LineAngle = 0
  LockPosition = false
  MeasureType = 1
  OverTolerance = 0
  References2D = -> [SectionView]
  Rotation = 0
  ScaleType = 0
  TheoreticalExact = false
  Type = 0
  UnderTolerance = 0
  X = -15.1499
  Y = 49.9924
FEATURE [TechDraw::DrawViewDimension] Dimension013
  AngleOverride = false
  Arbitrary = false
  ArbitraryTolerances = false
  EqualTolerance = true
  ExtensionAngle = 0
  FormatSpec = %.2w
  FormatSpecOverTolerance = %+.2w
  FormatSpecUnderTolerance = %+.2w
  Inverted = false
  LineAngle = 0
  LockPosition = false
  MeasureType = 1
  OverTolerance = 0
  References2D = -> [SectionView]
  Rotation = 0
  ScaleType = 0
  TheoreticalExact = false
  Type = 0
  UnderTolerance = 0
  X = -15.7993
  Y = -26.0238
FEATURE [TechDraw::DrawViewDimension] Dimension014
  AngleOverride = false
  Arbitrary = false
  ArbitraryTolerances = false
  EqualTolerance = true
  ExtensionAngle = 0
  FormatSpec = %.2w
  FormatSpecOverTolerance = %+.2w
  FormatSpecUnderTolerance = %+.2w
  Inverted = false
  LineAngle = 0
  LockPosition = false
  MeasureType = 1
  OverTolerance = 0
  References2D = -> [SectionView]
  Rotation = 0
  ScaleType = 0
  TheoreticalExact = false
  Type = 0
  UnderTolerance = 0
  X = 7.4555
  Y = -57.2723
FEATURE [TechDraw::DrawViewDimension] Dimension015
  AngleOverride = false
  Arbitrary = false
  ArbitraryTolerances = false
  EqualTolerance = true
  ExtensionAngle = 0
  FormatSpec = %.2w
  FormatSpecOverTolerance = %+.2w
  FormatSpecUnderTolerance = %+.2w
  Inverted = false
  LineAngle = 0
  LockPosition = false
  MeasureType = 1
  OverTolerance = 0
  References2D = -> [SectionView]
  Rotation = 0
  ScaleType = 0
  TheoreticalExact = false
  Type = 0
  UnderTolerance = 0
  X = 12.3852
  Y = 64.439
FEATURE [TechDraw::DrawViewDimension] Dimension016
  AngleOverride = false
  Arbitrary = false
  ArbitraryTolerances = false
  EqualTolerance = true
  ExtensionAngle = 0
  FormatSpec = %.2w
  FormatSpecOverTolerance = %+.2w
  FormatSpecUnderTolerance = %+.2w
  Inverted = false
  LineAngle = 0
  LockPosition = false
  MeasureType = 1
  OverTolerance = 0
  References2D = -> [SectionView]
  Rotation = 0
  ScaleType = 0
  TheoreticalExact = false
  Type = 0
  UnderTolerance = 0
  X = -7.31285
  Y = 57.1646
FEATURE [TechDraw::DrawViewDimension] Dimension017
  AngleOverride = false
  Arbitrary = false
  ArbitraryTolerances = false
  EqualTolerance = true
  ExtensionAngle = 0
  FormatSpec = %.2w
  FormatSpecOverTolerance = %+.2w
  FormatSpecUnderTolerance = %+.2w
  Inverted = false
  LineAngle = 0
  LockPosition = false
  MeasureType = 1
  OverTolerance = 0
  References2D = -> [ProjItem003]
  Rotation = 0
  ScaleType = 0
  TheoreticalExact = false
  Type = 0
  UnderTolerance = 0
  X = -4.76361
  Y = 18.035
FEATURE [TechDraw::DrawPage] Page
  KeepUpdated = true
  NextBalloonIndex = 1
  ProjectionType = 0
  Template = -> Template
  Views = -> [ProjGroup,Dimension,Dimension001,Dimension002,Dimension003,Dimension004,Dimension005,Dimension006,Dimension007,Dimension008,Dimension009,Dimension010,SectionView,Dimension011,Dimension012,Dimension013,Dimension014,Dimension015,Dimension016,Dimension017]
note: 2 file-system paths scrubbed to <path> (originals preserved in the JSON sidecar)
---- part PhilipsXL30_FlangeToCF35_CF40_ZeroLengthAdapter.FCStd = doc fcstd_0329f2a02e61 ----
FCSTD DOCUMENT  (FreeCAD 0.21R0.20.1)
Label: PhilipsXL30_FlangeToCF35_CF40_ZeroLengthAdapter
License: All rights reserved
LicenseURL: http://en.wikipedia.org/wiki/All_rights_reserved
objects: TechDraw::DrawViewDimension×34, Part::Cylinder×5, TechDraw::DrawProjGroupItem×4, Part::Compound×3, Part::Cut×3, TechDraw::DrawSVGTemplate×3, TechDraw::DrawPage×3, TechDraw::DrawProjGroup×2, TechDraw::DrawViewSection×2, Part::Feature×1, App::Link×1, Part::MultiFuse×1, TechDraw::DrawViewPart×1
note: 13 computed .brp shape members not serialized (recipe doc carries the construction recipe); baked Part::Feature solids carry a one-line shape summary decoded from their .brp
EXTERNAL_REF file=PhilipsXL30_Blindflange.FCStd obj=Cut001_solid

FEATURE [Part::Feature] Solid  label="CF35 Flange"
  Placement = pos=(0,0,4.6) rot=(1,0,0;1.5708rad)
  shape: bbox 70 x 70 x 12.7 mm, 58 faces (baked)
FEATURE [App::Link] Link  label="Cut001 (Solid)"
  LinkedObject = -> <external PhilipsXL30_Blindflange.FCStd>#Cut001_solid
FEATURE [Part::Cylinder] Cylinder004  label="Zylinder004"
  Angle = 360
  AttacherType = Attacher::AttachEngine3D
  FirstAngle = 0
  Height = 12
  Placement = pos=(37.5,0,7) rot=(0,0,1;0rad)
  Radius = 5
  SecondAngle = 0
FEATURE [Part::Cylinder] Cylinder005  label="Zylinder005"
  Angle = 360
  AttacherType = Attacher::AttachEngine3D
  FirstAngle = 0
  Height = 12
  Placement = pos=(37.5,0,7) rot=(0,0,1;0rad)
  Radius = 5
  SecondAngle = 0
FEATURE [Part::Compound] Compound
  Links = -> [Cylinder005]
  Placement = pos=(0,0,0) rot=(0,0,1;2.0944rad)
FEATURE [Part::Cylinder] Cylinder006  label="Zylinder006"
  Angle = 360
  AttacherType = Attacher::AttachEngine3D
  FirstAngle = 0
  Height = 12
  Placement = pos=(37.5,0,7) rot=(0,0,1;0rad)
  Radius = 5
  SecondAngle = 0
FEATURE [Part::Compound] Compound001
  Links = -> [Cylinder006]
  Placement = pos=(0,0,0) rot=(0,0,1;4.18879rad)
FEATURE [Part::Compound] Compound002
  Links = -> [Compound001,Cylinder004,Compound]
FEATURE [Part::Cut] Cut
  Base = -> Solid
  Tool = -> Compound002
FEATURE [Part::Cylinder] Cylinder  label="Zylinder"
  Angle = 360
  AttacherType = Attacher::AttachEngine3D
  FirstAngle = 0
  Height = 50
  Placement = pos=(0,0,-1) rot=(0,0,1;0rad)
  Radius = 20
  SecondAngle = 0
FEATURE [Part::Cylinder] Cylinder007  label="Zylinder007"
  Angle = 360
  AttacherType = Attacher::AttachEngine3D
  FirstAngle = 0
  Height = 12.5
  Placement = pos=(0,0,5) rot=(0,0,1;0rad)
  Radius = 34.95
  SecondAngle = 0
FEATURE [Part::Cut] Cut001
  Base = -> Link
  Tool = -> Cylinder007
FEATURE [Part::MultiFuse] Fusion
  Shapes = -> [Cut,Cut001]
FEATURE [Part::Cut] Cut002
  Base = -> Fusion
  Tool = -> Cylinder
FEATURE [TechDraw::DrawSVGTemplate] Template
  EditableTexts = Designed_by_Name=Thomas Spielauer; Drawing_number=Drawing number; FC-Date=2023-06-20; FC-SC=mm; FC-SH=01/03; FC-Title=Philipps XL30 compatible; Subtitle=Flange to CF35/CF40 ZLA
  Height = 210
  Orientation = 1
  Width = 297
FEATURE [TechDraw::DrawProjGroupItem] ProjItem  label="Front"
  CoarseView = false
  Direction = (0,0,1)
  Focus = 100
  HardHidden = false
  IsoCount = 0
  IsoHidden = false
  IsoVisible = false
  LockPosition = true
  Perspective = false
  Rotation = 0
  RotationVector = (-1,0,0)
  ScaleType = 2
  SeamHidden = false
  SeamVisible = true
  SmoothHidden = false
  SmoothVisible = true
  Source = -> [Cut002]
  Type = 0
  X = 0
  XDirection = (-1,0,0)
  Y = 0
FEATURE [TechDraw::DrawProjGroupItem] ProjItem001  label="Right"
  CoarseView = false
  Direction = (-1,0,1e-16)
  Focus = 100
  HardHidden = false
  IsoCount = 0
  IsoHidden = false
  IsoVisible = false
  LockPosition = false
  Perspective = false
  Rotation = 0
  RotationVector = (1,0,0)
  ScaleType = 2
  SeamHidden = false
  SeamVisible = true
  SmoothHidden = false
  SmoothVisible = true
  Source = -> [Cut002]
  Type = 2
  X = -80.7301
  XDirection = (-1e-16,0,-1)
  Y = 0
FEATURE [TechDraw::DrawProjGroupItem] ProjItem002  label="Rear"
  CoarseView = false
  Direction = (0,0,-1)
  Focus = 100
  HardHidden = false
  IsoCount = 0
  IsoHidden = false
  IsoVisible = false
  LockPosition = false
  Perspective = false
  Rotation = 0
  RotationVector = (1,0,0)
  ScaleType = 2
  SeamHidden = false
  SeamVisible = true
  SmoothHidden = false
  SmoothVisible = true
  Source = -> [Cut002]
  Type = 3
  X = 106.615
  XDirection = (1,0,0)
  Y = 0
FEATURE [TechDraw::DrawProjGroup] ProjGroup
  Anchor = -> ProjItem
  AutoDistribute = false
  LockPosition = false
  ProjectionType = 0
  Rotation = 0
  ScaleType = 0
  Source = -> [Cut002]
  Views = -> [ProjItem,ProjItem001,ProjItem002]
  X = 122.402
  Y = 132.382
  spacingX = 5
  spacingY = 0
FEATURE [TechDraw::DrawViewDimension] Dimension
  AngleOverride = false
  Arbitrary = false
  ArbitraryTolerances = false
  EqualTolerance = true
  ExtensionAngle = 0
  FormatSpec = %.2w
  FormatSpecOverTolerance = %+.2w
  FormatSpecUnderTolerance = %+.2w
  Inverted = false
  LineAngle = 0
  LockPosition = false
  MeasureType = 1
  OverTolerance = 0
  References2D = -> [ProjItem001]
  Rotation = 0
  ScaleType = 0
  TheoreticalExact = false
  Type = 0
  UnderTolerance = 0
  X = 0.981859
  Y = 56.666
FEATURE [TechDraw::DrawViewDimension] Dimension001
  AngleOverride = false
  Arbitrary = false
  ArbitraryTolerances = false
  EqualTolerance = true
  ExtensionAngle = 0
  FormatSpec = %.2w
  FormatSpecOverTolerance = %+.2w
  FormatSpecUnderTolerance = %+.2w
  Inverted = false
  LineAngle = 0
  LockPosition = false
  MeasureType = 1
  OverTolerance = 0
  References2D = -> [ProjItem001]
  Rotation = 0
  ScaleType = 0
  TheoreticalExact = false
  Type = 0
  UnderTolerance = 0
  X = -7.37827
  Y = 63.3396
FEATURE [TechDraw::DrawViewDimension] Dimension002
  AngleOverride = false
  Arbitrary = false
  ArbitraryTolerances = false
  EqualTolerance = true
  ExtensionAngle = 0
  FormatSpec = ⌀%.2w
  FormatSpecOverTolerance = %+.2w
  FormatSpecUnderTolerance = %+.2w
  Inverted = false
  LineAngle = 0
  LockPosition = false
  MeasureType = 1
  OverTolerance = 0
  References2D = -> [ProjItem]
  Rotation = 0
  ScaleType = 0
  TheoreticalExact = false
  Type = 5
  UnderTolerance = 0
  X = -30.7018
  Y = 44.8387
FEATURE [TechDraw::DrawViewDimension] Dimension003
  AngleOverride = false
  Arbitrary = false
  ArbitraryTolerances = false
  EqualTolerance = true
  ExtensionAngle = 0
  FormatSpec = ⌀%.2w
  FormatSpecOverTolerance = %+.2w
  FormatSpecUnderTolerance = %+.2w
  Inverted = false
  LineAngle = 0
  LockPosition = false
  MeasureType = 1
  OverTolerance = 0
  References2D = -> [ProjItem]
  Rotation = 0
  ScaleType = 0
  TheoreticalExact = false
  Type = 5
  UnderTolerance = 0
  X = -10.7169
  Y = 58.1384
FEATURE [TechDraw::DrawViewDimension] Dimension004
  AngleOverride = false
  Arbitrary = false
  ArbitraryTolerances = false
  EqualTolerance = true
  ExtensionAngle = 0
  FormatSpec = %.2w
  FormatSpecOverTolerance = %+.2w
  FormatSpecUnderTolerance = %+.2w
  Inverted = false
  LineAngle = 0
  LockPosition = false
  MeasureType = 1
  OverTolerance = 0
  References2D = -> [ProjItem]
  Rotation = 0
  ScaleType = 0
  TheoreticalExact = false
  Type = 0
  UnderTolerance = 0
  X = -60.8736
  Y = 12.5448
FEATURE [TechDraw::DrawViewDimension] Dimension005
  AngleOverride = false
  Arbitrary = true
  ArbitraryTolerances = false
  EqualTolerance = true
  ExtensionAngle = 0
  FormatSpec = M6 threading
  FormatSpecOverTolerance = %+.2w
  FormatSpecUnderTolerance = %+.2w
  Inverted = false
  LineAngle = 0
  LockPosition = false
  MeasureType = 1
  OverTolerance = 0
  References2D = -> [ProjItem]
  Rotation = 0
  ScaleType = 0
  TheoreticalExact = false
  Type = 5
  UnderTolerance = 0
  X = -51.9281
  Y = -31.9474
FEATURE [TechDraw::DrawViewDimension] Dimension006
  AngleOverride = false
  Arbitrary = false
  ArbitraryTolerances = false
  EqualTolerance = true
  ExtensionAngle = 0
  FormatSpec = ⌀%.2w
  FormatSpecOverTolerance = %+.2w
  FormatSpecUnderTolerance = %+.2w
  Inverted = false
  LineAngle = 0
  LockPosition = false
  MeasureType = 1
  OverTolerance = 0
  References2D = -> [ProjItem]
  Rotation = 0
  ScaleType = 0
  TheoreticalExact = false
  Type = 5
  UnderTolerance = 0
  X = 5.01616
  Y = 9.12566
FEATURE [TechDraw::DrawViewDimension] Dimension007
  AngleOverride = false
  Arbitrary = false
  ArbitraryTolerances = false
  EqualTolerance = true
  ExtensionAngle = 0
  FormatSpec = ⌀%.2w
  FormatSpecOverTolerance = %+.2w
  FormatSpecUnderTolerance = %+.2w
  Inverted = false
  LineAngle = 0
  LockPosition = false
  MeasureType = 1
  OverTolerance = 0
  References2D = -> [ProjItem]
  Rotation = 0
  ScaleType = 0
  TheoreticalExact = false
  Type = 5
  UnderTolerance = 0
  X = 27.8015
  Y = 48.0484
FEATURE [TechDraw::DrawViewDimension] Dimension008
  AngleOverride = false
  Arbitrary = false
  ArbitraryTolerances = false
  EqualTolerance = true
  ExtensionAngle = 0
  FormatSpec = ⌀%.2w
  FormatSpecOverTolerance = %+.2w
  FormatSpecUnderTolerance = %+.2w
  Inverted = false
  LineAngle = 0
  LockPosition = false
  MeasureType = 1
  OverTolerance = 0
  References2D = -> [ProjItem002]
  Rotation = 0
  ScaleType = 0
  TheoreticalExact = false
  Type = 5
  UnderTolerance = 0
  X = -3.66037
  Y = 57.8453
FEATURE [TechDraw::DrawViewDimension] Dimension009
  AngleOverride = false
  Arbitrary = false
  ArbitraryTolerances = false
  EqualTolerance = true
  ExtensionAngle = 0
  FormatSpec = ⌀%.2w
  FormatSpecOverTolerance = %+.2w
  FormatSpecUnderTolerance = %+.2w
  Inverted = false
  LineAngle = 0
  LockPosition = false
  MeasureType = 1
  OverTolerance = 0
  References2D = -> [ProjItem002]
  Rotation = 0
  ScaleType = 0
  TheoreticalExact = false
  Type = 5
  UnderTolerance = 0
  X = 2.71226
  Y = 55.6152
FEATURE [TechDraw::DrawViewDimension] Dimension010
  AngleOverride = false
  Arbitrary = false
  ArbitraryTolerances = false
  EqualTolerance = true
  ExtensionAngle = 0
  FormatSpec = ⌀%.2w
  FormatSpecOverTolerance = %+.2w
  FormatSpecUnderTolerance = %+.2w
  Inverted = false
  LineAngle = 0
  LockPosition = false
  MeasureType = 1
  OverTolerance = 0
  References2D = -> [ProjItem002]
  Rotation = 0
  ScaleType = 0
  TheoreticalExact = false
  Type = 5
  UnderTolerance = 0
  X = 10.9613
  Y = 55.6046
FEATURE [TechDraw::DrawViewDimension] Dimension011
  AngleOverride = false
  Arbitrary = false
  ArbitraryTolerances = false
  EqualTolerance = true
  ExtensionAngle = 0
  FormatSpec = ⌀%.2w
  FormatSpecOverTolerance = %+.2w
  FormatSpecUnderTolerance = %+.2w
  Inverted = false
  LineAngle = 0
  LockPosition = false
  MeasureType = 1
  OverTolerance = 0
  References2D = -> [ProjItem002]
  Rotation = 0
  ScaleType = 0
  TheoreticalExact = false
  Type = 5
  UnderTolerance = 0
  X = 20.355
  Y = 54.1691
FEATURE [TechDraw::DrawViewDimension] Dimension012
  AngleOverride = false
  Arbitrary = false
  ArbitraryTolerances = false
  EqualTolerance = true
  ExtensionAngle = 0
  FormatSpec = %.2w
  FormatSpecOverTolerance = %+.2w
  FormatSpecUnderTolerance = %+.2w
  Inverted = false
  LineAngle = 0
  LockPosition = false
  MeasureType = 1
  OverTolerance = 0
  References2D = -> [ProjItem]
  Rotation = 0
  ScaleType = 0
  TheoreticalExact = false
  Type = 0
  UnderTolerance = 0
  X = 80.5725
  Y = 4.77787
FEATURE [TechDraw::DrawViewDimension] Dimension013
  AngleOverride = false
  Arbitrary = false
  ArbitraryTolerances = false
  EqualTolerance = true
  ExtensionAngle = 0
  FormatSpec = R%.2w
  FormatSpecOverTolerance = %+.2w
  FormatSpecUnderTolerance = %+.2w
  Inverted = false
  LineAngle = 0
  LockPosition = false
  MeasureType = 1
  OverTolerance = 0
  References2D = -> [ProjItem]
  Rotation = 0
  ScaleType = 0
  TheoreticalExact = false
  Type = 4
  UnderTolerance = 0
  X = 8.24155
  Y = 57.3473
FEATURE [TechDraw::DrawViewDimension] Dimension014
  AngleOverride = false
  Arbitrary = false
  ArbitraryTolerances = false
  EqualTolerance = true
  ExtensionAngle = 0
  FormatSpec = R%.2w
  FormatSpecOverTolerance = %+.2w
  FormatSpecUnderTolerance = %+.2w
  Inverted = false
  LineAngle = 0
  LockPosition = false
  MeasureType = 1
  OverTolerance = 0
  References2D = -> [ProjItem002]
  Rotation = 0
  ScaleType = 0
  TheoreticalExact = false
  Type = 4
  UnderTolerance = 0
  X = 33.6299
  Y = 47.4253
FEATURE [TechDraw::DrawViewDimension] Dimension015
  AngleOverride = false
  Arbitrary = false
  ArbitraryTolerances = false
  EqualTolerance = true
  ExtensionAngle = 0
  FormatSpec = %.2w
  FormatSpecOverTolerance = %+.2w
  FormatSpecUnderTolerance = %+.2w
  Inverted = false
  LineAngle = 0
  LockPosition = false
  MeasureType = 1
  OverTolerance = 0
  References2D = -> [ProjItem]
  Rotation = 0
  ScaleType = 0
  TheoreticalExact = false
  Type = 6
  UnderTolerance = 0
  X = 49.8347
  Y = 0.653999
FEATURE [TechDraw::DrawViewDimension] Dimension016
  AngleOverride = false
  Arbitrary = false
  ArbitraryTolerances = false
  EqualTolerance = true
  ExtensionAngle = 0
  FormatSpec = %.2w
  FormatSpecOverTolerance = %+.2w
  FormatSpecUnderTolerance = %+.2w
  Inverted = false
  LineAngle = 0
  LockPosition = false
  MeasureType = 1
  OverTolerance = 0
  References2D = -> [ProjItem002]
  Rotation = 0
  ScaleType = 0
  TheoreticalExact = false
  Type = 6
  UnderTolerance = 0
  X = -6.5506
  Y = -20.9661
FEATURE [TechDraw::DrawPage] Page
  KeepUpdated = true
  NextBalloonIndex = 1
  ProjectionType = 0
  Template = -> Template
  Views = -> [ProjGroup,Dimension,Dimension001,Dimension002,Dimension003,Dimension004,Dimension005,Dimension006,Dimension007,Dimension008,Dimension009,Dimension010,Dimension011,Dimension012,Dimension013,Dimension014,Dimension015,Dimension016]
FEATURE [TechDraw::DrawSVGTemplate] Template001
  EditableTexts = Designed_by_Name=Thomas Spielauer; FC-Date=2023-06-20; FC-SC=mm; FC-SH=02/03; FC-Title=Philipps XL30 compatible; Subtitle=Flange to CF35/CF40 ZLA
  Height = 210
  Orientation = 1
  Width = 297
FEATURE [TechDraw::DrawViewPart] View
  CoarseView = false
  Direction = (0,0,1)
  Focus = 100
  HardHidden = false
  IsoCount = 0
  IsoHidden = false
  IsoVisible = false
  LockPosition = false
  Perspective = false
  Rotation = 0
  ScaleType = 0
  SeamHidden = false
  SeamVisible = true
  SmoothHidden = false
  SmoothVisible = true
  Source = -> [Cut002]
  X = 62.9312
  XDirection = (-1,0,0)
  Y = 144.932
FEATURE [TechDraw::DrawViewSection] SectionView  label="Section  - "
  BaseView = -> View
  CoarseView = false
  CutSurfaceDisplay = 2
  Direction = (1,0,0)
  FileGeomPattern = <path>
  FileHatchPattern = <path>
  Focus = 100
  FuseBeforeCut = false
  HardHidden = false
  HatchScale = 1
  IsoCount = 0
  IsoHidden = false
  IsoVisible = false
  LockPosition = false
  NameGeomPattern = Diamond
  Perspective = false
  Rotation = 0
  Scale = 1.3
  ScaleType = 2
  SeamHidden = false
  SeamVisible = true
  SectionDirection = 0
  SectionNormal = (1,0,0)
  SectionOrigin = (0,0,8.65)
  SmoothHidden = false
  SmoothVisible = true
  Source = -> [Cut002]
  X = 173.121
  XDirection = (0,0,1)
  Y = 139.77
FEATURE [TechDraw::DrawViewDimension] Dimension017
  AngleOverride = false
  Arbitrary = false
  ArbitraryTolerances = false
  EqualTolerance = true
  ExtensionAngle = 0
  FormatSpec = %.2w
  FormatSpecOverTolerance = %+.2w
  FormatSpecUnderTolerance = %+.2w
  Inverted = false
  LineAngle = 0
  LockPosition = false
  MeasureType = 1
  OverTolerance = 0
  References2D = -> [SectionView]
  Rotation = 0
  ScaleType = 0
  TheoreticalExact = false
  Type = 0
  UnderTolerance = 0
  X = -26.2186
  Y = 2.66861
FEATURE [TechDraw::DrawViewDimension] Dimension018
  AngleOverride = false
  Arbitrary = false
  ArbitraryTolerances = false
  EqualTolerance = true
  ExtensionAngle = 0
  FormatSpec = %.2w
  FormatSpecOverTolerance = %+.2w
  FormatSpecUnderTolerance = %+.2w
  Inverted = false
  LineAngle = 0
  LockPosition = false
  MeasureType = 1
  OverTolerance = 0
  References2D = -> [SectionView]
  Rotation = 0
  ScaleType = 0
  TheoreticalExact = false
  Type = 0
  UnderTolerance = 0
  X = -26.0803
  Y = 37.3692
FEATURE [TechDraw::DrawViewDimension] Dimension019
  AngleOverride = false
  Arbitrary = false
  ArbitraryTolerances = false
  EqualTolerance = true
  ExtensionAngle = 0
  FormatSpec = %.2w
  FormatSpecOverTolerance = %+.2w
  FormatSpecUnderTolerance = %+.2w
  Inverted = false
  LineAngle = 0
  LockPosition = false
  MeasureType = 1
  OverTolerance = 0
  References2D = -> [SectionView]
  Rotation = 0
  ScaleType = 0
  TheoreticalExact = false
  Type = 0
  UnderTolerance = 0
  X = -42.6925
  Y = 43.2029
FEATURE [TechDraw::DrawViewDimension] Dimension020
  AngleOverride = false
  Arbitrary = false
  ArbitraryTolerances = false
  EqualTolerance = true
  ExtensionAngle = 0
  FormatSpec = %.2w (M6 threading)
  FormatSpecOverTolerance = %+.2w
  FormatSpecUnderTolerance = %+.2w
  Inverted = false
  LineAngle = 0
  LockPosition = false
  MeasureType = 1
  OverTolerance = 0
  References2D = -> [SectionView]
  Rotation = 0
  ScaleType = 0
  TheoreticalExact = false
  Type = 0
  UnderTolerance = 0
  X = 65.4737
  Y = 34.128
FEATURE [TechDraw::DrawViewDimension] Dimension021
  AngleOverride = false
  Arbitrary = false
  ArbitraryTolerances = false
  EqualTolerance = true
  ExtensionAngle = 0
  FormatSpec = %.2w (CF40 flange)
  FormatSpecOverTolerance = %+.2w
  FormatSpecUnderTolerance = %+.2w
  Inverted = false
  LineAngle = 0
  LockPosition = false
  MeasureType = 1
  OverTolerance = 0
  References2D = -> [SectionView]
  Rotation = 0
  ScaleType = 0
  TheoreticalExact = false
  Type = 0
  UnderTolerance = 0
  X = 42.1175
  Y = 2.08838
FEATURE [TechDraw::DrawViewDimension] Dimension022
  AngleOverride = false
  Arbitrary = false
  ArbitraryTolerances = false
  EqualTolerance = true
  ExtensionAngle = 0
  FormatSpec = %.2w (CF40 knife)
  FormatSpecOverTolerance = %+.2w
  FormatSpecUnderTolerance = %+.2w
  Inverted = false
  LineAngle = 0
  LockPosition = false
  MeasureType = 1
  OverTolerance = 0
  References2D = -> [SectionView]
  Rotation = 0
  ScaleType = 0
  TheoreticalExact = false
  Type = 0
  UnderTolerance = 0
  X = 34.7995
  Y = 2.25667
FEATURE [TechDraw::DrawViewDimension] Dimension023
  AngleOverride = false
  Arbitrary = false
  ArbitraryTolerances = false
  EqualTolerance = true
  ExtensionAngle = 0
  FormatSpec = %.2w
  FormatSpecOverTolerance = %+.2w
  FormatSpecUnderTolerance = %+.2w
  Inverted = false
  LineAngle = 0
  LockPosition = false
  MeasureType = 1
  OverTolerance = 0
  References2D = -> [SectionView]
  Rotation = 0
  ScaleType = 0
  TheoreticalExact = false
  Type = 0
  UnderTolerance = 0
  X = -4.13131
  Y = -67.649
FEATURE [TechDraw::DrawViewDimension] Dimension024
  AngleOverride = false
  Arbitrary = false
  ArbitraryTolerances = false
  EqualTolerance = true
  ExtensionAngle = 0
  FormatSpec = %.2w
  FormatSpecOverTolerance = %+.2w
  FormatSpecUnderTolerance = %+.2w
  Inverted = false
  LineAngle = 0
  LockPosition = false
  MeasureType = 1
  OverTolerance = 0
  References2D = -> [SectionView]
  Rotation = 0
  ScaleType = 0
  TheoreticalExact = false
  Type = 0
  UnderTolerance = 0
  X = 7.2924
  Y = -67.7595
FEATURE [TechDraw::DrawViewDimension] Dimension025
  AngleOverride = false
  Arbitrary = false
  ArbitraryTolerances = false
  EqualTolerance = true
  ExtensionAngle = 0
  FormatSpec = %.2w
  FormatSpecOverTolerance = %+.2w
  FormatSpecUnderTolerance = %+.2w
  Inverted = false
  LineAngle = 0
  LockPosition = false
  MeasureType = 1
  OverTolerance = 0
  References2D = -> [SectionView]
  Rotation = 0
  ScaleType = 0
  TheoreticalExact = false
  Type = 0
  UnderTolerance = 0
  X = -49.1232
  Y = 25.0368
FEATURE [TechDraw::DrawViewDimension] Dimension026
  AngleOverride = false
  Arbitrary = false
  ArbitraryTolerances = false
  EqualTolerance = true
  ExtensionAngle = 0
  FormatSpec = %.2w
  FormatSpecOverTolerance = %+.2w
  FormatSpecUnderTolerance = %+.2w
  Inverted = false
  LineAngle = 0
  LockPosition = false
  MeasureType = 1
  OverTolerance = 0
  References2D = -> [SectionView]
  Rotation = 0
  ScaleType = 0
  TheoreticalExact = false
  Type = 0
  UnderTolerance = 0
  X = 27.027
  Y = 51.676
FEATURE [TechDraw::DrawSVGTemplate] Template002
  EditableTexts = Designed_by_Name=Thomas Spielauer; FC-Date=2023-06-20; FC-SC=mm; FC-SH=03/03; FC-Title=Philipps XL30 compatible; Subtitle=Flange to CF35/CF40 ZLA
  Height = 210
  Orientation = 1
  Width = 297
FEATURE [TechDraw::DrawProjGroupItem] ProjItem003  label="Front001"
  CoarseView = false
  Direction = (0,0,1)
  Focus = 100
  HardHidden = false
  IsoCount = 0
  IsoHidden = false
  IsoVisible = false
  LockPosition = true
  Perspective = false
  Rotation = 0
  RotationVector = (-1,0,0)
  ScaleType = 2
  SeamHidden = false
  SeamVisible = true
  SmoothHidden = false
  SmoothVisible = true
  Source = -> [Cut002]
  Type = 0
  X = 0
  XDirection = (2e-16,1,0)
  Y = 0
FEATURE [TechDraw::DrawProjGroup] ProjGroup001
  Anchor = -> ProjItem003
  AutoDistribute = true
  LockPosition = false
  ProjectionType = 0
  Rotation = 0
  ScaleType = 0
  Source = -> [Cut002]
  Views = -> [ProjItem003]
  X = 61.3256
  Y = 143.774
  spacingX = 15
  spacingY = 15
FEATURE [TechDraw::DrawViewSection] SectionView001  label="Section  - 001"
  BaseView = -> ProjItem003
  CoarseView = false
  CutSurfaceDisplay = 2
  Direction = (-2e-16,-1,0)
  FileGeomPattern = <path>
  FileHatchPattern = <path>
  Focus = 100
  FuseBeforeCut = false
  HardHidden = false
  HatchScale = 1
  IsoCount = 0
  IsoHidden = false
  IsoVisible = false
  LockPosition = false
  NameGeomPattern = Diamond
  Perspective = false
  Rotation = 0
  Scale = 1.5
  ScaleType = 2
  SeamHidden = false
  SeamVisible = true
  SectionDirection = 0
  SectionNormal = (-2e-16,-1,0)
  SectionOrigin = (0,0,8.63)
  SmoothHidden = false
  SmoothVisible = true
  Source = -> [Cut002]
  X = 169.536
  XDirection = (0,0,1)
  Y = 132.453
FEATURE [TechDraw::DrawViewDimension] Dimension027
  AngleOverride = false
  Arbitrary = false
  ArbitraryTolerances = false
  EqualTolerance = true
  ExtensionAngle = 0
  FormatSpec = %.2w
  FormatSpecOverTolerance = %+.2w
  FormatSpecUnderTolerance = %+.2w
  Inverted = false
  LineAngle = 0
  LockPosition = false
  MeasureType = 1
  OverTolerance = 0
  References2D = -> [SectionView001]
  Rotation = 0
  ScaleType = 0
  TheoreticalExact = false
  Type = 0
  UnderTolerance = 0
  X = -24.7243
  Y = -55.0396
FEATURE [TechDraw::DrawViewDimension] Dimension028
  AngleOverride = false
  Arbitrary = false
  ArbitraryTolerances = false
  EqualTolerance = true
  ExtensionAngle = 0
  FormatSpec = %.2w
  FormatSpecOverTolerance = %+.2w
  FormatSpecUnderTolerance = %+.2w
  Inverted = false
  LineAngle = 0
  LockPosition = false
  MeasureType = 1
  OverTolerance = 0
  References2D = -> [SectionView001]
  Rotation = 0
  ScaleType = 0
  TheoreticalExact = false
  Type = 0
  UnderTolerance = 0
  X = 29.6201
  Y = -52.8459
FEATURE [TechDraw::DrawViewDimension] Dimension029
  AngleOverride = false
  Arbitrary = false
  ArbitraryTolerances = false
  EqualTolerance = true
  ExtensionAngle = 0
  FormatSpec = %.2w
  FormatSpecOverTolerance = %+.2w
  FormatSpecUnderTolerance = %+.2w
  Inverted = false
  LineAngle = 0
  LockPosition = false
  MeasureType = 1
  OverTolerance = 0
  References2D = -> [SectionView001]
  Rotation = 0
  ScaleType = 0
  TheoreticalExact = false
  Type = 0
  UnderTolerance = 0
  X = 4.53358
  Y = -15.8738
FEATURE [TechDraw::DrawViewDimension] Dimension030
  AngleOverride = false
  Arbitrary = false
  ArbitraryTolerances = false
  EqualTolerance = true
  ExtensionAngle = 0
  FormatSpec = %.2w
  FormatSpecOverTolerance = %+.2w
  FormatSpecUnderTolerance = %+.2w
  Inverted = false
  LineAngle = 0
  LockPosition = false
  MeasureType = 1
  OverTolerance = 0
  References2D = -> [SectionView001]
  Rotation = 0
  ScaleType = 0
  TheoreticalExact = false
  Type = 0
  UnderTolerance = 0
  X = -8.01157
  Y = -15.7909
FEATURE [TechDraw::DrawViewDimension] Dimension031
  AngleOverride = false
  Arbitrary = false
  ArbitraryTolerances = false
  EqualTolerance = true
  ExtensionAngle = 0
  FormatSpec = %.2w
  FormatSpecOverTolerance = %+.2w
  FormatSpecUnderTolerance = %+.2w
  Inverted = false
  LineAngle = 0
  LockPosition = false
  MeasureType = 1
  OverTolerance = 0
  References2D = -> [SectionView]
  Rotation = 0
  ScaleType = 0
  TheoreticalExact = false
  Type = 0
  UnderTolerance = 0
  X = 20.3938
  Y = -35.4781
FEATURE [TechDraw::DrawViewDimension] Dimension032
  AngleOverride = false
  Arbitrary = false
  ArbitraryTolerances = false
  EqualTolerance = true
  ExtensionAngle = 0
  FormatSpec = %.2w (CF40)
  FormatSpecOverTolerance = %+.2w
  FormatSpecUnderTolerance = %+.2w
  Inverted = false
  LineAngle = 0
  LockPosition = false
  MeasureType = 1
  OverTolerance = 0
  References2D = -> [SectionView]
  Rotation = 0
  ScaleType = 0
  TheoreticalExact = false
  Type = 0
  UnderTolerance = 0
  X = 23.9168
  Y = 25.5384
FEATURE [TechDraw::DrawPage] Page001
  KeepUpdated = true
  NextBalloonIndex = 1
  ProjectionType = 0
  Template = -> Template001
  Views = -> [View,SectionView,Dimension017,Dimension018,Dimension019,Dimension020,Dimension021,Dimension022,Dimension023,Dimension024,Dimension025,Dimension026,Dimension031,Dimension032]
FEATURE [TechDraw::DrawViewDimension] Dimension033
  AngleOverride = false
  Arbitrary = false
  ArbitraryTolerances = false
  EqualTolerance = true
  ExtensionAngle = 0
  FormatSpec = %.2w
  FormatSpecOverTolerance = %+.2w
  FormatSpecUnderTolerance = %+.2w
  Inverted = false
  LineAngle = 0
  LockPosition = false
  MeasureType = 1
  OverTolerance = 0
  References2D = -> [SectionView001]
  Rotation = 0
  ScaleType = 0
  TheoreticalExact = false
  Type = 0
  UnderTolerance = 0
  X = -3.975
  Y = 24.6619
FEATURE [TechDraw::DrawPage] Page002
  KeepUpdated = true
  NextBalloonIndex = 1
  ProjectionType = 0
  Template = -> Template002
  Views = -> [ProjGroup001,SectionView001,Dimension027,Dimension028,Dimension029,Dimension030,Dimension033]
note: 4 file-system paths scrubbed to <path> (originals preserved in the JSON sidecar)
---- part Quak_XL30_Modulator2.FCStd = doc fcstd_923a75bff728 (100987 chars; too large to inline — full recipe in that document) ----
---- part XL30ColumnAttachmentRing01.FCStd = doc fcstd_73339c15c85f ----
FCSTD DOCUMENT  (FreeCAD 0.20R)
Label: XL30ColumnAttachmentRing01
License: All rights reserved
LicenseURL: http://en.wikipedia.org/wiki/All_rights_reserved
objects: Part::Cylinder×34, TechDraw::DrawViewDimension×19, Part::Compound×18, Part::MultiFuse×17, Part::Cut×11, Part::Box×8, Part::FeaturePython×8, TechDraw::DrawProjGroupItem×2, Spreadsheet::Sheet×1, TechDraw::DrawSVGTemplate×1, TechDraw::DrawProjGroup×1, TechDraw::DrawViewSection×1, TechDraw::DrawViewAnnotation×1, TechDraw::DrawPage×1
note: 96 computed .brp shape members not serialized (recipe doc carries the construction recipe); baked Part::Feature solids carry a one-line shape summary decoded from their .brp

FEATURE [Spreadsheet::Sheet] Spreadsheet  label="AttachmentRing01"
  cells = A1=Ring configuration; A2=Inside diameter; B2(ring_id)=100; C2=Inside diameter of the column / poleshoe; E2=Ring width; F2(ring_width)==ring_od - ring_id; A3=Outside diameter; B3(ring_od)==100 + 2 * 7.66; C3=Outside diameter; A4=Thickness; B4(ring_thickness)=5; C4=Thickness of the mounting rin; A5=Thickness below mountscrew; B5(thickness_m3_below)=2
FEATURE [Part::Cylinder] Cylinder
  Angle = 360
  AttacherType = Attacher::AttachEngine3D
  FirstAngle = 0
  Height = 5
  Radius = 57.66
  SecondAngle = 0
  expr: Height = <<AttachmentRing01>>.ring_thickness
  expr: Radius = <<AttachmentRing01>>.ring_od / 2
FEATURE [Part::Cylinder] Cylinder001
  Angle = 360
  AttacherType = Attacher::AttachEngine3D
  FirstAngle = 0
  Height = 5
  Radius = 50
  SecondAngle = 0
  expr: Height = <<AttachmentRing01>>.ring_thickness
  expr: Radius = <<AttachmentRing01>>.ring_id / 2
FEATURE [Part::Cut] Cut
  Base = -> Cylinder
  Tool = -> Cylinder001
FEATURE [Part::Box] Box007  label="Cube007"
  AttacherType = Attacher::AttachEngine3D
  Height = 5
  Length = 4
  Placement = pos=(47.5,-4,0) rot=(0,0,1;0rad)
  Width = 8
  expr: Height = <<AttachmentRing01>>.ring_thickness
FEATURE [Part::Cylinder] Cylinder009
  Angle = 360
  AttacherType = Attacher::AttachEngine3D
  FirstAngle = 0
  Height = 5
  Placement = pos=(47.5,0,0) rot=(0,0,1;0rad)
  Radius = 4
  SecondAngle = 0
  expr: Height = <<AttachmentRing01>>.ring_thickness
FEATURE [Part::MultiFuse] Fusion008
  Shapes = -> [Cylinder009,Box007]
FEATURE [Part::Cylinder] Cylinder011
  Angle = 360
  AttacherType = Attacher::AttachEngine3D
  FirstAngle = 0
  Height = 10
  Placement = pos=(47.5,0,0) rot=(0,0,1;0rad)
  Radius = 1.8
  SecondAngle = 0
FEATURE [Part::Cylinder] Cylinder012
  Angle = 360
  AttacherType = Attacher::AttachEngine3D
  FirstAngle = 0
  Height = 3
  Placement = pos=(47.5,0,0) rot=(0,0,1;0rad)
  Radius = 2.84
  SecondAngle = 0
  expr: Height = <<AttachmentRing01>>.ring_thickness - <<AttachmentRing01>>.thickness_m3_below
FEATURE [Part::MultiFuse] Fusion
  Shapes = -> [Cylinder012,Cylinder011]
FEATURE [Part::Cut] Cut001
  Base = -> Fusion008
  Tool = -> Fusion
FEATURE [Part::Box] Box008  label="Cube008"
  AttacherType = Attacher::AttachEngine3D
  Height = 5
  Length = 4
  Placement = pos=(47.5,-4,0) rot=(0,0,1;0rad)
  Width = 8
  expr: Height = <<AttachmentRing01>>.ring_thickness
FEATURE [Part::Cylinder] Cylinder013
  Angle = 360
  AttacherType = Attacher::AttachEngine3D
  FirstAngle = 0
  Height = 5
  Placement = pos=(47.5,0,0) rot=(0,0,1;0rad)
  Radius = 4
  SecondAngle = 0
  expr: Height = <<AttachmentRing01>>.ring_thickness
FEATURE [Part::Cylinder] Cylinder014
  Angle = 360
  AttacherType = Attacher::AttachEngine3D
  FirstAngle = 0
  Height = 10
  Placement = pos=(47.5,0,0) rot=(0,0,1;0rad)
  Radius = 1.8
  SecondAngle = 0
FEATURE [Part::Cylinder] Cylinder015
  Angle = 360
  AttacherType = Attacher::AttachEngine3D
  FirstAngle = 0
  Height = 3
  Placement = pos=(47.5,0,0) rot=(0,0,1;0rad)
  Radius = 2.84
  SecondAngle = 0
  expr: Height = <<AttachmentRing01>>.ring_thickness - <<AttachmentRing01>>.thickness_m3_below
FEATURE [Part::MultiFuse] Fusion009
  Shapes = -> [Cylinder015,Cylinder014]
FEATURE [Part::MultiFuse] Fusion010
  Shapes = -> [Cylinder013,Box008]
FEATURE [Part::Cut] Cut002
  Base = -> Fusion010
  Placement = pos=(0,0,0) rot=(0,0,1;0.785398rad)
  Tool = -> Fusion009
FEATURE [Part::Box] Box009  label="Cube009"
  AttacherType = Attacher::AttachEngine3D
  Height = 5
  Length = 4
  Placement = pos=(47.5,-4,0) rot=(0,0,1;0rad)
  Width = 8
  expr: Height = <<AttachmentRing01>>.ring_thickness
FEATURE [Part::Cylinder] Cylinder016
  Angle = 360
  AttacherType = Attacher::AttachEngine3D
  FirstAngle = 0
  Height = 5
  Placement = pos=(47.5,0,0) rot=(0,0,1;0rad)
  Radius = 4
  SecondAngle = 0
  expr: Height = <<AttachmentRing01>>.ring_thickness
FEATURE [Part::Cylinder] Cylinder017
  Angle = 360
  AttacherType = Attacher::AttachEngine3D
  FirstAngle = 0
  Height = 10
  Placement = pos=(47.5,0,0) rot=(0,0,1;0rad)
  Radius = 1.8
  SecondAngle = 0
FEATURE [Part::Cylinder] Cylinder018
  Angle = 360
  AttacherType = Attacher::AttachEngine3D
  FirstAngle = 0
  Height = 3
  Placement = pos=(47.5,0,0) rot=(0,0,1;0rad)
  Radius = 2.84
  SecondAngle = 0
  expr: Height = <<AttachmentRing01>>.ring_thickness - <<AttachmentRing01>>.thickness_m3_below
FEATURE [Part::MultiFuse] Fusion011
  Shapes = -> [Cylinder018,Cylinder017]
FEATURE [Part::MultiFuse] Fusion012
  Shapes = -> [Cylinder016,Box009]
FEATURE [Part::Cut] Cut003
  Base = -> Fusion012
  Placement = pos=(0,0,0) rot=(0,0,1;1.5708rad)
  Tool = -> Fusion011
FEATURE [Part::Box] Box010  label="Cube010"
  AttacherType = Attacher::AttachEngine3D
  Height = 5
  Length = 4
  Placement = pos=(47.5,-4,0) rot=(0,0,1;0rad)
  Width = 8
  expr: Height = <<AttachmentRing01>>.ring_thickness
FEATURE [Part::Cylinder] Cylinder019
  Angle = 360
  AttacherType = Attacher::AttachEngine3D
  FirstAngle = 0
  Height = 5
  Placement = pos=(47.5,0,0) rot=(0,0,1;0rad)
  Radius = 4
  SecondAngle = 0
  expr: Height = <<AttachmentRing01>>.ring_thickness
FEATURE [Part::Cylinder] Cylinder020
  Angle = 360
  AttacherType = Attacher::AttachEngine3D
  FirstAngle = 0
  Height = 10
  Placement = pos=(47.5,0,0) rot=(0,0,1;0rad)
  Radius = 1.8
  SecondAngle = 0
FEATURE [Part::Cylinder] Cylinder021
  Angle = 360
  AttacherType = Attacher::AttachEngine3D
  FirstAngle = 0
  Height = 3
  Placement = pos=(47.5,0,0) rot=(0,0,1;0rad)
  Radius = 2.84
  SecondAngle = 0
  expr: Height = <<AttachmentRing01>>.ring_thickness - <<AttachmentRing01>>.thickness_m3_below
FEATURE [Part::MultiFuse] Fusion013
  Shapes = -> [Cylinder021,Cylinder020]
FEATURE [Part::MultiFuse] Fusion014
  Shapes = -> [Cylinder019,Box010]
FEATURE [Part::Cut] Cut004
  Base = -> Fusion014
  Placement = pos=(0,0,0) rot=(0,0,1;2.35619rad)
  Tool = -> Fusion013
FEATURE [Part::Box] Box011  label="Cube011"
  AttacherType = Attacher::AttachEngine3D
  Height = 5
  Length = 4
  Placement = pos=(47.5,-4,0) rot=(0,0,1;0rad)
  Width = 8
  expr: Height = <<AttachmentRing01>>.ring_thickness
FEATURE [Part::Cylinder] Cylinder022
  Angle = 360
  AttacherType = Attacher::AttachEngine3D
  FirstAngle = 0
  Height = 5
  Placement = pos=(47.5,0,0) rot=(0,0,1;0rad)
  Radius = 4
  SecondAngle = 0
  expr: Height = <<AttachmentRing01>>.ring_thickness
FEATURE [Part::Cylinder] Cylinder023
  Angle = 360
  AttacherType = Attacher::AttachEngine3D
  FirstAngle = 0
  Height = 10
  Placement = pos=(47.5,0,0) rot=(0,0,1;0rad)
  Radius = 1.8
  SecondAngle = 0
FEATURE [Part::Cylinder] Cylinder024
  Angle = 360
  AttacherType = Attacher::AttachEngine3D
  FirstAngle = 0
  Height = 3
  Placement = pos=(47.5,0,0) rot=(0,0,1;0rad)
  Radius = 2.84
  SecondAngle = 0
  expr: Height = <<AttachmentRing01>>.ring_thickness - <<AttachmentRing01>>.thickness_m3_below
FEATURE [Part::MultiFuse] Fusion015
  Shapes = -> [Cylinder024,Cylinder023]
FEATURE [Part::MultiFuse] Fusion016
  Shapes = -> [Cylinder022,Box011]
FEATURE [Part::Cut] Cut005
  Base = -> Fusion016
  Placement = pos=(0,0,0) rot=(0,0,1;3.14159rad)
  Tool = -> Fusion015
FEATURE [Part::Box] Box012  label="Cube012"
  AttacherType = Attacher::AttachEngine3D
  Height = 5
  Length = 4
  Placement = pos=(47.5,-4,0) rot=(0,0,1;0rad)
  Width = 8
  expr: Height = <<AttachmentRing01>>.ring_thickness
FEATURE [Part::Cylinder] Cylinder025
  Angle = 360
  AttacherType = Attacher::AttachEngine3D
  FirstAngle = 0
  Height = 5
  Placement = pos=(47.5,0,0) rot=(0,0,1;0rad)
  Radius = 4
  SecondAngle = 0
  expr: Height = <<AttachmentRing01>>.ring_thickness
FEATURE [Part::Cylinder] Cylinder026
  Angle = 360
  AttacherType = Attacher::AttachEngine3D
  FirstAngle = 0
  Height = 10
  Placement = pos=(47.5,0,0) rot=(0,0,1;0rad)
  Radius = 1.8
  SecondAngle = 0
FEATURE [Part::Cylinder] Cylinder027
  Angle = 360
  AttacherType = Attacher::AttachEngine3D
  FirstAngle = 0
  Height = 3
  Placement = pos=(47.5,0,0) rot=(0,0,1;0rad)
  Radius = 2.84
  SecondAngle = 0
  expr: Height = <<AttachmentRing01>>.ring_thickness - <<AttachmentRing01>>.thickness_m3_below
FEATURE [Part::MultiFuse] Fusion017
  Shapes = -> [Cylinder027,Cylinder026]
FEATURE [Part::MultiFuse] Fusion018
  Shapes = -> [Cylinder025,Box012]
FEATURE [Part::Cut] Cut006
  Base = -> Fusion018
  Placement = pos=(0,0,0) rot=(0,0,1;3.92699rad)
  Tool = -> Fusion017
FEATURE [Part::Box] Box013  label="Cube013"
  AttacherType = Attacher::AttachEngine3D
  Height = 5
  Length = 4
  Placement = pos=(47.5,-4,0) rot=(0,0,1;0rad)
  Width = 8
  expr: Height = <<AttachmentRing01>>.ring_thickness
FEATURE [Part::Cylinder] Cylinder028
  Angle = 360
  AttacherType = Attacher::AttachEngine3D
  FirstAngle = 0
  Height = 5
  Placement = pos=(47.5,0,0) rot=(0,0,1;0rad)
  Radius = 4
  SecondAngle = 0
  expr: Height = <<AttachmentRing01>>.ring_thickness
FEATURE [Part::Cylinder] Cylinder029
  Angle = 360
  AttacherType = Attacher::AttachEngine3D
  FirstAngle = 0
  Height = 10
  Placement = pos=(47.5,0,0) rot=(0,0,1;0rad)
  Radius = 1.8
  SecondAngle = 0
FEATURE [Part::Cylinder] Cylinder030
  Angle = 360
  AttacherType = Attacher::AttachEngine3D
  FirstAngle = 0
  Height = 3
  Placement = pos=(47.5,0,0) rot=(0,0,1;0rad)
  Radius = 2.84
  SecondAngle = 0
  expr: Height = <<AttachmentRing01>>.ring_thickness - <<AttachmentRing01>>.thickness_m3_below
FEATURE [Part::MultiFuse] Fusion019
  Shapes = -> [Cylinder030,Cylinder029]
FEATURE [Part::MultiFuse] Fusion020
  Shapes = -> [Cylinder028,Box013]
FEATURE [Part::Cut] Cut007
  Base = -> Fusion020
  Placement = pos=(0,0,0) rot=(0,0,1;4.71239rad)
  Tool = -> Fusion019
FEATURE [Part::Box] Box014  label="Cube014"
  AttacherType = Attacher::AttachEngine3D
  Height = 5
  Length = 4
  Placement = pos=(47.5,-4,0) rot=(0,0,1;0rad)
  Width = 8
  expr: Height = <<AttachmentRing01>>.ring_thickness
FEATURE [Part::Cylinder] Cylinder031
  Angle = 360
  AttacherType = Attacher::AttachEngine3D
  FirstAngle = 0
  Height = 5
  Placement = pos=(47.5,0,0) rot=(0,0,1;0rad)
  Radius = 4
  SecondAngle = 0
  expr: Height = <<AttachmentRing01>>.ring_thickness
FEATURE [Part::Cylinder] Cylinder032
  Angle = 360
  AttacherType = Attacher::AttachEngine3D
  FirstAngle = 0
  Height = 10
  Placement = pos=(47.5,0,0) rot=(0,0,1;0rad)
  Radius = 1.8
  SecondAngle = 0
FEATURE [Part::Cylinder] Cylinder033
  Angle = 360
  AttacherType = Attacher::AttachEngine3D
  FirstAngle = 0
  Height = 3
  Placement = pos=(47.5,0,0) rot=(0,0,1;0rad)
  Radius = 2.84
  SecondAngle = 0
  expr: Height = <<AttachmentRing01>>.ring_thickness - <<AttachmentRing01>>.thickness_m3_below
FEATURE [Part::MultiFuse] Fusion021
  Shapes = -> [Cylinder033,Cylinder032]
FEATURE [Part::MultiFuse] Fusion022
  Shapes = -> [Cylinder031,Box014]
FEATURE [Part::Cut] Cut008
  Base = -> Fusion022
  Placement = pos=(0,0,0) rot=(0,0,1;5.49779rad)
  Tool = -> Fusion021
FEATURE [Part::MultiFuse] Fusion023
  Shapes = -> [Cut,Cut001,Cut002,Cut003,Cut004,Cut005,Cut006,Cut007,Cut008]
FEATURE [Part::FeaturePython] Screw  label="M4x7-Screw001"  # Fasteners workbench fastener (typed FeaturePython)
  Placement = pos=(53.83,0,3.82) rot=(0,0,1;0rad)
  diameter = 5
  invert = false
  leftHanded = false
  length = 11
  lengthCustom = 7
  matchOuter = false
  offset = 0
  thread = false
  type = 48
  expr: .Placement.Base.x = (<<AttachmentRing01>>.ring_od + <<AttachmentRing01>>.ring_id) / 4
  expr: lengthCustom = <<AttachmentRing01>>.ring_thickness + 2
FEATURE [Part::Compound] Compound
  Links = -> [Screw]
  Placement = pos=(0,0,0) rot=(0,0,1;0.392699rad)
FEATURE [Part::FeaturePython] Screw001  label="M4x7-Screw002"  # Fasteners workbench fastener (typed FeaturePython)
  Placement = pos=(53.83,0,3.82) rot=(0,0,1;0rad)
  diameter = 5
  invert = false
  leftHanded = false
  length = 11
  lengthCustom = 7
  matchOuter = false
  offset = 0
  thread = false
  type = 48
  expr: .Placement.Base.x = (<<AttachmentRing01>>.ring_od + <<AttachmentRing01>>.ring_id) / 4
  expr: lengthCustom = <<AttachmentRing01>>.ring_thickness + 2
FEATURE [Part::Compound] Compound001
  Links = -> [Screw001]
  Placement = pos=(0,0,0) rot=(0,0,1;1.1781rad)
FEATURE [Part::FeaturePython] Screw002  label="M4x7-Screw003"  # Fasteners workbench fastener (typed FeaturePython)
  Placement = pos=(53.83,0,3.82) rot=(0,0,1;0rad)
  diameter = 5
  invert = false
  leftHanded = false
  length = 11
  lengthCustom = 7
  matchOuter = false
  offset = 0
  thread = false
  type = 48
  expr: .Placement.Base.x = (<<AttachmentRing01>>.ring_od + <<AttachmentRing01>>.ring_id) / 4
  expr: lengthCustom = <<AttachmentRing01>>.ring_thickness + 2
FEATURE [Part::Compound] Compound002
  Links = -> [Screw002]
  Placement = pos=(0,0,0) rot=(0,0,1;1.96349rad)
FEATURE [Part::FeaturePython] Screw003  label="M4x7-Screw004"  # Fasteners workbench fastener (typed FeaturePython)
  Placement = pos=(53.83,0,3.82) rot=(0,0,1;0rad)
  diameter = 5
  invert = false
  leftHanded = false
  length = 11
  lengthCustom = 7
  matchOuter = false
  offset = 0
  thread = false
  type = 48
  expr: .Placement.Base.x = (<<AttachmentRing01>>.ring_od + <<AttachmentRing01>>.ring_id) / 4
  expr: lengthCustom = <<AttachmentRing01>>.ring_thickness + 2
FEATURE [Part::Compound] Compound003
  Links = -> [Screw003]
  Placement = pos=(0,0,0) rot=(0,0,1;2.74889rad)
FEATURE [Part::FeaturePython] Screw004  label="M4x7-Screw005"  # Fasteners workbench fastener (typed FeaturePython)
  Placement = pos=(53.83,0,3.82) rot=(0,0,1;0rad)
  diameter = 5
  invert = false
  leftHanded = false
  length = 11
  lengthCustom = 7
  matchOuter = false
  offset = 0
  thread = false
  type = 48
  expr: .Placement.Base.x = (<<AttachmentRing01>>.ring_od + <<AttachmentRing01>>.ring_id) / 4
  expr: lengthCustom = <<AttachmentRing01>>.ring_thickness + 2
FEATURE [Part::Compound] Compound004
  Links = -> [Screw004]
  Placement = pos=(0,0,0) rot=(0,0,1;3.53429rad)
FEATURE [Part::FeaturePython] Screw005  label="M4x7-Screw006"  # Fasteners workbench fastener (typed FeaturePython)
  Placement = pos=(53.83,0,3.82) rot=(0,0,1;0rad)
  diameter = 5
  invert = false
  leftHanded = false
  length = 11
  lengthCustom = 7
  matchOuter = false
  offset = 0
  thread = false
  type = 48
  expr: .Placement.Base.x = (<<AttachmentRing01>>.ring_od + <<AttachmentRing01>>.ring_id) / 4
  expr: lengthCustom = <<AttachmentRing01>>.ring_thickness + 2
FEATURE [Part::Compound] Compound005
  Links = -> [Screw005]
  Placement = pos=(0,0,0) rot=(0,0,1;4.31969rad)
FEATURE [Part::FeaturePython] Screw006  label="M4x7-Screw007"  # Fasteners workbench fastener (typed FeaturePython)
  Placement = pos=(53.83,0,3.82) rot=(0,0,1;0rad)
  diameter = 5
  invert = false
  leftHanded = false
  length = 11
  lengthCustom = 7
  matchOuter = false
  offset = 0
  thread = false
  type = 48
  expr: .Placement.Base.x = (<<AttachmentRing01>>.ring_od + <<AttachmentRing01>>.ring_id) / 4
  expr: lengthCustom = <<AttachmentRing01>>.ring_thickness + 2
FEATURE [Part::Compound] Compound006
  Links = -> [Screw006]
  Placement = pos=(0,0,0) rot=(0,0,1;5.10509rad)
FEATURE [Part::FeaturePython] Screw007  label="M4x7-Screw"  # Fasteners workbench fastener (typed FeaturePython)
  Placement = pos=(53.83,0,3.82) rot=(0,0,1;0rad)
  diameter = 5
  invert = false
  leftHanded = false
  length = 11
  lengthCustom = 7
  matchOuter = false
  offset = 0
  thread = false
  type = 48
  expr: .Placement.Base.x = (<<AttachmentRing01>>.ring_od + <<AttachmentRing01>>.ring_id) / 4
  expr: lengthCustom = <<AttachmentRing01>>.ring_thickness + 2
FEATURE [Part::Compound] Compound007
  Links = -> [Screw007]
  Placement = pos=(0,0,0) rot=(0,0,1;5.89049rad)
FEATURE [Part::Compound] Compound008  label="M4Threadsx8"
  Links = -> [Compound007,Compound,Compound001,Compound002,Compound003,Compound004,Compound005,Compound006]
  Placement = pos=(0,0,2) rot=(0,0,1;0rad)
FEATURE [Part::Cut] Cut009
  Base = -> Fusion023
  Tool = -> Compound008
FEATURE [Part::Cylinder] Cylinder035
  Angle = 360
  AttacherType = Attacher::AttachEngine3D
  FirstAngle = 0
  Height = 5
  Placement = pos=(53.83,0,0) rot=(0,0,1;0rad)
  Radius = 2.5
  SecondAngle = 0
  expr: .Placement.Base.x = (<<AttachmentRing01>>.ring_od + <<AttachmentRing01>>.ring_id) / 4
  expr: Height = <<AttachmentRing01>>.ring_thickness
FEATURE [Part::Compound] Compound009
  Links = -> [Cylinder035]
FEATURE [Part::Cylinder] Cylinder036
  Angle = 360
  AttacherType = Attacher::AttachEngine3D
  FirstAngle = 0
  Height = 5
  Placement = pos=(53.83,0,0) rot=(0,0,1;0rad)
  Radius = 2.5
  SecondAngle = 0
  expr: .Placement.Base.x = (<<AttachmentRing01>>.ring_od + <<AttachmentRing01>>.ring_id) / 4
  expr: Height = <<AttachmentRing01>>.ring_thickness
FEATURE [Part::Compound] Compound010
  Links = -> [Cylinder036]
  Placement = pos=(0,0,0) rot=(0,0,1;0.785398rad)
FEATURE [Part::Cylinder] Cylinder037
  Angle = 360
  AttacherType = Attacher::AttachEngine3D
  FirstAngle = 0
  Height = 5
  Placement = pos=(53.83,0,0) rot=(0,0,1;0rad)
  Radius = 2.5
  SecondAngle = 0
  expr: .Placement.Base.x = (<<AttachmentRing01>>.ring_od + <<AttachmentRing01>>.ring_id) / 4
  expr: Height = <<AttachmentRing01>>.ring_thickness
FEATURE [Part::Compound] Compound011
  Links = -> [Cylinder037]
  Placement = pos=(0,0,0) rot=(0,0,1;1.5708rad)
FEATURE [Part::Cylinder] Cylinder038
  Angle = 360
  AttacherType = Attacher::AttachEngine3D
  FirstAngle = 0
  Height = 5
  Placement = pos=(53.83,0,0) rot=(0,0,1;0rad)
  Radius = 2.5
  SecondAngle = 0
  expr: .Placement.Base.x = (<<AttachmentRing01>>.ring_od + <<AttachmentRing01>>.ring_id) / 4
  expr: Height = <<AttachmentRing01>>.ring_thickness
FEATURE [Part::Compound] Compound012
  Links = -> [Cylinder038]
  Placement = pos=(0,0,0) rot=(0,0,1;2.35619rad)
FEATURE [Part::Cylinder] Cylinder039
  Angle = 360
  AttacherType = Attacher::AttachEngine3D
  FirstAngle = 0
  Height = 5
  Placement = pos=(53.83,0,0) rot=(0,0,1;0rad)
  Radius = 2.5
  SecondAngle = 0
  expr: .Placement.Base.x = (<<AttachmentRing01>>.ring_od + <<AttachmentRing01>>.ring_id) / 4
  expr: Height = <<AttachmentRing01>>.ring_thickness
FEATURE [Part::Compound] Compound013
  Links = -> [Cylinder039]
  Placement = pos=(0,0,0) rot=(0,0,1;3.14159rad)
FEATURE [Part::Cylinder] Cylinder040
  Angle = 360
  AttacherType = Attacher::AttachEngine3D
  FirstAngle = 0
  Height = 5
  Placement = pos=(53.83,0,0) rot=(0,0,1;0rad)
  Radius = 2.5
  SecondAngle = 0
  expr: .Placement.Base.x = (<<AttachmentRing01>>.ring_od + <<AttachmentRing01>>.ring_id) / 4
  expr: Height = <<AttachmentRing01>>.ring_thickness
FEATURE [Part::Compound] Compound014
  Links = -> [Cylinder040]
  Placement = pos=(0,0,0) rot=(0,0,1;3.92699rad)
FEATURE [Part::Cylinder] Cylinder041
  Angle = 360
  AttacherType = Attacher::AttachEngine3D
  FirstAngle = 0
  Height = 5
  Placement = pos=(53.83,0,0) rot=(0,0,1;0rad)
  Radius = 2.5
  SecondAngle = 0
  expr: .Placement.Base.x = (<<AttachmentRing01>>.ring_od + <<AttachmentRing01>>.ring_id) / 4
  expr: Height = <<AttachmentRing01>>.ring_thickness
FEATURE [Part::Compound] Compound015
  Links = -> [Cylinder041]
  Placement = pos=(0,0,0) rot=(0,0,1;4.71239rad)
FEATURE [Part::Cylinder] Cylinder042
  Angle = 360
  AttacherType = Attacher::AttachEngine3D
  FirstAngle = 0
  Height = 5
  Placement = pos=(53.83,0,0) rot=(0,0,1;0rad)
  Radius = 2.5
  SecondAngle = 0
  expr: .Placement.Base.x = (<<AttachmentRing01>>.ring_od + <<AttachmentRing01>>.ring_id) / 4
  expr: Height = <<AttachmentRing01>>.ring_thickness
FEATURE [Part::Compound] Compound016
  Links = -> [Cylinder042]
  Placement = pos=(0,0,0) rot=(0,0,1;5.49779rad)
FEATURE [Part::Compound] Compound017  label="LEDHoles"
  Links = -> [Compound016,Compound009,Compound010,Compound011,Compound012,Compound013,Compound014,Compound015]
FEATURE [Part::Cut] Cut010  label="AttachmentRing_Column01"
  Base = -> Cut009
  Tool = -> Compound017
FEATURE [TechDraw::DrawSVGTemplate] Template
  EditableTexts = Designed_by_Name=Thomas Spielauer; FC-Date=2023-11-15; FC-SC=mm; FC-SH=1/1; FC-Title=XL30 Column attachment ring; Subtitle=Compatible with XL30 ESEM
  Height = 210
  Orientation = 1
  Width = 297
FEATURE [TechDraw::DrawProjGroupItem] ProjItem  label="Front"
  CoarseView = false
  Direction = (0,0,1)
  Focus = 100
  HardHidden = false
  IsoCount = 0
  IsoHidden = false
  IsoVisible = false
  LockPosition = true
  Perspective = false
  Rotation = 0
  RotationVector = (-1,0,0)
  ScaleType = 2
  SeamHidden = false
  SeamVisible = true
  SmoothHidden = false
  SmoothVisible = true
  Source = -> [Cut010]
  Type = 0
  X = 0
  XDirection = (-1,0,0)
  Y = 0
FEATURE [TechDraw::DrawProjGroupItem] ProjItem001  label="Left"
  CoarseView = false
  Direction = (1,0,1e-16)
  Focus = 100
  HardHidden = false
  IsoCount = 0
  IsoHidden = false
  IsoVisible = false
  LockPosition = false
  Perspective = false
  Rotation = 0
  RotationVector = (1,0,0)
  ScaleType = 2
  SeamHidden = false
  SeamVisible = true
  SmoothHidden = false
  SmoothVisible = true
  Source = -> [Cut010]
  Type = 1
  X = 96.8512
  XDirection = (-1e-16,0,1)
  Y = 0
FEATURE [TechDraw::DrawProjGroup] ProjGroup
  Anchor = -> ProjItem
  AutoDistribute = true
  LockPosition = false
  ProjectionType = 0
  Rotation = 0
  ScaleType = 0
  Source = -> [Cut010]
  Views = -> [ProjItem,ProjItem001]
  X = 81.0853
  Y = 127.683
  spacingX = 15
  spacingY = 15
FEATURE [TechDraw::DrawViewDimension] Dimension
  AngleOverride = false
  Arbitrary = false
  ArbitraryTolerances = false
  EqualTolerance = true
  ExtensionAngle = 0
  FormatSpec = %.2w
  FormatSpecOverTolerance = %+.2w
  FormatSpecUnderTolerance = %+.2w
  Inverted = false
  LineAngle = 0
  LockPosition = false
  MeasureType = 1
  OverTolerance = 0
  References2D = -> [ProjItem001]
  Rotation = 0
  ScaleType = 0
  TheoreticalExact = false
  Type = 1
  UnderTolerance = 0
  X = 0
  Y = 69.5205
FEATURE [TechDraw::DrawViewDimension] Dimension001
  AngleOverride = false
  Arbitrary = false
  ArbitraryTolerances = false
  EqualTolerance = true
  ExtensionAngle = 0
  FormatSpec = %.2w
  FormatSpecOverTolerance = %+.2w
  FormatSpecUnderTolerance = %+.2w
  Inverted = false
  LineAngle = 0
  LockPosition = false
  MeasureType = 1
  OverTolerance = 0
  References2D = -> [ProjItem001]
  Rotation = 0
  ScaleType = 0
  TheoreticalExact = false
  Type = 2
  UnderTolerance = 0
  X = -13.7249
  Y = 2.5
FEATURE [TechDraw::DrawViewDimension] Dimension002
  AngleOverride = false
  Arbitrary = false
  ArbitraryTolerances = false
  EqualTolerance = true
  ExtensionAngle = 0
  FormatSpec = ⌀%.2w
  FormatSpecOverTolerance = %+.2w
  FormatSpecUnderTolerance = %+.2w
  Inverted = false
  LineAngle = 0
  LockPosition = false
  MeasureType = 1
  OverTolerance = 0
  References2D = -> [ProjItem]
  Rotation = 0
  ScaleType = 0
  TheoreticalExact = false
  Type = 5
  UnderTolerance = 0
  X = 26.0014
  Y = -5.98032
FEATURE [TechDraw::DrawViewDimension] Dimension003
  AngleOverride = false
  Arbitrary = false
  ArbitraryTolerances = false
  EqualTolerance = true
  ExtensionAngle = 0
  FormatSpec = ⌀%.2w
  FormatSpecOverTolerance = %+.2w
  FormatSpecUnderTolerance = %+.2w
  Inverted = false
  LineAngle = 0
  LockPosition = false
  MeasureType = 1
  OverTolerance = 0
  References2D = -> [ProjItem]
  Rotation = 0
  ScaleType = 0
  TheoreticalExact = false
  Type = 5
  UnderTolerance = 0
  X = 16.1209
  Y = 15.6008
FEATURE [TechDraw::DrawViewDimension] Dimension004
  AngleOverride = false
  Arbitrary = false
  ArbitraryTolerances = false
  EqualTolerance = true
  ExtensionAngle = 0
  FormatSpec = ⌀%.2w
  FormatSpecOverTolerance = %+.2w
  FormatSpecUnderTolerance = %+.2w
  Inverted = false
  LineAngle = 0
  LockPosition = false
  MeasureType = 1
  OverTolerance = 0
  References2D = -> [ProjItem]
  Rotation = 0
  ScaleType = 0
  TheoreticalExact = false
  Type = 5
  UnderTolerance = 0
  X = -15.3841
  Y = 32.9351
FEATURE [TechDraw::DrawViewDimension] Dimension005
  AngleOverride = false
  Arbitrary = false
  ArbitraryTolerances = false
  EqualTolerance = true
  ExtensionAngle = 0
  FormatSpec = ⌀%.2w (8x)
  FormatSpecOverTolerance = %+.2w
  FormatSpecUnderTolerance = %+.2w
  Inverted = false
  LineAngle = 0
  LockPosition = false
  MeasureType = 1
  OverTolerance = 0
  References2D = -> [ProjItem]
  Rotation = 0
  ScaleType = 0
  TheoreticalExact = false
  Type = 5
  UnderTolerance = 0
  X = 30.3179
  Y = 8.53362
FEATURE [TechDraw::DrawViewDimension] Dimension006
  AngleOverride = false
  Arbitrary = false
  ArbitraryTolerances = false
  EqualTolerance = true
  ExtensionAngle = 0
  FormatSpec = R%.2w
  FormatSpecOverTolerance = %+.2w
  FormatSpecUnderTolerance = %+.2w
  Inverted = false
  LineAngle = 0
  LockPosition = false
  MeasureType = 1
  OverTolerance = 0
  References2D = -> [ProjItem]
  Rotation = 0
  ScaleType = 0
  TheoreticalExact = false
  Type = 4
  UnderTolerance = 0
  X = 38.1692
  Y = -2.68491
FEATURE [TechDraw::DrawViewDimension] Dimension007
  AngleOverride = false
  Arbitrary = false
  ArbitraryTolerances = false
  EqualTolerance = true
  ExtensionAngle = 0
  FormatSpec = ⌀%.2w
  FormatSpecOverTolerance = %+.2w
  FormatSpecUnderTolerance = %+.2w
  Inverted = false
  LineAngle = 0
  LockPosition = false
  MeasureType = 1
  OverTolerance = 0
  References2D = -> [ProjItem]
  Rotation = 0
  ScaleType = 0
  TheoreticalExact = false
  Type = 5
  UnderTolerance = 0
  X = 5.93397
  Y = 35.3665
FEATURE [TechDraw::DrawViewDimension] Dimension008
  AngleOverride = false
  Arbitrary = false
  ArbitraryTolerances = false
  EqualTolerance = true
  ExtensionAngle = 0
  FormatSpec = ⌀%.2w (8x M4)
  FormatSpecOverTolerance = %+.2w
  FormatSpecUnderTolerance = %+.2w
  Inverted = false
  LineAngle = 0
  LockPosition = false
  MeasureType = 1
  OverTolerance = 0
  References2D = -> [ProjItem]
  Rotation = 0
  ScaleType = 0
  TheoreticalExact = false
  Type = 5
  UnderTolerance = 0
  X = 62.3067
  Y = 54.6321
FEATURE [TechDraw::DrawViewDimension] Dimension009
  AngleOverride = false
  Arbitrary = false
  ArbitraryTolerances = false
  EqualTolerance = true
  ExtensionAngle = 0
  FormatSpec = ⌀%.2w (8x)
  FormatSpecOverTolerance = %+.2w
  FormatSpecUnderTolerance = %+.2w
  Inverted = false
  LineAngle = 0
  LockPosition = false
  MeasureType = 1
  OverTolerance = 0
  References2D = -> [ProjItem]
  Rotation = 0
  ScaleType = 0
  TheoreticalExact = false
  Type = 5
  UnderTolerance = 0
  X = 67.2121
  Y = 43.1993
FEATURE [TechDraw::DrawViewDimension] Dimension010
  AngleOverride = false
  Arbitrary = false
  ArbitraryTolerances = false
  EqualTolerance = true
  ExtensionAngle = 0
  FormatSpec = %.2w
  FormatSpecOverTolerance = %+.2w
  FormatSpecUnderTolerance = %+.2w
  Inverted = false
  LineAngle = 0
  LockPosition = false
  MeasureType = 1
  OverTolerance = 0
  References2D = -> [ProjItem]
  Rotation = 0
  ScaleType = 0
  TheoreticalExact = false
  Type = 6
  UnderTolerance = 0
  X = -47.4718
  Y = 56.4914
FEATURE [TechDraw::DrawViewDimension] Dimension011
  AngleOverride = false
  Arbitrary = false
  ArbitraryTolerances = false
  EqualTolerance = true
  ExtensionAngle = 0
  FormatSpec = %.2w
  FormatSpecOverTolerance = %+.2w
  FormatSpecUnderTolerance = %+.2w
  Inverted = false
  LineAngle = 0
  LockPosition = false
  MeasureType = 1
  OverTolerance = 0
  References2D = -> [ProjItem]
  Rotation = 0
  ScaleType = 0
  TheoreticalExact = false
  Type = 2
  UnderTolerance = 0
  X = -40.7742
  Y = 10.0235
FEATURE [TechDraw::DrawViewDimension] Dimension012
  AngleOverride = false
  Arbitrary = false
  ArbitraryTolerances = false
  EqualTolerance = true
  ExtensionAngle = 0
  FormatSpec = %.2w
  FormatSpecOverTolerance = %+.2w
  FormatSpecUnderTolerance = %+.2w
  Inverted = false
  LineAngle = 0
  LockPosition = false
  MeasureType = 1
  OverTolerance = 0
  References2D = -> [ProjItem]
  Rotation = 0
  ScaleType = 0
  TheoreticalExact = false
  Type = 6
  UnderTolerance = 0
  X = -58.1529
  Y = 34.417
FEATURE [TechDraw::DrawViewDimension] Dimension013
  AngleOverride = false
  Arbitrary = false
  ArbitraryTolerances = false
  EqualTolerance = true
  ExtensionAngle = 0
  FormatSpec = %.2w
  FormatSpecOverTolerance = %+.2w
  FormatSpecUnderTolerance = %+.2w
  Inverted = false
  LineAngle = 0
  LockPosition = false
  MeasureType = 1
  OverTolerance = 0
  References2D = -> [ProjItem]
  Rotation = 0
  ScaleType = 0
  TheoreticalExact = false
  Type = 6
  UnderTolerance = 0
  X = 34.043
  Y = 60.293
FEATURE [TechDraw::DrawViewSection] SectionView  label="Section  - "
  BaseView = -> ProjItem
  CoarseView = false
  CutSurfaceDisplay = 2
  Direction = (0,-1,0)
  FileGeomPattern = <path>
  FileHatchPattern = <path>
  Focus = 100
  FuseBeforeCut = false
  HardHidden = false
  HatchScale = 1
  IsoCount = 0
  IsoHidden = false
  IsoVisible = false
  LockPosition = false
  NameGeomPattern = Diamond
  Perspective = false
  Rotation = 0
  ScaleType = 2
  SeamHidden = false
  SeamVisible = true
  SectionDirection = 3
  SectionNormal = (0,-1,0)
  SectionOrigin = (0.038,0,2.5)
  SmoothHidden = false
  SmoothVisible = true
  Source = -> [Cut010]
  X = 72.1219
  XDirection = (-1,0,0)
  Y = 40.7089
FEATURE [TechDraw::DrawViewDimension] Dimension014
  AngleOverride = false
  Arbitrary = false
  ArbitraryTolerances = false
  EqualTolerance = true
  ExtensionAngle = 0
  FormatSpec = %.2w
  FormatSpecOverTolerance = %+.2w
  FormatSpecUnderTolerance = %+.2w
  Inverted = false
  LineAngle = 0
  LockPosition = false
  MeasureType = 1
  OverTolerance = 0
  References2D = -> [SectionView]
  Rotation = 0
  ScaleType = 0
  TheoreticalExact = false
  Type = 2
  UnderTolerance = 0
  X = 64.9678
  Y = 16.8618
FEATURE [TechDraw::DrawViewDimension] Dimension015
  AngleOverride = false
  Arbitrary = false
  ArbitraryTolerances = false
  EqualTolerance = true
  ExtensionAngle = 0
  FormatSpec = %.2w
  FormatSpecOverTolerance = %+.2w
  FormatSpecUnderTolerance = %+.2w
  Inverted = false
  LineAngle = 0
  LockPosition = false
  MeasureType = 1
  OverTolerance = 0
  References2D = -> [SectionView]
  Rotation = 0
  ScaleType = 0
  TheoreticalExact = false
  Type = 2
  UnderTolerance = 0
  X = 58.8699
  Y = -9.8339
FEATURE [TechDraw::DrawViewDimension] Dimension016
  AngleOverride = false
  Arbitrary = false
  ArbitraryTolerances = false
  EqualTolerance = true
  ExtensionAngle = 0
  FormatSpec = %.2w
  FormatSpecOverTolerance = %+.2w
  FormatSpecUnderTolerance = %+.2w
  Inverted = false
  LineAngle = 0
  LockPosition = false
  MeasureType = 1
  OverTolerance = 0
  References2D = -> [SectionView]
  Rotation = 0
  ScaleType = 0
  TheoreticalExact = false
  Type = 1
  UnderTolerance = 0
  X = 37.6693
  Y = 16.2953
FEATURE [TechDraw::DrawViewDimension] Dimension017
  AngleOverride = false
  Arbitrary = false
  ArbitraryTolerances = false
  EqualTolerance = true
  ExtensionAngle = 0
  FormatSpec = %.2w
  FormatSpecOverTolerance = %+.2w
  FormatSpecUnderTolerance = %+.2w
  Inverted = false
  LineAngle = 0
  LockPosition = false
  MeasureType = 1
  OverTolerance = 0
  References2D = -> [SectionView]
  Rotation = 0
  ScaleType = 0
  TheoreticalExact = false
  Type = 1
  UnderTolerance = 0
  X = 37.9214
  Y = -3.99108
FEATURE [TechDraw::DrawViewDimension] Dimension018
  AngleOverride = false
  Arbitrary = false
  ArbitraryTolerances = false
  EqualTolerance = true
  ExtensionAngle = 0
  FormatSpec = %.2w
  FormatSpecOverTolerance = %+.2w
  FormatSpecUnderTolerance = %+.2w
  Inverted = false
  LineAngle = 0
  LockPosition = false
  MeasureType = 1
  OverTolerance = 0
  References2D = -> [SectionView]
  Rotation = 0
  ScaleType = 0
  TheoreticalExact = false
  Type = 1
  UnderTolerance = 0
  X = -44.6513
  Y = 15.5079
FEATURE [TechDraw::DrawViewAnnotation] Annotation
  Font = osifont
  LineSpace = 80
  LockPosition = false
  MaxWidth = -1
  Rotation = 0
  ScaleType = 0
  Text = Ring with: | * 8x 5mm through holes | * 8x M4 tapped holes | * 8x 3.6mm through holes for M3 |    DIN912 screw heads. |   (M3 screw heads sunken |   into the lugs)
  TextSize = 5
  TextStyle = 0
  X = 250.875
  Y = 168.492
FEATURE [TechDraw::DrawPage] Page
  KeepUpdated = true
  NextBalloonIndex = 1
  ProjectionType = 0
  Template = -> Template
  Views = -> [ProjGroup,Dimension,Dimension001,Dimension002,Dimension003,Dimension004,Dimension005,Dimension006,Dimension007,Dimension008,Dimension009,Dimension010,Dimension011,Dimension012,Dimension013,SectionView,Dimension014,Dimension015,Dimension016,Dimension017,Dimension018,Annotation]
note: 2 file-system paths scrubbed to <path> (originals preserved in the JSON sidecar)
---- part XL30ColumnAttachmentRing_PCBKicker01.FCStd = doc fcstd_5df1f01fb415 ----
FCSTD DOCUMENT  (FreeCAD 0.20R)
Label: XL30ColumnAttachmentRing_PCBKicker01
License: All rights reserved
LicenseURL: http://en.wikipedia.org/wiki/All_rights_reserved
objects: Part::Cylinder×30, TechDraw::DrawViewDimension×23, Part::Compound×20, Part::Cut×7, TechDraw::DrawProjGroupItem×4, Part::Box×3, Part::MultiFuse×2, TechDraw::DrawSVGTemplate×2, TechDraw::DrawProjGroup×2, TechDraw::DrawPage×2, Part::MultiCommon×1, TechDraw::DrawViewSection×1, TechDraw::DrawViewAnnotation×1
note: 63 computed .brp shape members not serialized (recipe doc carries the construction recipe); baked Part::Feature solids carry a one-line shape summary decoded from their .brp
EXTERNAL_REF file=XL30ColumnAttachmentRing01.FCStd obj=Spreadsheet

FEATURE [Part::Cylinder] Cylinder
  Angle = 360
  AttacherType = Attacher::AttachEngine3D
  FirstAngle = 0
  Height = 5
  Radius = 57.66
  SecondAngle = 0
  expr: Height = <<XL30ColumnAttachmentRing01>>#<<AttachmentRing01>>.ring_thickness
  expr: Radius = <<XL30ColumnAttachmentRing01>>#<<AttachmentRing01>>.ring_od / 2
FEATURE [Part::Cylinder] Cylinder001
  Angle = 360
  AttacherType = Attacher::AttachEngine3D
  FirstAngle = 0
  Height = 5
  Radius = 50
  SecondAngle = 0
  expr: Height = <<XL30ColumnAttachmentRing01>>#<<AttachmentRing01>>.ring_thickness
  expr: Radius = <<XL30ColumnAttachmentRing01>>#<<AttachmentRing01>>.ring_id / 2
FEATURE [Part::Cut] Cut
  Base = -> Cylinder
  Tool = -> Cylinder001
FEATURE [Part::Cylinder] Cylinder002
  Angle = 360
  AttacherType = Attacher::AttachEngine3D
  FirstAngle = 0
  Height = 5
  Placement = pos=(53.83,0,0) rot=(0,0,1;0rad)
  Radius = 2.15
  SecondAngle = 0
  expr: .Placement.Base.x = (<<XL30ColumnAttachmentRing01>>#<<AttachmentRing01>>.ring_od + <<XL30ColumnAttachmentRing01>>#<<AttachmentRing01>>.ring_id) / 4
  expr: Height = <<XL30ColumnAttachmentRing01>>#<<AttachmentRing01>>.ring_thickness
FEATURE [Part::Compound] Compound
  Links = -> [Cylinder002]
FEATURE [Part::Cylinder] Cylinder003
  Angle = 360
  AttacherType = Attacher::AttachEngine3D
  FirstAngle = 0
  Height = 5
  Placement = pos=(53.83,0,0) rot=(0,0,1;0rad)
  Radius = 2.15
  SecondAngle = 0
  expr: .Placement.Base.x = (<<XL30ColumnAttachmentRing01>>#<<AttachmentRing01>>.ring_od + <<XL30ColumnAttachmentRing01>>#<<AttachmentRing01>>.ring_id) / 4
  expr: Height = <<XL30ColumnAttachmentRing01>>#<<AttachmentRing01>>.ring_thickness
FEATURE [Part::Compound] Compound001
  Links = -> [Cylinder003]
  Placement = pos=(0,0,0) rot=(0,0,1;0.785398rad)
FEATURE [Part::Cylinder] Cylinder004
  Angle = 360
  AttacherType = Attacher::AttachEngine3D
  FirstAngle = 0
  Height = 5
  Placement = pos=(53.83,0,0) rot=(0,0,1;0rad)
  Radius = 2.15
  SecondAngle = 0
  expr: .Placement.Base.x = (<<XL30ColumnAttachmentRing01>>#<<AttachmentRing01>>.ring_od + <<XL30ColumnAttachmentRing01>>#<<AttachmentRing01>>.ring_id) / 4
  expr: Height = <<XL30ColumnAttachmentRing01>>#<<AttachmentRing01>>.ring_thickness
FEATURE [Part::Compound] Compound002
  Links = -> [Cylinder004]
  Placement = pos=(0,0,0) rot=(0,0,1;1.5708rad)
FEATURE [Part::Cylinder] Cylinder005
  Angle = 360
  AttacherType = Attacher::AttachEngine3D
  FirstAngle = 0
  Height = 5
  Placement = pos=(53.83,0,0) rot=(0,0,1;0rad)
  Radius = 2.15
  SecondAngle = 0
  expr: .Placement.Base.x = (<<XL30ColumnAttachmentRing01>>#<<AttachmentRing01>>.ring_od + <<XL30ColumnAttachmentRing01>>#<<AttachmentRing01>>.ring_id) / 4
  expr: Height = <<XL30ColumnAttachmentRing01>>#<<AttachmentRing01>>.ring_thickness
FEATURE [Part::Compound] Compound003
  Links = -> [Cylinder005]
  Placement = pos=(0,0,0) rot=(0,0,1;2.35619rad)
FEATURE [Part::Cylinder] Cylinder006
  Angle = 360
  AttacherType = Attacher::AttachEngine3D
  FirstAngle = 0
  Height = 5
  Placement = pos=(53.83,0,0) rot=(0,0,1;0rad)
  Radius = 2.15
  SecondAngle = 0
  expr: .Placement.Base.x = (<<XL30ColumnAttachmentRing01>>#<<AttachmentRing01>>.ring_od + <<XL30ColumnAttachmentRing01>>#<<AttachmentRing01>>.ring_id) / 4
  expr: Height = <<XL30ColumnAttachmentRing01>>#<<AttachmentRing01>>.ring_thickness
FEATURE [Part::Compound] Compound004
  Links = -> [Cylinder006]
  Placement = pos=(0,0,0) rot=(0,0,1;3.14159rad)
FEATURE [Part::Cylinder] Cylinder007
  Angle = 360
  AttacherType = Attacher::AttachEngine3D
  FirstAngle = 0
  Height = 5
  Placement = pos=(53.83,0,0) rot=(0,0,1;0rad)
  Radius = 2.15
  SecondAngle = 0
  expr: .Placement.Base.x = (<<XL30ColumnAttachmentRing01>>#<<AttachmentRing01>>.ring_od + <<XL30ColumnAttachmentRing01>>#<<AttachmentRing01>>.ring_id) / 4
  expr: Height = <<XL30ColumnAttachmentRing01>>#<<AttachmentRing01>>.ring_thickness
FEATURE [Part::Compound] Compound005
  Links = -> [Cylinder007]
  Placement = pos=(0,0,0) rot=(0,0,1;3.92699rad)
FEATURE [Part::Cylinder] Cylinder008
  Angle = 360
  AttacherType = Attacher::AttachEngine3D
  FirstAngle = 0
  Height = 5
  Placement = pos=(53.83,0,0) rot=(0,0,1;0rad)
  Radius = 2.15
  SecondAngle = 0
  expr: .Placement.Base.x = (<<XL30ColumnAttachmentRing01>>#<<AttachmentRing01>>.ring_od + <<XL30ColumnAttachmentRing01>>#<<AttachmentRing01>>.ring_id) / 4
  expr: Height = <<XL30ColumnAttachmentRing01>>#<<AttachmentRing01>>.ring_thickness
FEATURE [Part::Compound] Compound006
  Links = -> [Cylinder008]
  Placement = pos=(0,0,0) rot=(0,0,1;4.71239rad)
FEATURE [Part::Cylinder] Cylinder009
  Angle = 360
  AttacherType = Attacher::AttachEngine3D
  FirstAngle = 0
  Height = 5
  Placement = pos=(53.83,0,0) rot=(0,0,1;0rad)
  Radius = 2.15
  SecondAngle = 0
  expr: .Placement.Base.x = (<<XL30ColumnAttachmentRing01>>#<<AttachmentRing01>>.ring_od + <<XL30ColumnAttachmentRing01>>#<<AttachmentRing01>>.ring_id) / 4
  expr: Height = <<XL30ColumnAttachmentRing01>>#<<AttachmentRing01>>.ring_thickness
FEATURE [Part::Compound] Compound007
  Links = -> [Cylinder009]
  Placement = pos=(0,0,0) rot=(0,0,1;5.49779rad)
FEATURE [Part::Compound] Compound008  label="M4ThroughHoles"
  Links = -> [Compound,Compound001,Compound002,Compound003,Compound004,Compound005,Compound006,Compound007]
FEATURE [Part::Cut] Cut001  label="OuterBaseRing"
  Base = -> Cut
  Tool = -> Compound008
FEATURE [Part::Cylinder] Cylinder010
  Angle = 360
  AttacherType = Attacher::AttachEngine3D
  FirstAngle = 0
  Height = 5
  Radius = 57.66
  SecondAngle = 0
  expr: Height = <<XL30ColumnAttachmentRing01>>#<<AttachmentRing01>>.ring_thickness
  expr: Radius = <<XL30ColumnAttachmentRing01>>#<<AttachmentRing01>>.ring_od / 2
FEATURE [Part::Cylinder] Cylinder011
  Angle = 360
  AttacherType = Attacher::AttachEngine3D
  FirstAngle = 0
  Height = 5
  Radius = 50
  SecondAngle = 0
  expr: Height = <<XL30ColumnAttachmentRing01>>#<<AttachmentRing01>>.ring_thickness
  expr: Radius = <<XL30ColumnAttachmentRing01>>#<<AttachmentRing01>>.ring_id / 2
FEATURE [Part::Cut] Cut002
  Base = -> Cylinder010
  Tool = -> Cylinder011
FEATURE [Part::Cylinder] Cylinder012
  Angle = 360
  AttacherType = Attacher::AttachEngine3D
  FirstAngle = 0
  Height = 5
  Placement = pos=(53.83,0,0) rot=(0,0,1;0rad)
  Radius = 2.15
  SecondAngle = 0
  expr: .Placement.Base.x = (<<XL30ColumnAttachmentRing01>>#<<AttachmentRing01>>.ring_od + <<XL30ColumnAttachmentRing01>>#<<AttachmentRing01>>.ring_id) / 4
  expr: Height = <<XL30ColumnAttachmentRing01>>#<<AttachmentRing01>>.ring_thickness
FEATURE [Part::Compound] Compound009
  Links = -> [Cylinder012]
FEATURE [Part::Cylinder] Cylinder013
  Angle = 360
  AttacherType = Attacher::AttachEngine3D
  FirstAngle = 0
  Height = 5
  Placement = pos=(53.83,0,0) rot=(0,0,1;0rad)
  Radius = 2.15
  SecondAngle = 0
  expr: .Placement.Base.x = (<<XL30ColumnAttachmentRing01>>#<<AttachmentRing01>>.ring_od + <<XL30ColumnAttachmentRing01>>#<<AttachmentRing01>>.ring_id) / 4
  expr: Height = <<XL30ColumnAttachmentRing01>>#<<AttachmentRing01>>.ring_thickness
FEATURE [Part::Compound] Compound010
  Links = -> [Cylinder013]
  Placement = pos=(0,0,0) rot=(0,0,1;0.785398rad)
FEATURE [Part::Cylinder] Cylinder014
  Angle = 360
  AttacherType = Attacher::AttachEngine3D
  FirstAngle = 0
  Height = 5
  Placement = pos=(53.83,0,0) rot=(0,0,1;0rad)
  Radius = 2.15
  SecondAngle = 0
  expr: .Placement.Base.x = (<<XL30ColumnAttachmentRing01>>#<<AttachmentRing01>>.ring_od + <<XL30ColumnAttachmentRing01>>#<<AttachmentRing01>>.ring_id) / 4
  expr: Height = <<XL30ColumnAttachmentRing01>>#<<AttachmentRing01>>.ring_thickness
FEATURE [Part::Compound] Compound011
  Links = -> [Cylinder014]
  Placement = pos=(0,0,0) rot=(0,0,1;1.5708rad)
FEATURE [Part::Cylinder] Cylinder015
  Angle = 360
  AttacherType = Attacher::AttachEngine3D
  FirstAngle = 0
  Height = 5
  Placement = pos=(53.83,0,0) rot=(0,0,1;0rad)
  Radius = 2.15
  SecondAngle = 0
  expr: .Placement.Base.x = (<<XL30ColumnAttachmentRing01>>#<<AttachmentRing01>>.ring_od + <<XL30ColumnAttachmentRing01>>#<<AttachmentRing01>>.ring_id) / 4
  expr: Height = <<XL30ColumnAttachmentRing01>>#<<AttachmentRing01>>.ring_thickness
FEATURE [Part::Compound] Compound012
  Links = -> [Cylinder015]
  Placement = pos=(0,0,0) rot=(0,0,1;2.35619rad)
FEATURE [Part::Cylinder] Cylinder016
  Angle = 360
  AttacherType = Attacher::AttachEngine3D
  FirstAngle = 0
  Height = 5
  Placement = pos=(53.83,0,0) rot=(0,0,1;0rad)
  Radius = 2.15
  SecondAngle = 0
  expr: .Placement.Base.x = (<<XL30ColumnAttachmentRing01>>#<<AttachmentRing01>>.ring_od + <<XL30ColumnAttachmentRing01>>#<<AttachmentRing01>>.ring_id) / 4
  expr: Height = <<XL30ColumnAttachmentRing01>>#<<AttachmentRing01>>.ring_thickness
FEATURE [Part::Compound] Compound013
  Links = -> [Cylinder016]
  Placement = pos=(0,0,0) rot=(0,0,1;3.14159rad)
FEATURE [Part::Cylinder] Cylinder017
  Angle = 360
  AttacherType = Attacher::AttachEngine3D
  FirstAngle = 0
  Height = 5
  Placement = pos=(53.83,0,0) rot=(0,0,1;0rad)
  Radius = 2.15
  SecondAngle = 0
  expr: .Placement.Base.x = (<<XL30ColumnAttachmentRing01>>#<<AttachmentRing01>>.ring_od + <<XL30ColumnAttachmentRing01>>#<<AttachmentRing01>>.ring_id) / 4
  expr: Height = <<XL30ColumnAttachmentRing01>>#<<AttachmentRing01>>.ring_thickness
FEATURE [Part::Compound] Compound014
  Links = -> [Cylinder017]
  Placement = pos=(0,0,0) rot=(0,0,1;3.92699rad)
FEATURE [Part::Cylinder] Cylinder018
  Angle = 360
  AttacherType = Attacher::AttachEngine3D
  FirstAngle = 0
  Height = 5
  Placement = pos=(53.83,0,0) rot=(0,0,1;0rad)
  Radius = 2.15
  SecondAngle = 0
  expr: .Placement.Base.x = (<<XL30ColumnAttachmentRing01>>#<<AttachmentRing01>>.ring_od + <<XL30ColumnAttachmentRing01>>#<<AttachmentRing01>>.ring_id) / 4
  expr: Height = <<XL30ColumnAttachmentRing01>>#<<AttachmentRing01>>.ring_thickness
FEATURE [Part::Compound] Compound015
  Links = -> [Cylinder018]
  Placement = pos=(0,0,0) rot=(0,0,-1;1.5708rad)
FEATURE [Part::Cylinder] Cylinder019
  Angle = 360
  AttacherType = Attacher::AttachEngine3D
  FirstAngle = 0
  Height = 5
  Placement = pos=(53.83,0,0) rot=(0,0,1;0rad)
  Radius = 2.15
  SecondAngle = 0
  expr: .Placement.Base.x = (<<XL30ColumnAttachmentRing01>>#<<AttachmentRing01>>.ring_od + <<XL30ColumnAttachmentRing01>>#<<AttachmentRing01>>.ring_id) / 4
  expr: Height = <<XL30ColumnAttachmentRing01>>#<<AttachmentRing01>>.ring_thickness
FEATURE [Part::Compound] Compound016
  Links = -> [Cylinder019]
  Placement = pos=(0,0,0) rot=(0,0,-1;0.785398rad)
FEATURE [Part::Compound] Compound017  label="M4ThroughHoles001"
  Links = -> [Compound009,Compound010,Compound011,Compound012,Compound013,Compound014,Compound015,Compound016]
FEATURE [Part::Cut] Cut003  label="Ring01"
  Base = -> Cut002
  Tool = -> Compound017
FEATURE [Part::Box] Box  label="Cube"
  AttacherType = Attacher::AttachEngine3D
  Height = 20
  Length = 40
  Width = 42
FEATURE [Part::Cylinder] Cylinder020
  Angle = 360
  AttacherType = Attacher::AttachEngine3D
  FirstAngle = 0
  Height = 20
  Placement = pos=(10,21,0) rot=(0,0,1;0rad)
  Radius = 2
  SecondAngle = 0
FEATURE [Part::Cut] Cut004
  Base = -> Box
  Tool = -> Cylinder020
FEATURE [Part::Cylinder] Cylinder021
  Angle = 360
  AttacherType = Attacher::AttachEngine3D
  FirstAngle = 0
  Height = 20
  Placement = pos=(2.5,2.5,0) rot=(0,0,1;0rad)
  Radius = 1.3
  SecondAngle = 0
FEATURE [Part::Cylinder] Cylinder022
  Angle = 360
  AttacherType = Attacher::AttachEngine3D
  FirstAngle = 0
  Height = 20
  Placement = pos=(37.5,2.5,0) rot=(0,0,1;0rad)
  Radius = 1.3
  SecondAngle = 0
FEATURE [Part::Cylinder] Cylinder023
  Angle = 360
  AttacherType = Attacher::AttachEngine3D
  FirstAngle = 0
  Height = 20
  Placement = pos=(2.5,39.5,0) rot=(0,0,1;0rad)
  Radius = 1.3
  SecondAngle = 0
FEATURE [Part::Cylinder] Cylinder024
  Angle = 360
  AttacherType = Attacher::AttachEngine3D
  FirstAngle = 0
  Height = 20
  Placement = pos=(37.5,39.5,0) rot=(0,0,1;0rad)
  Radius = 1.3
  SecondAngle = 0
FEATURE [Part::Compound] Compound018
  Links = -> [Cylinder021,Cylinder022,Cylinder023,Cylinder024]
FEATURE [Part::Cut] Cut005  label="PCBStackTemplate"
  Base = -> Cut004
  Placement = pos=(-10,-21,5) rot=(0,0,1;0rad)
  Tool = -> Compound018
FEATURE [Part::Cylinder] Cylinder025
  Angle = 360
  AttacherType = Attacher::AttachEngine3D
  FirstAngle = 0
  Height = 20
  Placement = pos=(2.5,2.5,0) rot=(0,0,1;0rad)
  Radius = 1.3
  SecondAngle = 0
FEATURE [Part::Cylinder] Cylinder026
  Angle = 360
  AttacherType = Attacher::AttachEngine3D
  FirstAngle = 0
  Height = 20
  Placement = pos=(37.5,2.5,0) rot=(0,0,1;0rad)
  Radius = 1.3
  SecondAngle = 0
FEATURE [Part::Cylinder] Cylinder027
  Angle = 360
  AttacherType = Attacher::AttachEngine3D
  FirstAngle = 0
  Height = 20
  Placement = pos=(2.5,39.5,0) rot=(0,0,1;0rad)
  Radius = 1.3
  SecondAngle = 0
FEATURE [Part::Cylinder] Cylinder028
  Angle = 360
  AttacherType = Attacher::AttachEngine3D
  FirstAngle = 0
  Height = 20
  Placement = pos=(37.5,39.5,0) rot=(0,0,1;0rad)
  Radius = 1.3
  SecondAngle = 0
FEATURE [Part::Compound] Compound019  label="M3Mountholes"
  Links = -> [Cylinder025,Cylinder026,Cylinder027,Cylinder028]
  Placement = pos=(-10,-21,0) rot=(0,0,1;0rad)
FEATURE [Part::Box] Box001  label="Cube001"
  AttacherType = Attacher::AttachEngine3D
  Height = 3
  Length = 115.32
  Placement = pos=(-57.66,-21,2) rot=(0,0,1;0rad)
  Width = 5
  expr: .Placement.Base.x = -<<XL30ColumnAttachmentRing01>>#<<AttachmentRing01>>.ring_od / 2
  expr: .Placement.Base.z = <<XL30ColumnAttachmentRing01>>#<<AttachmentRing01>>.ring_thickness - 3
  expr: Length = <<XL30ColumnAttachmentRing01>>#<<AttachmentRing01>>.ring_od
FEATURE [Part::Box] Box002  label="Cube002"
  AttacherType = Attacher::AttachEngine3D
  Height = 3
  Length = 115.32
  Placement = pos=(-57.66,16,2) rot=(0,0,1;0rad)
  Width = 5
  expr: .Placement.Base.x = -<<XL30ColumnAttachmentRing01>>#<<AttachmentRing01>>.ring_od / 2
  expr: .Placement.Base.z = <<XL30ColumnAttachmentRing01>>#<<AttachmentRing01>>.ring_thickness - 3
  expr: Length = <<XL30ColumnAttachmentRing01>>#<<AttachmentRing01>>.ring_od
FEATURE [Part::MultiFuse] Fusion
  Shapes = -> [Box001,Box002]
FEATURE [Part::Cylinder] Cylinder029
  Angle = 360
  AttacherType = Attacher::AttachEngine3D
  FirstAngle = 0
  Height = 5
  Radius = 57.66
  SecondAngle = 0
  expr: Height = <<XL30ColumnAttachmentRing01>>#<<AttachmentRing01>>.ring_thickness
  expr: Radius = <<XL30ColumnAttachmentRing01>>#<<AttachmentRing01>>.ring_od / 2
FEATURE [Part::MultiCommon] Common
  Shapes = -> [Fusion,Cylinder029]
FEATURE [Part::Cut] Cut006
  Base = -> Common
  Tool = -> Compound019
FEATURE [Part::MultiFuse] Fusion001  label="Stackmountring01"
  Shapes = -> [Cut003,Cut006]
FEATURE [TechDraw::DrawSVGTemplate] Template
  EditableTexts = Designed_by_Name=Thomas Spielauer; FC-Date=2023-11-15; FC-SC=mm; FC-SH=1/1; FC-Title=XL30 column cage: PCB mount; Subtitle=Compatible with XL30 column attachment ring
  Height = 210
  Orientation = 1
  Width = 297
FEATURE [TechDraw::DrawProjGroupItem] ProjItem  label="Front"
  CoarseView = false
  Direction = (0,0,1)
  Focus = 100
  HardHidden = false
  IsoCount = 0
  IsoHidden = false
  IsoVisible = false
  LockPosition = true
  Perspective = false
  Rotation = 0
  RotationVector = (1,0,0)
  ScaleType = 2
  SeamHidden = false
  SeamVisible = true
  SmoothHidden = false
  SmoothVisible = true
  Source = -> [Fusion001]
  Type = 0
  X = 0
  XDirection = (1,0,0)
  Y = 0
FEATURE [TechDraw::DrawProjGroupItem] ProjItem002  label="Top"
  CoarseView = false
  Direction = (0,1,0)
  Focus = 100
  HardHidden = false
  IsoCount = 0
  IsoHidden = false
  IsoVisible = false
  LockPosition = false
  Perspective = false
  Rotation = 0
  RotationVector = (1,0,0)
  ScaleType = 2
  SeamHidden = false
  SeamVisible = true
  SmoothHidden = false
  SmoothVisible = true
  Source = -> [Fusion001]
  Type = 4
  X = 0
  XDirection = (1,0,0)
  Y = -130.32
FEATURE [TechDraw::DrawProjGroup] ProjGroup
  Anchor = -> ProjItem
  AutoDistribute = true
  LockPosition = false
  ProjectionType = 0
  Rotation = 0
  ScaleType = 0
  Source = -> [Fusion001]
  Views = -> [ProjItem,ProjItem002]
  X = 77.9531
  Y = 128.789
  spacingX = 15
  spacingY = 15
FEATURE [TechDraw::DrawViewSection] SectionView  label="Section  - "
  BaseView = -> ProjItem
  CoarseView = false
  CutSurfaceDisplay = 2
  Direction = (-1,0,0)
  FileGeomPattern = <path>
  FileHatchPattern = <path>
  Focus = 100
  FuseBeforeCut = false
  HardHidden = false
  HatchScale = 1
  IsoCount = 0
  IsoHidden = false
  IsoVisible = false
  LockPosition = false
  NameGeomPattern = Diamond
  Perspective = false
  Rotation = 0
  ScaleType = 2
  SeamHidden = false
  SeamVisible = true
  SectionDirection = 0
  SectionNormal = (-1,0,0)
  SectionOrigin = (0,0,2.5)
  SmoothHidden = false
  SmoothVisible = true
  Source = -> [Fusion001]
  X = 175.93
  XDirection = (0,0,1)
  Y = 127.772
FEATURE [TechDraw::DrawViewDimension] Dimension
  AngleOverride = false
  Arbitrary = false
  ArbitraryTolerances = false
  EqualTolerance = true
  ExtensionAngle = 0
  FormatSpec = ⌀%.2w
  FormatSpecOverTolerance = %+.2w
  FormatSpecUnderTolerance = %+.2w
  Inverted = false
  LineAngle = 0
  LockPosition = false
  MeasureType = 1
  OverTolerance = 0
  References2D = -> [ProjItem]
  Rotation = 0
  ScaleType = 0
  TheoreticalExact = false
  Type = 5
  UnderTolerance = 0
  X = 61.5234
  Y = 45.459
FEATURE [TechDraw::DrawViewDimension] Dimension001
  AngleOverride = false
  Arbitrary = false
  ArbitraryTolerances = false
  EqualTolerance = true
  ExtensionAngle = 0
  FormatSpec = ⌀%.2w
  FormatSpecOverTolerance = %+.2w
  FormatSpecUnderTolerance = %+.2w
  Inverted = false
  LineAngle = 0
  LockPosition = false
  MeasureType = 1
  OverTolerance = 0
  References2D = -> [ProjItem]
  Rotation = 0
  ScaleType = 0
  TheoreticalExact = false
  Type = 5
  UnderTolerance = 0
  X = 66.6504
  Y = 36.5723
FEATURE [TechDraw::DrawViewDimension] Dimension002
  AngleOverride = false
  Arbitrary = false
  ArbitraryTolerances = false
  EqualTolerance = true
  ExtensionAngle = 0
  FormatSpec = ⌀%.2w (8x)
  FormatSpecOverTolerance = %+.2w
  FormatSpecUnderTolerance = %+.2w
  Inverted = false
  LineAngle = 0
  LockPosition = false
  MeasureType = 1
  OverTolerance = 0
  References2D = -> [ProjItem]
  Rotation = 0
  ScaleType = 0
  TheoreticalExact = false
  Type = 5
  UnderTolerance = 0
  X = 54.0039
  Y = 54.0039
FEATURE [TechDraw::DrawViewDimension] Dimension003
  AngleOverride = false
  Arbitrary = false
  ArbitraryTolerances = false
  EqualTolerance = true
  ExtensionAngle = 0
  FormatSpec = ⌀%.2w (4x M3)
  FormatSpecOverTolerance = %+.2w
  FormatSpecUnderTolerance = %+.2w
  Inverted = false
  LineAngle = 0
  LockPosition = false
  MeasureType = 1
  OverTolerance = 0
  References2D = -> [ProjItem]
  Rotation = 0
  ScaleType = 0
  TheoreticalExact = false
  Type = 5
  UnderTolerance = 0
  X = -25.2791
  Y = 6.47025
FEATURE [TechDraw::DrawViewDimension] Dimension004
  AngleOverride = false
  Arbitrary = false
  ArbitraryTolerances = false
  EqualTolerance = true
  ExtensionAngle = 0
  FormatSpec = ⌀%.2w
  FormatSpecOverTolerance = %+.2w
  FormatSpecUnderTolerance = %+.2w
  Inverted = false
  LineAngle = 0
  LockPosition = false
  MeasureType = 1
  OverTolerance = 0
  References2D = -> [ProjItem]
  Rotation = 0
  ScaleType = 0
  TheoreticalExact = false
  Type = 5
  UnderTolerance = 0
  X = 70.0684
  Y = 28.1982
FEATURE [TechDraw::DrawViewDimension] Dimension005
  AngleOverride = false
  Arbitrary = false
  ArbitraryTolerances = false
  EqualTolerance = true
  ExtensionAngle = 0
  FormatSpec = %.2w
  FormatSpecOverTolerance = %+.2w
  FormatSpecUnderTolerance = %+.2w
  Inverted = false
  LineAngle = 0
  LockPosition = false
  MeasureType = 1
  OverTolerance = 0
  References2D = -> [ProjItem]
  Rotation = 0
  ScaleType = 0
  TheoreticalExact = false
  Type = 6
  UnderTolerance = 0
  X = -32.2741
  Y = 59.9027
FEATURE [TechDraw::DrawViewDimension] Dimension006
  AngleOverride = false
  Arbitrary = false
  ArbitraryTolerances = false
  EqualTolerance = true
  ExtensionAngle = 0
  FormatSpec = %.2w
  FormatSpecOverTolerance = %+.2w
  FormatSpecUnderTolerance = %+.2w
  Inverted = false
  LineAngle = 0
  LockPosition = false
  MeasureType = 1
  OverTolerance = 0
  References2D = -> [ProjItem]
  Rotation = 0
  ScaleType = 0
  TheoreticalExact = false
  Type = 2
  UnderTolerance = 0
  X = 31.0643
  Y = -6.39286
FEATURE [TechDraw::DrawViewDimension] Dimension007
  AngleOverride = false
  Arbitrary = false
  ArbitraryTolerances = false
  EqualTolerance = true
  ExtensionAngle = 0
  FormatSpec = %.2w
  FormatSpecOverTolerance = %+.2w
  FormatSpecUnderTolerance = %+.2w
  Inverted = false
  LineAngle = 0
  LockPosition = false
  MeasureType = 1
  OverTolerance = 0
  References2D = -> [ProjItem]
  Rotation = 0
  ScaleType = 0
  TheoreticalExact = false
  Type = 2
  UnderTolerance = 0
  X = 31.3208
  Y = 10.3055
FEATURE [TechDraw::DrawViewDimension] Dimension008
  AngleOverride = false
  Arbitrary = false
  ArbitraryTolerances = false
  EqualTolerance = true
  ExtensionAngle = 0
  FormatSpec = %.2w
  FormatSpecOverTolerance = %+.2w
  FormatSpecUnderTolerance = %+.2w
  Inverted = false
  LineAngle = 0
  LockPosition = false
  MeasureType = 1
  OverTolerance = 0
  References2D = -> [ProjItem]
  Rotation = 0
  ScaleType = 0
  TheoreticalExact = false
  Type = 1
  UnderTolerance = 0
  X = -4.11113
  Y = 33.5088
FEATURE [TechDraw::DrawViewDimension] Dimension009
  AngleOverride = false
  Arbitrary = false
  ArbitraryTolerances = false
  EqualTolerance = true
  ExtensionAngle = 0
  FormatSpec = %.2w
  FormatSpecOverTolerance = %+.2w
  FormatSpecUnderTolerance = %+.2w
  Inverted = false
  LineAngle = 0
  LockPosition = false
  MeasureType = 1
  OverTolerance = 0
  References2D = -> [ProjItem]
  Rotation = 0
  ScaleType = 0
  TheoreticalExact = false
  Type = 1
  UnderTolerance = 0
  X = 14.1111
  Y = 36.2173
FEATURE [TechDraw::DrawViewDimension] Dimension010
  AngleOverride = false
  Arbitrary = false
  ArbitraryTolerances = false
  EqualTolerance = true
  ExtensionAngle = 0
  FormatSpec = %.2w
  FormatSpecOverTolerance = %+.2w
  FormatSpecUnderTolerance = %+.2w
  Inverted = false
  LineAngle = 0
  LockPosition = false
  MeasureType = 1
  OverTolerance = 0
  References2D = -> [ProjItem]
  Rotation = 0
  ScaleType = 0
  TheoreticalExact = false
  Type = 2
  UnderTolerance = 0
  X = -65.7891
  Y = 30.0196
FEATURE [TechDraw::DrawViewDimension] Dimension011
  AngleOverride = false
  Arbitrary = false
  ArbitraryTolerances = false
  EqualTolerance = true
  ExtensionAngle = 0
  FormatSpec = %.2w
  FormatSpecOverTolerance = %+.2w
  FormatSpecUnderTolerance = %+.2w
  Inverted = false
  LineAngle = 0
  LockPosition = false
  MeasureType = 1
  OverTolerance = 0
  References2D = -> [SectionView]
  Rotation = 0
  ScaleType = 0
  TheoreticalExact = false
  Type = 1
  UnderTolerance = 0
  X = 7.50034
  Y = -8.08305
FEATURE [TechDraw::DrawViewDimension] Dimension012
  AngleOverride = false
  Arbitrary = false
  ArbitraryTolerances = false
  EqualTolerance = true
  ExtensionAngle = 0
  FormatSpec = %.2w
  FormatSpecOverTolerance = %+.2w
  FormatSpecUnderTolerance = %+.2w
  Inverted = false
  LineAngle = 0
  LockPosition = false
  MeasureType = 1
  OverTolerance = 0
  References2D = -> [SectionView]
  Rotation = 0
  ScaleType = 0
  TheoreticalExact = false
  Type = 1
  UnderTolerance = 0
  X = 15.8175
  Y = -53.6967
FEATURE [TechDraw::DrawViewDimension] Dimension013
  AngleOverride = false
  Arbitrary = false
  ArbitraryTolerances = false
  EqualTolerance = true
  ExtensionAngle = 0
  FormatSpec = %.2w
  FormatSpecOverTolerance = %+.2w
  FormatSpecUnderTolerance = %+.2w
  Inverted = false
  LineAngle = 0
  LockPosition = false
  MeasureType = 1
  OverTolerance = 0
  References2D = -> [SectionView]
  Rotation = 0
  ScaleType = 0
  TheoreticalExact = false
  Type = 2
  UnderTolerance = 0
  X = 13.592
  Y = 47.9705
FEATURE [TechDraw::DrawViewDimension] Dimension014
  AngleOverride = false
  Arbitrary = false
  ArbitraryTolerances = false
  EqualTolerance = true
  ExtensionAngle = 0
  FormatSpec = %.2w
  FormatSpecOverTolerance = %+.2w
  FormatSpecUnderTolerance = %+.2w
  Inverted = false
  LineAngle = 0
  LockPosition = false
  MeasureType = 1
  OverTolerance = 0
  References2D = -> [ProjItem002]
  Rotation = 0
  ScaleType = 0
  TheoreticalExact = false
  Type = 1
  UnderTolerance = 0
  X = -0.474718
  Y = 10.9185
FEATURE [TechDraw::DrawViewDimension] Dimension015
  AngleOverride = false
  Arbitrary = false
  ArbitraryTolerances = false
  EqualTolerance = true
  ExtensionAngle = 0
  FormatSpec = %.2w
  FormatSpecOverTolerance = %+.2w
  FormatSpecUnderTolerance = %+.2w
  Inverted = false
  LineAngle = 0
  LockPosition = false
  MeasureType = 1
  OverTolerance = 0
  References2D = -> [ProjItem002]
  Rotation = 0
  ScaleType = 0
  TheoreticalExact = false
  Type = 2
  UnderTolerance = 0
  X = -65.4543
  Y = 12.2317
FEATURE [TechDraw::DrawViewAnnotation] Annotation
  Font = osifont
  LineSpace = 80
  LockPosition = false
  MaxWidth = -1
  Rotation = 0
  ScaleType = 0
  Text = Ring with 8x 4.3mm through holes | (for M4 threaded rods passing | through). Ring is 5mm thick, | two beams crossing, beams are | 3mm thick and have 4x M3 threads
  TextSize = 5
  TextStyle = 0
  X = 241.195
  Y = 166.934
FEATURE [TechDraw::DrawPage] Page
  KeepUpdated = true
  NextBalloonIndex = 1
  ProjectionType = 0
  Template = -> Template
  Views = -> [ProjGroup,SectionView,Dimension,Dimension001,Dimension002,Dimension003,Dimension004,Dimension005,Dimension006,Dimension007,Dimension008,Dimension009,Dimension010,Dimension011,Dimension012,Dimension013,Dimension014,Dimension015,Annotation]
FEATURE [TechDraw::DrawSVGTemplate] Template001
  EditableTexts = Designed_by_Name=Thomas Spielauer; FC-Date=2023-11-15; FC-SC=mm; FC-SH=1/1; FC-Title=XL30 Attachment Base Ring; Subtitle=Base ring for stability
  Height = 210
  Orientation = 1
  Width = 297
FEATURE [TechDraw::DrawProjGroupItem] ProjItem003  label="Front001"
  CoarseView = false
  Direction = (0,0,1)
  Focus = 100
  HardHidden = false
  IsoCount = 0
  IsoHidden = false
  IsoVisible = false
  LockPosition = true
  Perspective = false
  Rotation = 0
  RotationVector = (1,0,0)
  ScaleType = 2
  SeamHidden = false
  SeamVisible = true
  SmoothHidden = false
  SmoothVisible = true
  Source = -> [Cut001]
  Type = 0
  X = 0
  XDirection = (1,0,0)
  Y = 0
FEATURE [TechDraw::DrawProjGroupItem] ProjItem004  label="Left"
  CoarseView = false
  Direction = (-1,0,1e-16)
  Focus = 100
  HardHidden = false
  IsoCount = 0
  IsoHidden = false
  IsoVisible = false
  LockPosition = false
  Perspective = false
  Rotation = 0
  RotationVector = (1,0,0)
  ScaleType = 2
  SeamHidden = false
  SeamVisible = true
  SmoothHidden = false
  SmoothVisible = true
  Source = -> [Cut001]
  Type = 1
  X = 87.2041
  XDirection = (1e-16,0,1)
  Y = 0
FEATURE [TechDraw::DrawProjGroup] ProjGroup001
  Anchor = -> ProjItem003
  AutoDistribute = true
  LockPosition = false
  ProjectionType = 0
  Rotation = 0
  ScaleType = 0
  Source = -> [Cut001]
  Views = -> [ProjItem003,ProjItem004]
  X = 98.0508
  Y = 130.02
  spacingX = 15
  spacingY = 15
FEATURE [TechDraw::DrawViewDimension] Dimension016
  AngleOverride = false
  Arbitrary = false
  ArbitraryTolerances = false
  EqualTolerance = true
  ExtensionAngle = 0
  FormatSpec = ⌀%.2w
  FormatSpecOverTolerance = %+.2w
  FormatSpecUnderTolerance = %+.2w
  Inverted = false
  LineAngle = 0
  LockPosition = false
  MeasureType = 1
  OverTolerance = 0
  References2D = -> [ProjItem003]
  Rotation = 0
  ScaleType = 0
  TheoreticalExact = false
  Type = 5
  UnderTolerance = 0
  X = 30.1616
  Y = 3.90021
FEATURE [TechDraw::DrawViewDimension] Dimension017
  AngleOverride = false
  Arbitrary = false
  ArbitraryTolerances = false
  EqualTolerance = true
  ExtensionAngle = 0
  FormatSpec = ⌀%.2w
  FormatSpecOverTolerance = %+.2w
  FormatSpecUnderTolerance = %+.2w
  Inverted = false
  LineAngle = 0
  LockPosition = false
  MeasureType = 1
  OverTolerance = 0
  References2D = -> [ProjItem003]
  Rotation = 0
  ScaleType = 0
  TheoreticalExact = false
  Type = 5
  UnderTolerance = 0
  X = 25.7414
  Y = 11.9606
FEATURE [TechDraw::DrawViewDimension] Dimension018
  AngleOverride = false
  Arbitrary = false
  ArbitraryTolerances = false
  EqualTolerance = true
  ExtensionAngle = 0
  FormatSpec = ⌀%.2w
  FormatSpecOverTolerance = %+.2w
  FormatSpecUnderTolerance = %+.2w
  Inverted = false
  LineAngle = 0
  LockPosition = false
  MeasureType = 1
  OverTolerance = 0
  References2D = -> [ProjItem003]
  Rotation = 0
  ScaleType = 0
  TheoreticalExact = false
  Type = 5
  UnderTolerance = 0
  X = -12.5673
  Y = 35.3185
FEATURE [TechDraw::DrawViewDimension] Dimension019
  AngleOverride = false
  Arbitrary = false
  ArbitraryTolerances = false
  EqualTolerance = true
  ExtensionAngle = 0
  FormatSpec = ⌀%.2w (8x)
  FormatSpecOverTolerance = %+.2w
  FormatSpecUnderTolerance = %+.2w
  Inverted = false
  LineAngle = 0
  LockPosition = false
  MeasureType = 1
  OverTolerance = 0
  References2D = -> [ProjItem003]
  Rotation = 0
  ScaleType = 0
  TheoreticalExact = false
  Type = 5
  UnderTolerance = 0
  X = 56.1196
  Y = 45.9358
FEATURE [TechDraw::DrawViewDimension] Dimension020
  AngleOverride = false
  Arbitrary = false
  ArbitraryTolerances = false
  EqualTolerance = true
  ExtensionAngle = 0
  FormatSpec = %.2w
  FormatSpecOverTolerance = %+.2w
  FormatSpecUnderTolerance = %+.2w
  Inverted = false
  LineAngle = 0
  LockPosition = false
  MeasureType = 1
  OverTolerance = 0
  References2D = -> [ProjItem004]
  Rotation = 0
  ScaleType = 0
  TheoreticalExact = false
  Type = 1
  UnderTolerance = 0
  X = 16.1
  Y = 67.274
FEATURE [TechDraw::DrawViewDimension] Dimension021
  AngleOverride = false
  Arbitrary = false
  ArbitraryTolerances = false
  EqualTolerance = true
  ExtensionAngle = 0
  FormatSpec = %.2w
  FormatSpecOverTolerance = %+.2w
  FormatSpecUnderTolerance = %+.2w
  Inverted = false
  LineAngle = 0
  LockPosition = false
  MeasureType = 1
  OverTolerance = 0
  References2D = -> [ProjItem004]
  Rotation = 0
  ScaleType = 0
  TheoreticalExact = false
  Type = 2
  UnderTolerance = 0
  X = -13.2256
  Y = 1.37674
FEATURE [TechDraw::DrawViewDimension] Dimension022
  AngleOverride = false
  Arbitrary = false
  ArbitraryTolerances = false
  EqualTolerance = true
  ExtensionAngle = 0
  FormatSpec = %.2w
  FormatSpecOverTolerance = %+.2w
  FormatSpecUnderTolerance = %+.2w
  Inverted = false
  LineAngle = 0
  LockPosition = false
  MeasureType = 1
  OverTolerance = 0
  References2D = -> [ProjItem003]
  Rotation = 0
  ScaleType = 0
  TheoreticalExact = false
  Type = 6
  UnderTolerance = 0
  X = -55.542
  Y = 41.3005
FEATURE [TechDraw::DrawPage] Page001
  KeepUpdated = true
  NextBalloonIndex = 1
  ProjectionType = 0
  Template = -> Template001
  Views = -> [ProjGroup001,Dimension016,Dimension017,Dimension018,Dimension019,Dimension020,Dimension021,Dimension022]
note: 2 file-system paths scrubbed to <path> (originals preserved in the JSON sidecar)
---- part XL30ColumnOutline.FCStd = doc fcstd_ae5e7ff6ad4c ----
FCSTD DOCUMENT  (FreeCAD 0.20R)
Label: XL30ColumnOutline
License: All rights reserved
LicenseURL: http://en.wikipedia.org/wiki/All_rights_reserved
objects: Part::Cylinder×18, Part::Compound×17, Part::MultiFuse×11, Part::Box×8, Part::FeaturePython×8, Part::Cone×2, Part::Cut×2
note: 66 computed .brp shape members not serialized (recipe doc carries the construction recipe); baked Part::Feature solids carry a one-line shape summary decoded from their .brp

FEATURE [Part::Cylinder] Cylinder
  Angle = 360
  AttacherType = Attacher::AttachEngine3D
  FirstAngle = 0
  Height = 15
  Placement = pos=(0,0,20) rot=(0,0,1;0rad)
  Radius = 75
  SecondAngle = 0
FEATURE [Part::Cylinder] Cylinder001
  Angle = 360
  AttacherType = Attacher::AttachEngine3D
  FirstAngle = 0
  Height = 60
  Placement = pos=(0,0,-40) rot=(0,0,1;0rad)
  Radius = 50
  SecondAngle = 0
FEATURE [Part::Cone] Cone
  Angle = 360
  AttacherType = Attacher::AttachEngine3D
  Height = 42
  Placement = pos=(0,0,-82) rot=(0,0,1;0rad)
  Radius1 = 26.5
  Radius2 = 50
FEATURE [Part::Cone] Cone001
  Angle = 360
  AttacherType = Attacher::AttachEngine3D
  Height = 20
  Placement = pos=(0,0,-102) rot=(0,0,1;0rad)
  Radius1 = 6.5
  Radius2 = 26.5
FEATURE [Part::MultiFuse] Fusion  label="OuterShell"
  Shapes = -> [Cylinder,Cylinder001,Cone,Cone001]
FEATURE [Part::Cylinder] Cylinder002
  Angle = 360
  AttacherType = Attacher::AttachEngine3D
  FirstAngle = 0
  Height = 15
  Placement = pos=(47.5,0,0) rot=(0,0,1;0rad)
  Radius = 4
  SecondAngle = 0
FEATURE [Part::Box] Box  label="Cube"
  AttacherType = Attacher::AttachEngine3D
  Height = 15
  Length = 10
  Placement = pos=(47.5,-4,0) rot=(0,0,1;0rad)
  Width = 8
FEATURE [Part::MultiFuse] Fusion001
  Shapes = -> [Cylinder002,Box]
FEATURE [Part::Box] Box001  label="Cube001"
  AttacherType = Attacher::AttachEngine3D
  Height = 15
  Length = 10
  Placement = pos=(47.5,-4,0) rot=(0,0,1;0rad)
  Width = 8
FEATURE [Part::Cylinder] Cylinder003
  Angle = 360
  AttacherType = Attacher::AttachEngine3D
  FirstAngle = 0
  Height = 15
  Placement = pos=(47.5,0,0) rot=(0,0,1;0rad)
  Radius = 4
  SecondAngle = 0
FEATURE [Part::MultiFuse] Fusion002
  Placement = pos=(0,0,0) rot=(0,0,1;0.785398rad)
  Shapes = -> [Cylinder003,Box001]
FEATURE [Part::Box] Box002  label="Cube002"
  AttacherType = Attacher::AttachEngine3D
  Height = 15
  Length = 10
  Placement = pos=(47.5,-4,0) rot=(0,0,1;0rad)
  Width = 8
FEATURE [Part::Cylinder] Cylinder004
  Angle = 360
  AttacherType = Attacher::AttachEngine3D
  FirstAngle = 0
  Height = 15
  Placement = pos=(47.5,0,0) rot=(0,0,1;0rad)
  Radius = 4
  SecondAngle = 0
FEATURE [Part::MultiFuse] Fusion003
  Placement = pos=(0,0,0) rot=(0,0,1;1.5708rad)
  Shapes = -> [Cylinder004,Box002]
FEATURE [Part::Box] Box003  label="Cube003"
  AttacherType = Attacher::AttachEngine3D
  Height = 15
  Length = 10
  Placement = pos=(47.5,-4,0) rot=(0,0,1;0rad)
  Width = 8
FEATURE [Part::Cylinder] Cylinder005
  Angle = 360
  AttacherType = Attacher::AttachEngine3D
  FirstAngle = 0
  Height = 15
  Placement = pos=(47.5,0,0) rot=(0,0,1;0rad)
  Radius = 4
  SecondAngle = 0
FEATURE [Part::MultiFuse] Fusion004
  Placement = pos=(0,0,0) rot=(0,0,1;2.35619rad)
  Shapes = -> [Cylinder005,Box003]
FEATURE [Part::Box] Box004  label="Cube004"
  AttacherType = Attacher::AttachEngine3D
  Height = 15
  Length = 10
  Placement = pos=(47.5,-4,0) rot=(0,0,1;0rad)
  Width = 8
FEATURE [Part::Cylinder] Cylinder006
  Angle = 360
  AttacherType = Attacher::AttachEngine3D
  FirstAngle = 0
  Height = 15
  Placement = pos=(47.5,0,0) rot=(0,0,1;0rad)
  Radius = 4
  SecondAngle = 0
FEATURE [Part::MultiFuse] Fusion005
  Placement = pos=(0,0,0) rot=(0,0,1;3.14159rad)
  Shapes = -> [Cylinder006,Box004]
FEATURE [Part::Box] Box005  label="Cube005"
  AttacherType = Attacher::AttachEngine3D
  Height = 15
  Length = 10
  Placement = pos=(47.5,-4,0) rot=(0,0,1;0rad)
  Width = 8
FEATURE [Part::Cylinder] Cylinder007
  Angle = 360
  AttacherType = Attacher::AttachEngine3D
  FirstAngle = 0
  Height = 15
  Placement = pos=(47.5,0,0) rot=(0,0,1;0rad)
  Radius = 4
  SecondAngle = 0
FEATURE [Part::MultiFuse] Fusion006
  Placement = pos=(0,0,0) rot=(0,0,1;3.92699rad)
  Shapes = -> [Cylinder007,Box005]
FEATURE [Part::Box] Box006  label="Cube006"
  AttacherType = Attacher::AttachEngine3D
  Height = 15
  Length = 10
  Placement = pos=(47.5,-4,0) rot=(0,0,1;0rad)
  Width = 8
FEATURE [Part::Cylinder] Cylinder008
  Angle = 360
  AttacherType = Attacher::AttachEngine3D
  FirstAngle = 0
  Height = 15
  Placement = pos=(47.5,0,0) rot=(0,0,1;0rad)
  Radius = 4
  SecondAngle = 0
FEATURE [Part::MultiFuse] Fusion007
  Placement = pos=(0,0,0) rot=(0,0,1;4.71239rad)
  Shapes = -> [Cylinder008,Box006]
FEATURE [Part::Box] Box007  label="Cube007"
  AttacherType = Attacher::AttachEngine3D
  Height = 15
  Length = 10
  Placement = pos=(47.5,-4,0) rot=(0,0,1;0rad)
  Width = 8
FEATURE [Part::Cylinder] Cylinder009
  Angle = 360
  AttacherType = Attacher::AttachEngine3D
  FirstAngle = 0
  Height = 15
  Placement = pos=(47.5,0,0) rot=(0,0,1;0rad)
  Radius = 4
  SecondAngle = 0
FEATURE [Part::MultiFuse] Fusion008
  Placement = pos=(0,0,0) rot=(0,0,1;5.49779rad)
  Shapes = -> [Cylinder009,Box007]
FEATURE [Part::MultiFuse] Fusion009  label="CutsForScrews"
  Placement = pos=(0,0,-50) rot=(0,0,1;0rad)
  Shapes = -> [Fusion008,Fusion001,Fusion002,Fusion003,Fusion004,Fusion005,Fusion006,Fusion007]
FEATURE [Part::Cut] Cut
  Base = -> Fusion
  Tool = -> Fusion009
FEATURE [Part::Cylinder] Cylinder017
  Angle = 360
  AttacherType = Attacher::AttachEngine3D
  FirstAngle = 0
  Height = 10
  Placement = pos=(47.5,0,0) rot=(0,0,1;5.49779rad)
  Radius = 1.25
  SecondAngle = 0
FEATURE [Part::Compound] Compound
  Links = -> [Cylinder017]
FEATURE [Part::Cylinder] Cylinder018
  Angle = 360
  AttacherType = Attacher::AttachEngine3D
  FirstAngle = 0
  Height = 10
  Placement = pos=(47.5,0,0) rot=(0,0,-1;0.785398rad)
  Radius = 1.25
  SecondAngle = 0
FEATURE [Part::Compound] Compound001
  Links = -> [Cylinder018]
  Placement = pos=(0,0,0) rot=(0,0,1;0.785398rad)
FEATURE [Part::Cylinder] Cylinder019
  Angle = 360
  AttacherType = Attacher::AttachEngine3D
  FirstAngle = 0
  Height = 10
  Placement = pos=(47.5,0,0) rot=(0,0,-1;0.785398rad)
  Radius = 1.25
  SecondAngle = 0
FEATURE [Part::Compound] Compound002
  Links = -> [Cylinder019]
  Placement = pos=(0,0,0) rot=(0,0,1;1.5708rad)
FEATURE [Part::Cylinder] Cylinder020
  Angle = 360
  AttacherType = Attacher::AttachEngine3D
  FirstAngle = 0
  Height = 10
  Placement = pos=(47.5,0,0) rot=(0,0,-1;0.785398rad)
  Radius = 1.25
  SecondAngle = 0
FEATURE [Part::Compound] Compound003
  Links = -> [Cylinder020]
  Placement = pos=(0,0,0) rot=(0,0,1;2.35619rad)
FEATURE [Part::Cylinder] Cylinder021
  Angle = 360
  AttacherType = Attacher::AttachEngine3D
  FirstAngle = 0
  Height = 10
  Placement = pos=(47.5,0,0) rot=(0,0,-1;0.785398rad)
  Radius = 1.25
  SecondAngle = 0
FEATURE [Part::Compound] Compound004
  Links = -> [Cylinder021]
  Placement = pos=(0,0,0) rot=(0,0,1;3.14159rad)
FEATURE [Part::Cylinder] Cylinder022
  Angle = 360
  AttacherType = Attacher::AttachEngine3D
  FirstAngle = 0
  Height = 10
  Placement = pos=(47.5,0,0) rot=(0,0,-1;0.785398rad)
  Radius = 1.25
  SecondAngle = 0
FEATURE [Part::Compound] Compound005
  Links = -> [Cylinder022]
  Placement = pos=(0,0,0) rot=(0,0,1;3.92699rad)
FEATURE [Part::Cylinder] Cylinder023
  Angle = 360
  AttacherType = Attacher::AttachEngine3D
  FirstAngle = 0
  Height = 10
  Placement = pos=(47.5,0,0) rot=(0,0,-1;0.785398rad)
  Radius = 1.25
  SecondAngle = 0
FEATURE [Part::Compound] Compound006
  Links = -> [Cylinder023]
  Placement = pos=(0,0,0) rot=(0,0,1;4.71239rad)
FEATURE [Part::Cylinder] Cylinder024
  Angle = 360
  AttacherType = Attacher::AttachEngine3D
  FirstAngle = 0
  Height = 10
  Placement = pos=(47.5,0,0) rot=(0,0,-1;0.785398rad)
  Radius = 1.25
  SecondAngle = 0
FEATURE [Part::Compound] Compound007
  Links = -> [Cylinder024]
  Placement = pos=(0,0,0) rot=(0,0,1;5.49779rad)
FEATURE [Part::MultiFuse] Fusion010  label="M3x10DrillHoles"
  Placement = pos=(0,0,-35) rot=(0,0,1;0rad)
  Shapes = -> [Compound007,Compound,Compound001,Compound002,Compound003,Compound004,Compound005,Compound006]
FEATURE [Part::Cut] Cut001  label="BasicOutline_Part0and1"
  Base = -> Cut
  Tool = -> Fusion010
FEATURE [Part::FeaturePython] Screw  label="M3x10-Screw"  # Fasteners workbench fastener (typed FeaturePython)
  Placement = pos=(47.5,0,0) rot=(0,1,0;3.14159rad)
  diameter = 4
  invert = false
  leftHanded = false
  length = 3
  lengthCustom = 10
  matchOuter = false
  offset = 0
  thread = false
  type = 48
FEATURE [Part::Compound] Compound008
  Links = -> [Screw]
FEATURE [Part::FeaturePython] Screw001  label="M3x10-Screw001"  # Fasteners workbench fastener (typed FeaturePython)
  Placement = pos=(47.5,0,0) rot=(0,1,0;3.14159rad)
  diameter = 4
  invert = false
  leftHanded = false
  length = 3
  lengthCustom = 10
  matchOuter = false
  offset = 0
  thread = false
  type = 48
FEATURE [Part::Compound] Compound009
  Links = -> [Screw001]
  Placement = pos=(0,0,0) rot=(0,0,1;0.785398rad)
FEATURE [Part::FeaturePython] Screw002  label="M3x10-Screw002"  # Fasteners workbench fastener (typed FeaturePython)
  Placement = pos=(47.5,0,0) rot=(0,1,0;3.14159rad)
  diameter = 4
  invert = false
  leftHanded = false
  length = 3
  lengthCustom = 10
  matchOuter = false
  offset = 0
  thread = false
  type = 48
FEATURE [Part::Compound] Compound010
  Links = -> [Screw002]
  Placement = pos=(0,0,0) rot=(0,0,1;1.5708rad)
FEATURE [Part::FeaturePython] Screw003  label="M3x10-Screw003"  # Fasteners workbench fastener (typed FeaturePython)
  Placement = pos=(47.5,0,0) rot=(0,1,0;3.14159rad)
  diameter = 4
  invert = false
  leftHanded = false
  length = 3
  lengthCustom = 10
  matchOuter = false
  offset = 0
  thread = false
  type = 48
FEATURE [Part::Compound] Compound011
  Links = -> [Screw003]
  Placement = pos=(0,0,0) rot=(0,0,1;2.35619rad)
FEATURE [Part::FeaturePython] Screw004  label="M3x10-Screw004"  # Fasteners workbench fastener (typed FeaturePython)
  Placement = pos=(47.5,0,0) rot=(0,1,0;3.14159rad)
  diameter = 4
  invert = false
  leftHanded = false
  length = 3
  lengthCustom = 10
  matchOuter = false
  offset = 0
  thread = false
  type = 48
FEATURE [Part::Compound] Compound012
  Links = -> [Screw004]
  Placement = pos=(0,0,0) rot=(0,0,1;3.14159rad)
FEATURE [Part::FeaturePython] Screw005  label="M3x10-Screw005"  # Fasteners workbench fastener (typed FeaturePython)
  Placement = pos=(47.5,0,0) rot=(0,1,0;3.14159rad)
  diameter = 4
  invert = false
  leftHanded = false
  length = 3
  lengthCustom = 10
  matchOuter = false
  offset = 0
  thread = false
  type = 48
FEATURE [Part::Compound] Compound013
  Links = -> [Screw005]
  Placement = pos=(0,0,0) rot=(0,0,1;3.92699rad)
FEATURE [Part::FeaturePython] Screw006  label="M3x10-Screw006"  # Fasteners workbench fastener (typed FeaturePython)
  Placement = pos=(47.5,0,0) rot=(0,1,0;3.14159rad)
  diameter = 4
  invert = false
  leftHanded = false
  length = 3
  lengthCustom = 10
  matchOuter = false
  offset = 0
  thread = false
  type = 48
FEATURE [Part::Compound] Compound014
  Links = -> [Screw006]
  Placement = pos=(0,0,0) rot=(0,0,1;4.71239rad)
FEATURE [Part::FeaturePython] Screw007  label="M3x10-Screw007"  # Fasteners workbench fastener (typed FeaturePython)
  Placement = pos=(47.5,0,0) rot=(0,1,0;3.14159rad)
  diameter = 4
  invert = false
  leftHanded = false
  length = 3
  lengthCustom = 10
  matchOuter = false
  offset = 0
  thread = false
  type = 48
FEATURE [Part::Compound] Compound015
  Links = -> [Screw007]
  Placement = pos=(0,0,0) rot=(0,0,1;5.49779rad)
FEATURE [Part::Compound] Compound016  label="8xM3x10"
  Links = -> [Compound015,Compound008,Compound009,Compound010,Compound011,Compound012,Compound013,Compound014]
  Placement = pos=(0,0,-35) rot=(0,0,1;0rad)
---- part XL30FinalAppertureHolder.FCStd = doc fcstd_09667841f401 ----
FCSTD DOCUMENT  (FreeCAD 0.20R)
Label: XL30FinalAppertureHolder
License: All rights reserved
LicenseURL: http://en.wikipedia.org/wiki/All_rights_reserved
objects: Part::Cylinder×8, Part::MultiFuse×2, Part::Cut×2, PartDesign::AdditiveCylinder×1, PartDesign::Hole×1, PartDesign::Body×1, Part::Feature×1
note: 18 computed .brp shape members not serialized (recipe doc carries the construction recipe); baked Part::Feature solids carry a one-line shape summary decoded from their .brp

FEATURE [Part::Cylinder] Cylinder  label="Zylinder"
  Angle = 360
  AttacherType = Attacher::AttachEngine3D
  FirstAngle = 0
  Height = 0.5
  Radius = 4.5
  SecondAngle = 0
FEATURE [Part::Cylinder] Cylinder001  label="Zylinder001"
  Angle = 360
  AttacherType = Attacher::AttachEngine3D
  FirstAngle = 0
  Height = 0.9
  Radius = 3.5
  SecondAngle = 0
FEATURE [Part::Cylinder] Cylinder002  label="Zylinder002"
  Angle = 360
  AttacherType = Attacher::AttachEngine3D
  FirstAngle = 0
  Height = 3.5
  Radius = 2.5
  SecondAngle = 0
FEATURE [Part::Cylinder] Cylinder003  label="Zylinder003"
  Angle = 360
  AttacherType = Attacher::AttachEngine3D
  FirstAngle = 0
  Height = 4
  Placement = pos=(0,0,3.5) rot=(0,0,1;0rad)
  Radius = 2.4
  SecondAngle = 0
FEATURE [Part::Cylinder] Cylinder004  label="Zylinder004"
  Angle = 360
  AttacherType = Attacher::AttachEngine3D
  FirstAngle = 0
  Height = 10
  Radius = 1.87
  SecondAngle = 0
FEATURE [Part::MultiFuse] Fusion
  Shapes = -> [Cylinder004,Cylinder,Cylinder001,Cylinder002,Cylinder003]
FEATURE [Part::Cylinder] Cylinder005  label="Zylinder005"
  Angle = 360
  AttacherType = Attacher::AttachEngine3D
  FirstAngle = 0
  Height = 100
  Radius = 1.2
  SecondAngle = 0
FEATURE [Part::Cylinder] Cylinder006  label="Zylinder006"
  Angle = 360
  AttacherType = Attacher::AttachEngine3D
  FirstAngle = 0
  Height = 7
  Radius = 2
  SecondAngle = 0
FEATURE [Part::Cylinder] Cylinder007  label="Zylinder007"
  Angle = 360
  AttacherType = Attacher::AttachEngine3D
  FirstAngle = 0
  Height = 10
  Placement = pos=(0,0,8) rot=(0,0,1;0rad)
  Radius = 1.5
  SecondAngle = 0
FEATURE [Part::MultiFuse] Fusion001
  Shapes = -> [Cylinder007,Cylinder005,Cylinder006]
FEATURE [Part::Cut] Cut
  Base = -> Fusion
  Tool = -> Fusion001
FEATURE [PartDesign::AdditiveCylinder] Cylinder008
  Angle = 360
  AttacherType = Attacher::AttachEngine3D
  FirstAngle = 0
  Height = 4
  Radius = 3
  SecondAngle = 0
FEATURE [PartDesign::Hole] Hole
  BaseFeature = -> Cylinder008
  CustomThreadClearance = 0
  Depth = 18.9163
  DepthType = 0
  Diameter = 4.224
  DrillForDepth = false
  DrillPoint = 1
  DrillPointAngle = 118
  HoleCutCountersinkAngle = 90
  HoleCutCustomValues = false
  HoleCutDepth = 0
  HoleCutDiameter = 6.1
  HoleCutType = 0
  ModelThread = true
  Profile = -> Cylinder008 [Face3]
  Tapered = false
  TaperedAngle = 90
  ThreadClass = 0
  ThreadDepth = 18.9163
  ThreadDepthType = 0
  ThreadDirection = 0
  ThreadFit = 0
  ThreadSize = 13
  ThreadType = 1
  Threaded = true
  UseCustomThreadClearance = false
FEATURE [PartDesign::Body] Body  label="ThreadCutterM3"
  Group = -> [Cylinder008,Hole]
  Origin = -> Origin
  Placement = pos=(0,0,3.5) rot=(0,0,1;0rad)
  Tip = -> Hole
FEATURE [Part::Cut] Cut001
  Base = -> Cut
  Tool = -> Body
FEATURE [Part::Feature] Cut001_solid  label="XL30FinalAppertureHolder"
  shape: bbox 9 x 9 x 10 mm, 44 faces (baked)
---- part XL30Frontdoor_Flanges01.FCStd = doc fcstd_f63b15750c71 (73739 chars; too large to inline — full recipe in that document) ----
---- part XL30MainChamberModel.FCStd = doc fcstd_1d90293a0cdb ----
FCSTD DOCUMENT  (FreeCAD 0.20R)
Label: XL30MainChamberModel
License: All rights reserved
LicenseURL: http://en.wikipedia.org/wiki/All_rights_reserved
objects: Part::Cylinder×49, Part::Cut×21, Part::Compound×17, Part::MultiFuse×8, Part::Box×7, Part::Sphere×1
note: 103 computed .brp shape members not serialized (recipe doc carries the construction recipe); baked Part::Feature solids carry a one-line shape summary decoded from their .brp

FEATURE [Part::Box] Box  label="Würfel"
  AttacherType = Attacher::AttachEngine3D
  Height = 330
  Length = 330
  Width = 180
FEATURE [Part::Cylinder] Cylinder  label="Zylinder"
  Angle = 360
  AttacherType = Attacher::AttachEngine3D
  FirstAngle = 0
  Height = 180
  Placement = pos=(165,180,165) rot=(1,0,0;1.5708rad)
  Radius = 142
  SecondAngle = 0
FEATURE [Part::Cut] Cut
  Base = -> Box
  Tool = -> Cylinder
FEATURE [Part::Box] Box001  label="Würfel001"
  AttacherType = Attacher::AttachEngine3D
  Height = 50
  Length = 70
  Placement = pos=(0,0,265) rot=(0,-1,0;1.20428rad)
  Width = 180
FEATURE [Part::Cut] Cut001
  Base = -> Cut
  Tool = -> Box001
FEATURE [Part::Cylinder] Cylinder001  label="Flange100Right_Hole"
  Angle = 360
  AttacherType = Attacher::AttachEngine3D
  FirstAngle = 0
  Height = 50
  Placement = pos=(284,107.5,198.5) rot=(0,1,0;1.5708rad)
  Radius = 34.5
  SecondAngle = 0
FEATURE [Part::Cylinder] Cylinder002  label="Flange100Right_Recess"
  Angle = 360
  AttacherType = Attacher::AttachEngine3D
  FirstAngle = 0
  Height = 1
  Placement = pos=(329,107.5,198.5) rot=(0,1,0;1.5708rad)
  Radius = 51.5
  SecondAngle = 0
FEATURE [Part::Cylinder] Cylinder003  label="Zylinder001"
  Angle = 360
  AttacherType = Attacher::AttachEngine3D
  FirstAngle = 0
  Height = 3
  Radius = 41
  SecondAngle = 0
FEATURE [Part::Cylinder] Cylinder004  label="Zylinder002"
  Angle = 360
  AttacherType = Attacher::AttachEngine3D
  FirstAngle = 0
  Height = 3
  Radius = 37
  SecondAngle = 0
FEATURE [Part::Cut] Cut002
  Base = -> Cylinder003
  Placement = pos=(326,107.5,198.5) rot=(0,1,0;1.5708rad)
  Tool = -> Cylinder004
FEATURE [Part::Cylinder] Cylinder005  label="Zylinder003"
  Angle = 360
  AttacherType = Attacher::AttachEngine3D
  FirstAngle = 0
  Height = 10
  Placement = pos=(0,0,-44.3) rot=(0,1,0;1.5708rad)
  Radius = 1.65
  SecondAngle = 0
FEATURE [Part::Cylinder] Cylinder006  label="Zylinder004"
  Angle = 360
  AttacherType = Attacher::AttachEngine3D
  FirstAngle = 0
  Height = 10
  Placement = pos=(0,0,-44.3) rot=(0,1,0;1.5708rad)
  Radius = 1.65
  SecondAngle = 0
FEATURE [Part::Cylinder] Cylinder007  label="Zylinder005"
  Angle = 360
  AttacherType = Attacher::AttachEngine3D
  FirstAngle = 0
  Height = 10
  Placement = pos=(0,0,-44.3) rot=(0,1,0;1.5708rad)
  Radius = 1.65
  SecondAngle = 0
FEATURE [Part::Compound] Compound001
  Links = -> [Cylinder006]
  Placement = pos=(0,0,0) rot=(1,0,0;2.0944rad)
FEATURE [Part::Compound] Compound002
  Links = -> [Cylinder007]
  Placement = pos=(0,0,0) rot=(1,0,0;4.18879rad)
FEATURE [Part::Compound] Compound003  label="M4 holes flange right"
  Links = -> [Cylinder005,Compound001,Compound002]
  Placement = pos=(319,107.5,198.5) rot=(0,0,1;0rad)
FEATURE [Part::MultiFuse] Fusion
  Shapes = -> [Cylinder001,Cylinder002,Cut002,Compound003]
FEATURE [Part::Cut] Cut003
  Base = -> Cut001
  Tool = -> Fusion
FEATURE [Part::Cylinder] Cylinder008  label="Flange120LeftLow_Recess"
  Angle = 360
  AttacherType = Attacher::AttachEngine3D
  FirstAngle = 0
  Height = 1
  Placement = pos=(0,0,-1) rot=(0,0,1;0rad)
  Radius = 61.5
  SecondAngle = 0
FEATURE [Part::Cylinder] Cylinder009  label="Zylinder006"
  Angle = 360
  AttacherType = Attacher::AttachEngine3D
  FirstAngle = 0
  Height = 60
  Placement = pos=(0,0,-45) rot=(0,0,1;0rad)
  Radius = 45
  SecondAngle = 0
FEATURE [Part::Cylinder] Cylinder010  label="Zylinder007"
  Angle = 360
  AttacherType = Attacher::AttachEngine3D
  FirstAngle = 0
  Height = 2
  Placement = pos=(0,0,-3) rot=(0,0,1;0rad)
  Radius = 50
  SecondAngle = 0
FEATURE [Part::Cylinder] Cylinder011  label="Zylinder008"
  Angle = 360
  AttacherType = Attacher::AttachEngine3D
  FirstAngle = 0
  Height = 2
  Placement = pos=(0,0,-3) rot=(0,0,1;0rad)
  Radius = 46
  SecondAngle = 0
FEATURE [Part::Cut] Cut004
  Base = -> Cylinder010
  Tool = -> Cylinder011
FEATURE [Part::Cylinder] Cylinder012  label="Zylinder009"
  Angle = 360
  AttacherType = Attacher::AttachEngine3D
  FirstAngle = 0
  Height = 10
  Placement = pos=(54.5,0,-10) rot=(0,0,1;0rad)
  Radius = 2.5
  SecondAngle = 0
FEATURE [Part::Cylinder] Cylinder013  label="Zylinder010"
  Angle = 360
  AttacherType = Attacher::AttachEngine3D
  FirstAngle = 0
  Height = 10
  Placement = pos=(54.5,0,-10) rot=(0,0,1;0rad)
  Radius = 2.5
  SecondAngle = 0
FEATURE [Part::Cylinder] Cylinder015  label="Zylinder012"
  Angle = 360
  AttacherType = Attacher::AttachEngine3D
  FirstAngle = 0
  Height = 10
  Placement = pos=(54.5,0,-10) rot=(0,0,1;0rad)
  Radius = 2.5
  SecondAngle = 0
FEATURE [Part::Compound] Compound
  Links = -> [Cylinder013]
  Placement = pos=(0,0,0) rot=(0,0,1;2.0944rad)
FEATURE [Part::Compound] Compound004
  Links = -> [Cylinder015]
  Placement = pos=(0,0,0) rot=(0,0,1;4.18879rad)
FEATURE [Part::MultiFuse] Fusion001  label="Flange120LeftLow"
  Placement = pos=(0,115.5,140) rot=(0,-1,0;1.5708rad)
  Shapes = -> [Cylinder008,Cylinder009,Cut004,Cylinder012,Compound,Compound004]
FEATURE [Part::Cut] Cut005
  Base = -> Cut003
  Tool = -> Fusion001
FEATURE [Part::Cylinder] Cylinder016  label="Zylinder013"
  Angle = 360
  AttacherType = Attacher::AttachEngine3D
  FirstAngle = 0
  Height = 100
  Placement = pos=(0,0,0) rot=(0,1,0;1.5708rad)
  Radius = 27
  SecondAngle = 0
FEATURE [Part::Cylinder] Cylinder017  label="Zylinder014"
  Angle = 360
  AttacherType = Attacher::AttachEngine3D
  FirstAngle = 0
  Height = 100
  Placement = pos=(-99,0,0) rot=(0,1,0;1.5708rad)
  Radius = 51.5
  SecondAngle = 0
FEATURE [Part::Cylinder] Cylinder018  label="Zylinder015"
  Angle = 360
  AttacherType = Attacher::AttachEngine3D
  FirstAngle = 0
  Height = 2
  Radius = 41
  SecondAngle = 0
FEATURE [Part::Cylinder] Cylinder019  label="Zylinder016"
  Angle = 360
  AttacherType = Attacher::AttachEngine3D
  FirstAngle = 0
  Height = 2
  Radius = 37
  SecondAngle = 0
FEATURE [Part::Cut] Cut006
  Base = -> Cylinder018
  Placement = pos=(1,0,0) rot=(0,1,0;1.5708rad)
  Tool = -> Cylinder019
FEATURE [Part::Cylinder] Cylinder020  label="Zylinder017"
  Angle = 360
  AttacherType = Attacher::AttachEngine3D
  FirstAngle = 0
  Height = 10
  Placement = pos=(0,0,-44.5) rot=(0,1,0;1.5708rad)
  Radius = 3.3
  SecondAngle = 0
FEATURE [Part::Cylinder] Cylinder021  label="Zylinder018"
  Angle = 360
  AttacherType = Attacher::AttachEngine3D
  FirstAngle = 0
  Height = 10
  Placement = pos=(0,0,-44.5) rot=(0,1,0;1.5708rad)
  Radius = 3.3
  SecondAngle = 0
FEATURE [Part::Cylinder] Cylinder022  label="Zylinder019"
  Angle = 360
  AttacherType = Attacher::AttachEngine3D
  FirstAngle = 0
  Height = 10
  Placement = pos=(0,0,-44.5) rot=(0,1,0;1.5708rad)
  Radius = 3.3
  SecondAngle = 0
FEATURE [Part::Compound] Compound005
  Links = -> [Cylinder021]
  Placement = pos=(0,0,0) rot=(1,0,0;2.0944rad)
FEATURE [Part::Compound] Compound006
  Links = -> [Cylinder022]
  Placement = pos=(0,0,0) rot=(1,0,0;4.18879rad)
FEATURE [Part::MultiFuse] Fusion002  label="FlangeSEDetector"
  Placement = pos=(18,116,275) rot=(0,1,0;0.340339rad)
  Shapes = -> [Cylinder016,Cylinder017,Cut006,Cylinder020,Compound005,Compound006]
FEATURE [Part::Cut] Cut007
  Base = -> Cut005
  Tool = -> Fusion002
FEATURE [Part::Cylinder] Cylinder023  label="ODPHoleNoFlange"
  Angle = 360
  AttacherType = Attacher::AttachEngine3D
  FirstAngle = 0
  Height = 50
  Placement = pos=(125,140,0) rot=(0,0,1;0rad)
  Radius = 40
  SecondAngle = 0
FEATURE [Part::Cut] Cut008
  Base = -> Cut007
  Tool = -> Cylinder023
FEATURE [Part::Cylinder] Cylinder024  label="EGunHoleWithoutFlange"
  Angle = 360
  AttacherType = Attacher::AttachEngine3D
  FirstAngle = 0
  Height = 50
  Placement = pos=(165,120,280) rot=(0,0,1;0rad)
  Radius = 50
  SecondAngle = 0
FEATURE [Part::Cut] Cut009  label="FrontChamber"
  Base = -> Cut008
  Tool = -> Cylinder024
FEATURE [Part::Box] Box002  label="Würfel002"
  AttacherType = Attacher::AttachEngine3D
  Height = 330
  Length = 330
  Width = 105
FEATURE [Part::Box] Box003  label="Würfel003"
  AttacherType = Attacher::AttachEngine3D
  Height = 330
  Length = 150
  Placement = pos=(330,0,0) rot=(0,0,1;0.785398rad)
  Width = 200
FEATURE [Part::Box] Box004  label="Würfel004"
  AttacherType = Attacher::AttachEngine3D
  Height = 150
  Length = 240
  Placement = pos=(90,0,330) rot=(-1,0,0;0.785398rad)
  Width = 150
FEATURE [Part::Box] Box005  label="Würfel005"
  AttacherType = Attacher::AttachEngine3D
  Height = 330
  Length = 150
  Placement = pos=(0,15,0) rot=(0,0,1;0.785398rad)
  Width = 100
FEATURE [Part::Box] Box007  label="Würfel007"
  AttacherType = Attacher::AttachEngine3D
  Height = 50
  Length = 70
  Placement = pos=(0,0,265) rot=(0,-1,0;1.20428rad)
  Width = 180
FEATURE [Part::MultiFuse] Fusion003
  Shapes = -> [Box005,Box003,Box004,Box007]
FEATURE [Part::Cut] Cut010
  Base = -> Box002
  Placement = pos=(0,180,0) rot=(0,0,1;0rad)
  Tool = -> Fusion003
FEATURE [Part::Cylinder] Cylinder025  label="Zylinder020"
  Angle = 360
  AttacherType = Attacher::AttachEngine3D
  FirstAngle = 0
  Height = 100
  Placement = pos=(0,0,0) rot=(0,1,0;1.5708rad)
  Radius = 27
  SecondAngle = 0
FEATURE [Part::Cylinder] Cylinder026  label="Zylinder021"
  Angle = 360
  AttacherType = Attacher::AttachEngine3D
  FirstAngle = 0
  Height = 100
  Placement = pos=(-99,0,0) rot=(0,1,0;1.5708rad)
  Radius = 51.5
  SecondAngle = 0
FEATURE [Part::Cylinder] Cylinder027  label="Zylinder022"
  Angle = 360
  AttacherType = Attacher::AttachEngine3D
  FirstAngle = 0
  Height = 2
  Radius = 41
  SecondAngle = 0
FEATURE [Part::Cylinder] Cylinder028  label="Zylinder023"
  Angle = 360
  AttacherType = Attacher::AttachEngine3D
  FirstAngle = 0
  Height = 2
  Radius = 37
  SecondAngle = 0
FEATURE [Part::Cut] Cut011
  Base = -> Cylinder027
  Placement = pos=(1,0,0) rot=(0,1,0;1.5708rad)
  Tool = -> Cylinder028
FEATURE [Part::Cylinder] Cylinder029  label="Zylinder024"
  Angle = 360
  AttacherType = Attacher::AttachEngine3D
  FirstAngle = 0
  Height = 10
  Placement = pos=(0,0,-44.5) rot=(0,1,0;1.5708rad)
  Radius = 3.3
  SecondAngle = 0
FEATURE [Part::Cylinder] Cylinder030  label="Zylinder025"
  Angle = 360
  AttacherType = Attacher::AttachEngine3D
  FirstAngle = 0
  Height = 10
  Placement = pos=(0,0,-44.5) rot=(0,1,0;1.5708rad)
  Radius = 3.3
  SecondAngle = 0
FEATURE [Part::Compound] Compound007
  Links = -> [Cylinder030]
  Placement = pos=(0,0,0) rot=(1,0,0;2.0944rad)
FEATURE [Part::Cylinder] Cylinder031  label="Zylinder026"
  Angle = 360
  AttacherType = Attacher::AttachEngine3D
  FirstAngle = 0
  Height = 10
  Placement = pos=(0,0,-44.5) rot=(0,1,0;1.5708rad)
  Radius = 3.3
  SecondAngle = 0
FEATURE [Part::Compound] Compound008
  Links = -> [Cylinder031]
  Placement = pos=(0,0,0) rot=(1,0,0;4.18879rad)
FEATURE [Part::MultiFuse] Fusion004  label="BSEFlange"
  Placement = pos=(278.7,231.3,105) rot=(0,0,1;3.92699rad)
  Shapes = -> [Cylinder025,Cylinder026,Cut011,Cylinder029,Compound007,Compound008]
FEATURE [Part::Compound] Compound009  label="BSEFlange1"
  Links = -> [Fusion004]
FEATURE [Part::Cut] Cut012
  Base = -> Cut010
  Tool = -> Compound009
FEATURE [Part::Cylinder] Cylinder032  label="Zylinder027"
  Angle = 360
  AttacherType = Attacher::AttachEngine3D
  FirstAngle = 0
  Height = 100
  Placement = pos=(0,0,0) rot=(0,1,0;1.5708rad)
  Radius = 20
  SecondAngle = 0
FEATURE [Part::Cylinder] Cylinder033  label="Zylinder028"
  Angle = 360
  AttacherType = Attacher::AttachEngine3D
  FirstAngle = 0
  Height = 100
  Placement = pos=(-99,0,0) rot=(0,1,0;1.5708rad)
  Radius = 44
  SecondAngle = 0
FEATURE [Part::Cylinder] Cylinder034  label="Zylinder029"
  Angle = 360
  AttacherType = Attacher::AttachEngine3D
  FirstAngle = 0
  Height = 2
  Radius = 33.8
  SecondAngle = 0
FEATURE [Part::Cylinder] Cylinder035  label="Zylinder030"
  Angle = 360
  AttacherType = Attacher::AttachEngine3D
  FirstAngle = 0
  Height = 2
  Radius = 30
  SecondAngle = 0
FEATURE [Part::Cut] Cut013
  Base = -> Cylinder034
  Placement = pos=(1,0,0) rot=(0,1,0;1.5708rad)
  Tool = -> Cylinder035
FEATURE [Part::Cylinder] Cylinder036  label="Zylinder031"
  Angle = 360
  AttacherType = Attacher::AttachEngine3D
  FirstAngle = 0
  Height = 10
  Placement = pos=(0,0,-37.5) rot=(0,1,0;1.5708rad)
  Radius = 3.3
  SecondAngle = 0
FEATURE [Part::Cylinder] Cylinder037  label="Zylinder032"
  Angle = 360
  AttacherType = Attacher::AttachEngine3D
  FirstAngle = 0
  Height = 10
  Placement = pos=(0,0,-37.5) rot=(0,1,0;1.5708rad)
  Radius = 3.3
  SecondAngle = 0
FEATURE [Part::Compound] Compound010
  Links = -> [Cylinder037]
  Placement = pos=(0,0,0) rot=(1,0,0;2.0944rad)
FEATURE [Part::Cylinder] Cylinder038  label="Zylinder033"
  Angle = 360
  AttacherType = Attacher::AttachEngine3D
  FirstAngle = 0
  Height = 10
  Placement = pos=(0,0,-37.5) rot=(0,1,0;1.5708rad)
  Radius = 3.3
  SecondAngle = 0
FEATURE [Part::Compound] Compound011
  Links = -> [Cylinder038]
  Placement = pos=(0,0,0) rot=(1,0,0;4.18879rad)
FEATURE [Part::MultiFuse] Fusion005  label="BSEFlange003"
  Placement = pos=(0,0,0) rot=(0,0,-1;0.785398rad)
  Shapes = -> [Cylinder032,Cylinder033,Cut013,Cylinder036,Compound010,Compound011]
FEATURE [Part::Compound] Compound012  label="SideFlangeBack2Low"
  Links = -> [Fusion005]
  Placement = pos=(45,240,97.5) rot=(0,0,1;0rad)
FEATURE [Part::Cut] Cut014
  Base = -> Cut012
  Tool = -> Compound012
FEATURE [Part::Cylinder] Cylinder039  label="Zylinder034"
  Angle = 360
  AttacherType = Attacher::AttachEngine3D
  FirstAngle = 0
  Height = 110
  Placement = pos=(-20,0,20) rot=(0,1,0;2.35619rad)
  Radius = 20
  SecondAngle = 0
FEATURE [Part::Cylinder] Cylinder040  label="Zylinder035"
  Angle = 360
  AttacherType = Attacher::AttachEngine3D
  FirstAngle = 0
  Height = 100
  Placement = pos=(-99,0,0) rot=(0,1,0;1.5708rad)
  Radius = 51.5
  SecondAngle = 0
FEATURE [Part::Cylinder] Cylinder041  label="Zylinder036"
  Angle = 360
  AttacherType = Attacher::AttachEngine3D
  FirstAngle = 0
  Height = 2
  Radius = 41
  SecondAngle = 0
FEATURE [Part::Cylinder] Cylinder042  label="Zylinder037"
  Angle = 360
  AttacherType = Attacher::AttachEngine3D
  FirstAngle = 0
  Height = 2
  Radius = 37
  SecondAngle = 0
FEATURE [Part::Cut] Cut015
  Base = -> Cylinder041
  Placement = pos=(1,0,0) rot=(0,1,0;1.5708rad)
  Tool = -> Cylinder042
FEATURE [Part::Cylinder] Cylinder043  label="Zylinder038"
  Angle = 360
  AttacherType = Attacher::AttachEngine3D
  FirstAngle = 0
  Height = 10
  Placement = pos=(0,0,-44.5) rot=(0,1,0;1.5708rad)
  Radius = 3.3
  SecondAngle = 0
FEATURE [Part::Cylinder] Cylinder044  label="Zylinder039"
  Angle = 360
  AttacherType = Attacher::AttachEngine3D
  FirstAngle = 0
  Height = 10
  Placement = pos=(0,0,-44.5) rot=(0,1,0;1.5708rad)
  Radius = 3.3
  SecondAngle = 0
FEATURE [Part::Compound] Compound013
  Links = -> [Cylinder044]
  Placement = pos=(0,0,0) rot=(1,0,0;2.0944rad)
FEATURE [Part::Cylinder] Cylinder045  label="Zylinder040"
  Angle = 360
  AttacherType = Attacher::AttachEngine3D
  FirstAngle = 0
  Height = 10
  Placement = pos=(0,0,-44.5) rot=(0,1,0;1.5708rad)
  Radius = 3.3
  SecondAngle = 0
FEATURE [Part::Compound] Compound014
  Links = -> [Cylinder045]
  Placement = pos=(0,0,0) rot=(1,0,0;4.18879rad)
FEATURE [Part::MultiFuse] Fusion006  label="BSEFlange005"
  Placement = pos=(0,0,286) rot=(0,0,-1;0.785398rad)
  Shapes = -> [Cylinder039,Cylinder040,Cut015,Cylinder043,Compound013,Compound014]
FEATURE [Part::Compound] Compound015  label="BackTopFlange100"
  Links = -> [Fusion006]
  Placement = pos=(45,240,0) rot=(0,0,1;0rad)
FEATURE [Part::Cut] Cut016  label="BackChamber01"
  Base = -> Cut014
  Tool = -> Compound015
FEATURE [Part::Cylinder] Cylinder046  label="Zylinder041"
  Angle = 360
  AttacherType = Attacher::AttachEngine3D
  FirstAngle = 0
  Height = 800
  Placement = pos=(36,500,38) rot=(1,0,0;1.5708rad)
  Radius = 10
  SecondAngle = 0
FEATURE [Part::Cylinder] Cylinder047  label="Zylinder042"
  Angle = 360
  AttacherType = Attacher::AttachEngine3D
  FirstAngle = 0
  Height = 800
  Placement = pos=(302,500,34) rot=(1,0,0;1.5708rad)
  Radius = 10
  SecondAngle = 0
FEATURE [Part::Compound] Compound016
  Links = -> [Cylinder047,Cylinder046]
FEATURE [Part::Sphere] Sphere  label="Kugel"
  Angle1 = -90
  Angle2 = 90
  Angle3 = 360
  AttacherType = Attacher::AttachEngine3D
  Placement = pos=(165,0,165) rot=(0,0,1;0rad)
  Radius = 230
FEATURE [Part::Cut] Cut017
  Base = -> Cut016
  Tool = -> Sphere
FEATURE [Part::MultiFuse] Fusion007
  Shapes = -> [Cut009,Cut017]
FEATURE [Part::Cut] Cut018
  Base = -> Fusion007
  Tool = -> Compound016
FEATURE [Part::Cylinder] Cylinder048  label="Zylinder043"
  Angle = 360
  AttacherType = Attacher::AttachEngine3D
  FirstAngle = 0
  Height = 4
  Radius = 155
  SecondAngle = 0
FEATURE [Part::Cylinder] Cylinder049  label="Zylinder044"
  Angle = 360
  AttacherType = Attacher::AttachEngine3D
  FirstAngle = 0
  Height = 4
  Radius = 151
  SecondAngle = 0
FEATURE [Part::Cut] Cut019
  Base = -> Cylinder048
  Placement = pos=(165,4,165) rot=(1,0,0;1.5708rad)
  Tool = -> Cylinder049
FEATURE [Part::Cut] Cut020  label="MainChamberModel"
  Base = -> Cut018
  Tool = -> Cut019
